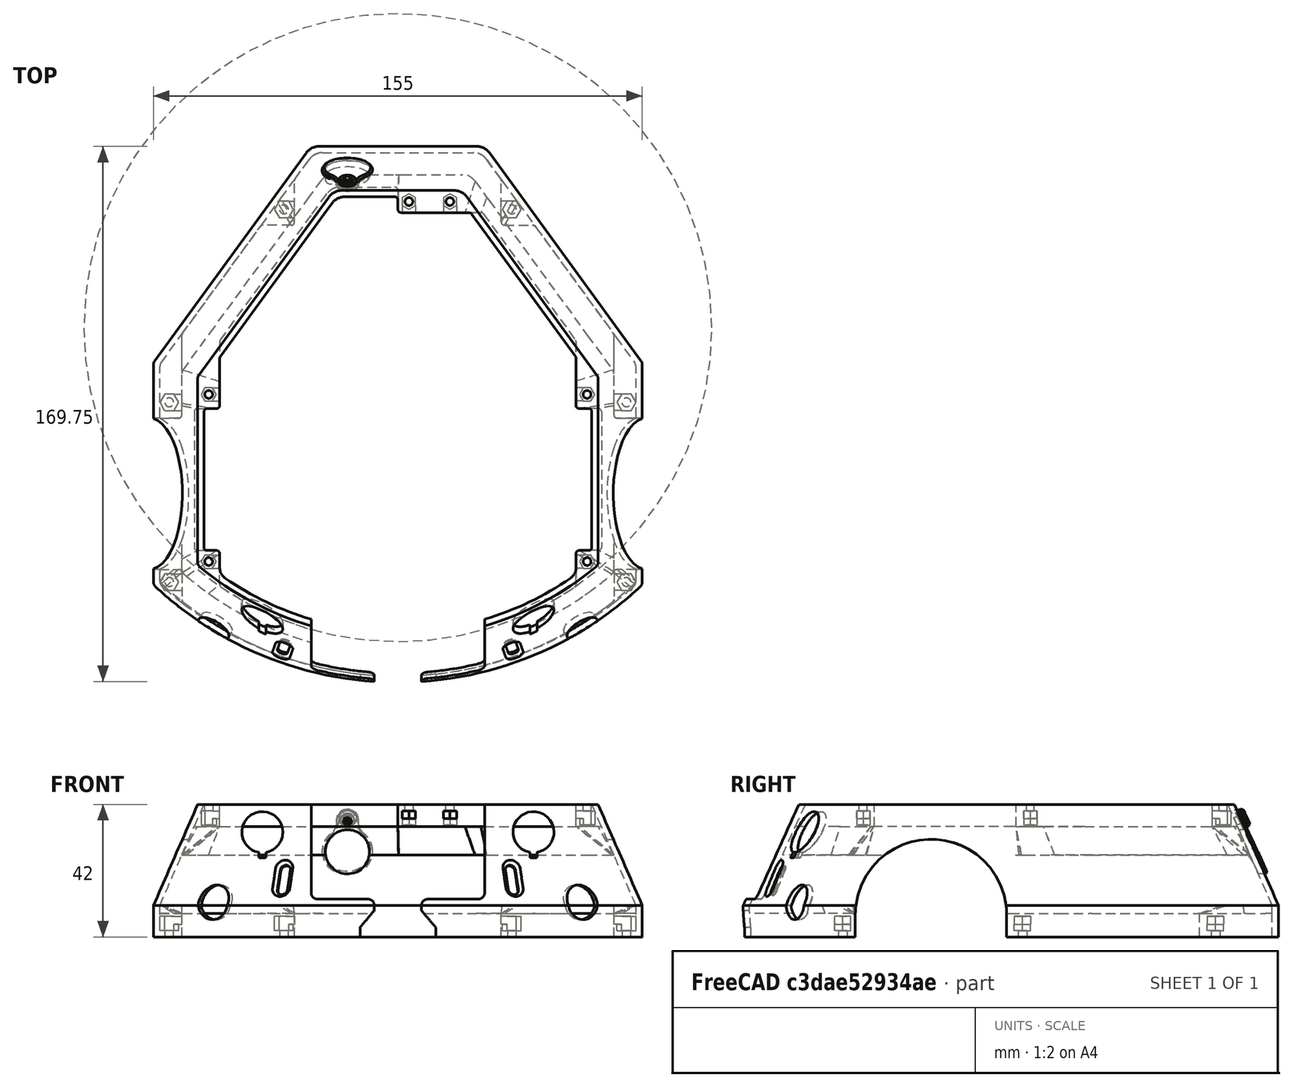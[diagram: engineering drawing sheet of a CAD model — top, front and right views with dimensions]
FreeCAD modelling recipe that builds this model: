
FCSTD DOCUMENT  (FreeCAD 0.19R24276 (Git))
Label: PB3D_TriPlate_Shell
License: All rights reserved
LicenseURL: http://en.wikipedia.org/wiki/All_rights_reserved
objects: Sketcher::SketchObject×33, PartDesign::Pocket×17, PartDesign::Plane×14, PartDesign::SubtractiveLoft×4, PartDesign::Body×3, Spreadsheet::Sheet×2, PartDesign::Pad×2, PartDesign::Chamfer×2, PartDesign::AdditiveLoft×1, PartDesign::Groove×1, PartDesign::Revolution×1, App::Part×1, Mesh::Feature×1
note: 106 computed .brp shape members not serialized (recipe doc carries the construction recipe); baked Part::Feature solids carry a one-line shape summary decoded from their .brp

FEATURE [PartDesign::Plane] DatumPlane  label="Datum_ShelllTop"
  AttachmentOffset = pos=(0,0,42) rot=(0,0,1;0rad)
  Length = 187.44
  MapMode = 5
  Placement = pos=(0,0,42) rot=(0,0,1;0rad)
  ResizeMode = 0
  Support = -> [XY_Plane002]
  Width = 202.177
  expr: .AttachmentOffset.Base.z = Spreadsheet.shell_totheight
FEATURE [PartDesign::Plane] DatumPlane001  label="Datum_ShellVert"
  AttachmentOffset = pos=(0,0,10) rot=(0,0,1;0rad)
  Length = 187.44
  MapMode = 5
  Placement = pos=(0,0,10) rot=(0,0,1;0rad)
  ResizeMode = 0
  Support = -> [XY_Plane002]
  Width = 202.177
  expr: .AttachmentOffset.Base.z = Spreadsheet.shell_vertheight
FEATURE [Spreadsheet::Sheet] Spreadsheet  label="params"
  cells = A1=Std. Wall Thick; B1(std_wall_thick)==2mm; C1=Std. Tol. Clear; D1(std_tol_clear)==0.3mm; A2=Bottom Plate Main Params; C2=Shell Main Params; E2=Shell Calc Params; I2=LSR Vis Holes; A3=Plate Length; B3(plate_length)==170mm; C3=Shell Height; D3(shell_totheight)==42mm; E3=Top Brack Ang Start Z ; F3(shell_topbrack_angstart_z)==shell_totheight - shell_topbrack_vertheight - shell_topbrack_angleheight; G3=Top Brack Ang Start Overhang; H3(shell_topbrack_angstart_overhang)==shell_overhang_slope * shell_topbrack_angstart_z + shell_overhang_offset; I3=LSR Vis Angle; J3(LSRvis_angle)=31.5; A4=Plate Width; B4(plate_width)==155mm; C4=Shell Vert Height; D4(shell_vertheight)==10mm; E4=Top Brack Ang End Z; F4(shell_topbrack_angend_z)==shell_totheight - shell_topbrack_vertheight; G4=Top Bracket End Overhang; H4(shell_topbrack_angend_overhang)==shell_overhang_slope * shell_topbrack_angend_z + shell_overhang_offset; I4=LSR Vis Offset; J4(LSRvis_offset)==52.68mm; A5=Front Diameter; B5(front_diameter)==225mm; C5=Shell Overhang Length; D5(shell_overhang_leng)==14mm; I5=LSR Vis Diam; J5(LSRvis_diam)==11mm; A6=Tail Width; B6(tail_width)==50mm; C6=Shell Wall Thickness; D6(shell_wall_thick)==2mm; G6=Shell Angle Overhang Calc; I6=LSR Vis Hole Height; J6(LSRvis_hole_height)==11mm; A7=Plate Thickness; B7(plate_thick)==3mm; C7=Shell Foot Params; E7=Shell Top Bracket Params; G7=Overhang Slope; H7(shell_overhang_slope)==shell_overhang_leng / (shell_totheight - shell_vertheight); C8=Shell (Foot) Base Bracket Height; D8(shell_foot_height)==7.5mm; E8=Top Brack Height; F8(shell_topbrack_vertheight)==7mm; G8=Overhang Offset; H8(shell_overhang_offset)==-1 * shell_vertheight * shell_overhang_slope; I8=X Port Front; A9=Front Vert. Edge; B9(front_vert_edge)==2mm; C9=Shell Side Foot Width; D9(shell_footside_width)==7mm; E9=Top Brack Angle Height; F9(shell_topbrack_angleheight)==9mm; I9=XPort Diam; J9(xport_diam)==13mm; A10=Back Vert. Edge; B10(back_vert_edge)==15mm; C10=Shell Back Foot Width; D10(shell_footback_width)==10mm; E10=Top Brack Width; F10(shell_topbrack_width)==7mm; G10=Shell Mts; I10=XPort Height Loc; J10(xport_height_loc)==33.25mm; C11=Shell Back Foot Loc; D11(shell_footback_loc)==25mm; E11=Top Brack Front Split; F11(shell_topbrack_frontsplit)==50mm; G11=ShellToBot FrMid Offset; H11(shelltobot_frontmid_offset_xy)==5mm; I11=XPort Offset Loc; J11(xport_offset_loc)==43mm; A12=Std. Radius; B12(std_rad)==2mm; C12=Shell Foot CSunk Z; D12(shell_foot_csunk_z)==2mm; E12=Top Brack CSunk Z; F12(shell_topbrack_csunk_z)==shell_topbrack_slot_z - shell_topbrack_slot_height; G12=ShellToBot Back Offset X; H12(shelltobot_back_offset_x)==6mm; I12=XPort Plate Diam; J12(xport_plate_diam)==16mm; A13=Wheel Well Radius; B13(wheel_well_rad)==7mm; C13=Shell Foot CSunk Height; D13(shell_foot_csunk_height)==m25_nut_min_depth; E13=Top Brack CSunk Height; F13(shell_topbrack_csunk_height)==m2_nut_min_depth + 0.25mm; G13=ShellToBot Back Offset Y; H13(shelltobot_back_offset_y)==20mm; A14=Tail Radius; B14(tail_rad)==5mm; C14=Shell Foot Slot Z; D14(shell_foot_slot_z)==shell_foot_csunk_z + shell_foot_csunk_height; E14=Top Brack Slot Z; F14(shell_topbrack_slot_z)==shell_totheight - 2mm; C15=Shell Foot Slot Height; D15(shell_foot_slot_height)==m25_nut_min_depth + 0.5mm; E15=Top Brack Slot Height; F15(shell_topbrack_slot_height)==m2_nut_min_depth + 0.75mm; G15=USB Port Opening; A16=Wheel Well Plate Width; B16(wheel_well_plate_width)==115mm; E16=Top Brack Hole Offset; F16(shell_topbrack_hole_offset)==3.5mm; G16=USBPort Diam; H16(USBport_diam)==14mm; A17=Wheel Well Clearance; B17(wheel_well_clearance)==48mm; C17=Shell Angled Height; D17(shell_overhang_height)==shell_totheight - shell_vertheight; E17=Top Brack Fr Leng; F17(top_brack_front_leng)==10mm; G17=USBPort Height; H17(USBport_height)==27mm; A18=Wheel Well Vert; B18(wheel_well_vert)==7mm; C18=Shell Angle; D18(shell_wall_angle)==atan(shell_overhang_leng / shell_overhang_height); G18=USBPort X Offset; H18(USBport_offset_x)==16mm; G19=USBPort Cover Diam; H19(USBport_cover_diam)==16mm; A20=M2 Bolt Clearances; C20=M2.5 Bolt Clearances; G20=USBPort Cover Mt Pt; H20(USBport_cover_mt_diam)==7mm; A21=Hole Clear Diam; B21(m2_hole_clear_diam)==2.5mm; C21=Hole Clear Diam; D21(m25_hole_clear_diam)==2.8mm; G21=USBPort Cover Spacing; H21(USBport_cover_spacing)==11mm; A22=Head Clear Diam; B22(m2_head_clear_diam)==4mm; C22=Head Clear Diam; D22(m25_head_clear_diam)==5mm; G22=USBPort Cov Thickness; H22(USBport_cover_thickness)==1.2mm; A23=Head Min Depth; B23(m2_head_min_depth)==1.3mm; C23=Head Min Depth; D23(m25_head_min_depth)==1.6mm; A24=Nut Clear Flat; B24(m2_nut_clear_flat)==4.2mm; C24=Nut Clear Flat; D24(m25_nut_clear_flat)==5.2mm; G24=USBPort Cov Pivot In Diam; H24(USBport_cover_pivot_inner_diam)==4mm; A25=Nut Min Depth; B25(m2_nut_min_depth)==1.75mm; C25=Nut Min Depth; D25(m25_nut_min_depth)==2mm; G25=USBPort Cov Pivot Out Diam; H25(USBport_cover_pivot_outer_diam)==USBport_cover_pivot_inner_diam + 0.3mm; G26=USBPort Cov Pivot Height; H26(USBport_cover_pivot_height)==USBport_cover_thickness + 0.1mm
FEATURE [Sketcher::SketchObject] Sketch001  label="Sketch_Shell"
  FullyConstrained = true
  MapMode = 5
  Support = -> [XY_Plane002]
  expr: Constraints[41] = <<params>>.tail_rad
  expr: Constraints[81] = <<params>>.std_rad
  expr: Constraints[80] = <<params>>.std_rad
  expr: Constraints[77] = <<params>>.back_vert_edge
  expr: Constraints[76] = <<params>>.front_vert_edge
  expr: Constraints[63] = <<params>>.std_rad
  expr: Constraints[47] = <<params>>.front_diameter
  expr: Constraints[36] = <<params>>.wheel_well_plate_width
  expr: Constraints[79] = <<params>>.plate_width
  expr: Constraints[78] = <<params>>.wheel_well_clearance
  expr: Constraints[42] = <<params>>.tail_width
  expr: Constraints[65] = <<params>>.std_rad
  expr: Constraints[40] = <<params>>.plate_length
  sketch-geometry (36):
    g0: LineSegment StartX=-57.5 StartY=17 StartZ=0 EndX=-57.5 EndY=-17 EndZ=0
    g1: LineSegment StartX=57.5 StartY=17 StartZ=0 EndX=57.5 EndY=-17 EndZ=0
    g2: LineSegment StartX=-57.5 StartY=0 StartZ=0 EndX=57.5 EndY=0 EndZ=0
    g3: LineSegment StartX=-64.5 StartY=-24 StartZ=0 EndX=64.5 EndY=-24 EndZ=0
    g4: LineSegment StartX=-64.5 StartY=24 StartZ=0 EndX=64.5 EndY=24 EndZ=0
    g5: LineSegment StartX=-64.5 StartY=-24 StartZ=0 EndX=-75.5 EndY=-24 EndZ=0
    g6: LineSegment StartX=64.5 StartY=-24 StartZ=0 EndX=75.5 EndY=-24 EndZ=0
    g7: ArcOfCircle CenterX=0 CenterY=52.6846 CenterZ=0 NormalX=0 NormalY=0 NormalZ=1 AngleXU=0 Radius=112.5 StartAngle=3.96017 EndAngle=5.4646
    g8: LineSegment StartX=-64.5 StartY=24 StartZ=0 EndX=-75.5 EndY=24 EndZ=0
    g9: LineSegment StartX=64.5 StartY=24 StartZ=0 EndX=75.5 EndY=24 EndZ=0
    g10: LineSegment StartX=-77.1162 StartY=42.1781 StartZ=0 EndX=-29.0404 EndY=108.13 EndZ=0
    g11: LineSegment StartX=-25 StartY=110.185 StartZ=0 EndX=25 EndY=110.185 EndZ=0
    g12: LineSegment StartX=29.0404 StartY=108.13 StartZ=0 EndX=77.1162 EndY=42.1781 EndZ=0
    g13: LineSegment StartX=0 StartY=0 StartZ=0 EndX=0 EndY=110.185 EndZ=0
    g14: ArcOfCircle CenterX=-25 CenterY=105.185 CenterZ=0 NormalX=0 NormalY=0 NormalZ=1 AngleXU=0 Radius=5 StartAngle=1.5708 EndAngle=2.5117
    g15: ArcOfCircle CenterX=25 CenterY=105.185 CenterZ=0 NormalX=0 NormalY=0 NormalZ=1 AngleXU=0 Radius=5 StartAngle=0.629894 EndAngle=1.5708
    g16: ArcOfCircle CenterX=-64.5 CenterY=17 CenterZ=0 NormalX=0 NormalY=0 NormalZ=1 AngleXU=0 Radius=7 StartAngle=0 EndAngle=1.5708
    g17: ArcOfCircle CenterX=-64.5 CenterY=-17 CenterZ=0 NormalX=0 NormalY=0 NormalZ=1 AngleXU=0 Radius=7 StartAngle=4.71239 EndAngle=6.28319
    g18: ArcOfCircle CenterX=64.5 CenterY=-17 CenterZ=0 NormalX=0 NormalY=0 NormalZ=1 AngleXU=0 Radius=7 StartAngle=3.14159 EndAngle=4.71239
    g19: ArcOfCircle CenterX=64.5 CenterY=17 CenterZ=0 NormalX=0 NormalY=0 NormalZ=1 AngleXU=0 Radius=7 StartAngle=1.5708 EndAngle=3.14159
    g20: GeomPoint X=0 Y=-59.8154 Z=0
    g21: Circle CenterX=0 CenterY=52.6846 CenterZ=0 NormalX=0 NormalY=0 NormalZ=1 AngleXU=0 Radius=112.5
    g22: LineSegment StartX=77.5 StartY=26 StartZ=0 EndX=77.5 EndY=41 EndZ=0
    g23: LineSegment StartX=77.5 StartY=-26 StartZ=0 EndX=77.5 EndY=-28 EndZ=0
    g24: LineSegment StartX=-77.5 StartY=-28 StartZ=0 EndX=-77.5 EndY=-26 EndZ=0
    g25: LineSegment StartX=-77.5 StartY=26 StartZ=0 EndX=-77.5 EndY=41 EndZ=0
    g26: ArcOfCircle CenterX=75.5 CenterY=-28 CenterZ=0 NormalX=0 NormalY=0 NormalZ=1 AngleXU=0 Radius=2 StartAngle=5.4646 EndAngle=6.28319
    g27: ArcOfCircle CenterX=75.5 CenterY=-26 CenterZ=0 NormalX=0 NormalY=0 NormalZ=1 AngleXU=0 Radius=2 StartAngle=3e-16 EndAngle=1.5708
    g28: ArcOfCircle CenterX=-75.5 CenterY=-28 CenterZ=0 NormalX=0 NormalY=0 NormalZ=1 AngleXU=0 Radius=2 StartAngle=3.14159 EndAngle=3.96017
    g29: ArcOfCircle CenterX=-75.5 CenterY=-26 CenterZ=0 NormalX=0 NormalY=0 NormalZ=1 AngleXU=0 Radius=2 StartAngle=1.5708 EndAngle=3.14159
    g30: ArcOfCircle CenterX=75.5 CenterY=26 CenterZ=0 NormalX=0 NormalY=0 NormalZ=1 AngleXU=0 Radius=2 StartAngle=4.71239 EndAngle=6.28319
    g31: ArcOfCircle CenterX=75.5 CenterY=41 CenterZ=0 NormalX=0 NormalY=0 NormalZ=1 AngleXU=0 Radius=2 StartAngle=-9e-16 EndAngle=0.629894
    g32: ArcOfCircle CenterX=-75.5 CenterY=26 CenterZ=0 NormalX=0 NormalY=0 NormalZ=1 AngleXU=0 Radius=2 StartAngle=3.14159 EndAngle=4.71239
    g33: ArcOfCircle CenterX=-75.5 CenterY=41 CenterZ=0 NormalX=0 NormalY=0 NormalZ=1 AngleXU=0 Radius=2 StartAngle=2.5117 EndAngle=3.14159
    g34: LineSegment StartX=77.5 StartY=26 StartZ=0 EndX=77.5 EndY=-26 EndZ=0
    g35: LineSegment StartX=-77.5 StartY=26 StartZ=0 EndX=-77.5 EndY=-26 EndZ=0
  constraints (86):
    c: Vertical(g0)
    c: Vertical(g1)
    c: Horizontal(g2)
    c: Symmetric(g2,g2,g-1)
    c: Horizontal(g3)
    c: Horizontal(g5)
    c: Horizontal(g6)
    c: PointOnObject(g7,g-2)
    c: Horizontal(g8)
    c: Horizontal(g9)
    c: Horizontal(g11)
    c: Coincident(g13,g-1)
    c: PointOnObject(g13,g-2)
    c: Tangent(g10,g14) = 1.5708
    c: Tangent(g11,g14) = 1.5708
    c: Tangent(g11,g15) = 1.5708
    c: Tangent(g12,g15) = 1.5708
    c: Tangent(g8,g16) = -1.5708
    c: Tangent(g0,g16) = 1.5708
    c: Tangent(g5,g17) = 1.5708
    c: Tangent(g0,g17) = 1.5708
    c: Tangent(g1,g18) = -1.5708
    c: Tangent(g6,g18) = -1.5708
    c: Tangent(g1,g19) = -1.5708
    c: Tangent(g9,g19) = 1.5708
    c: Equal(g15,g14)
    c: Symmetric(g11,g11,g13)
    c: Equal(g18,g19)
    c: Equal(g19,g16)
    c: Equal(g16,g17)
    c: PointOnObject(g20,g-2)
    c: PointOnObject(g20,g7)
    c: Coincident(g4,g8)
    c: Coincident(g4,g9)
    c: Coincident(g3,g6)
    c: Coincident(g3,g5)
    c: DistanceX(g2,g2) = 115
    c: Symmetric(g0,g0,g2)
    c: Symmetric(g1,g1,g2)
    c: Radius(g19) = 7
    c: DistanceY(g20,g11) = 170
    c: Radius(g15) = 5
    c: DistanceX(g11,g11) = 50
    c: Equal(g9,g8)
    c: Equal(g9,g6)
    c: Coincident(g21,g7)
    c: PointOnObject(g20,g21)
    c: Diameter(g21) = 225
    c: Vertical(g22)
    c: Vertical(g23)
    c: Vertical(g24)
    c: Vertical(g25)
    c: Equal(g5,g8)
    c: Equal(g10,g12)
    c: Tangent(g7,g26) = -1.5708
    c: Tangent(g23,g26) = 1.5708
    c: Tangent(g23,g27) = 1.5708
    c: Tangent(g6,g27) = 1.5708
    c: Tangent(g7,g28) = -1.5708
    c: Tangent(g24,g28) = 1.5708
    c: Tangent(g24,g29) = 1.5708
    c: Tangent(g5,g29) = -1.5708
    c: Equal(g29,g27)
    c: Radius(g27) = 2
    c: Equal(g26,g28)
    c: Radius(g26) = 2
    c: Tangent(g9,g30) = -1.5708
    c: Tangent(g22,g30) = -1.5708
    c: Tangent(g22,g31) = -1.5708
    c: Tangent(g12,g31) = 1.5708
    c: Tangent(g8,g32) = 1.5708
    c: Tangent(g25,g32) = 1.5708
    c: Tangent(g10,g33) = 1.5708
    c: Tangent(g25,g33) = 1.5708
    c: Equal(g30,g32)
    c: Equal(g31,g33)
    c: DistanceY(g23,g23) = 2
    c: DistanceY(g22,g22) = 15
    c: DistanceY(g6,g9) = 48
    c: DistanceX(g24,g23) = 155
    c: Radius(g30) = 2
    c: Radius(g31) = 2
    c: Coincident(g34,g22)
    c: Coincident(g34,g23)
    c: Coincident(g35,g25)
    c: Coincident(g35,g24)
FEATURE [PartDesign::Pad] Pad001  label="Shell_Vert_Ext"
  Direction = (1,1,1)
  Length = 10
  Length2 = 100
  Profile = -> Sketch001
  Type = 0
  expr: Length = Spreadsheet.shell_vertheight
FEATURE [Sketcher::SketchObject] Sketch002  label="Sketch_Shell_Vert"
  FullyConstrained = true
  MapMode = 5
  Placement = pos=(0,0,10) rot=(0,0,1;0rad)
  Support = -> [DatumPlane001]
  expr: Constraints[40] = <<params>>.plate_length
  expr: Constraints[65] = <<params>>.std_rad
  expr: Constraints[42] = <<params>>.tail_width
  expr: Constraints[78] = <<params>>.wheel_well_clearance
  expr: Constraints[79] = <<params>>.plate_width
  expr: Constraints[36] = <<params>>.wheel_well_plate_width
  expr: Constraints[47] = <<params>>.front_diameter
  expr: Constraints[63] = <<params>>.std_rad
  expr: Constraints[76] = <<params>>.front_vert_edge
  expr: Constraints[77] = <<params>>.back_vert_edge
  expr: Constraints[80] = <<params>>.std_rad
  expr: Constraints[81] = <<params>>.std_rad
  expr: Constraints[41] = <<params>>.tail_rad
  sketch-geometry (38):
    g0: LineSegment StartX=-57.5 StartY=17 StartZ=0 EndX=-57.5 EndY=-17 EndZ=0
    g1: LineSegment StartX=57.5 StartY=17 StartZ=0 EndX=57.5 EndY=-17 EndZ=0
    g2: LineSegment StartX=-57.5 StartY=0 StartZ=0 EndX=57.5 EndY=0 EndZ=0
    g3: LineSegment StartX=-64.5 StartY=-24 StartZ=0 EndX=64.5 EndY=-24 EndZ=0
    g4: LineSegment StartX=-64.5 StartY=24 StartZ=0 EndX=64.5 EndY=24 EndZ=0
    g5: LineSegment StartX=-64.5 StartY=-24 StartZ=0 EndX=-75.5 EndY=-24 EndZ=0
    g6: LineSegment StartX=64.5 StartY=-24 StartZ=0 EndX=75.5 EndY=-24 EndZ=0
    g7: ArcOfCircle CenterX=0 CenterY=52.6846 CenterZ=0 NormalX=0 NormalY=0 NormalZ=1 AngleXU=0 Radius=112.5 StartAngle=3.96017 EndAngle=5.4646
    g8: LineSegment StartX=-64.5 StartY=24 StartZ=0 EndX=-75.5 EndY=24 EndZ=0
    g9: LineSegment StartX=64.5 StartY=24 StartZ=0 EndX=75.5 EndY=24 EndZ=0
    g10: LineSegment StartX=-77.1162 StartY=42.1781 StartZ=0 EndX=-29.0404 EndY=108.13 EndZ=0
    g11: LineSegment StartX=-25 StartY=110.185 StartZ=0 EndX=25 EndY=110.185 EndZ=0
    g12: LineSegment StartX=29.0404 StartY=108.13 StartZ=0 EndX=77.1162 EndY=42.1781 EndZ=0
    g13: LineSegment StartX=0 StartY=0 StartZ=0 EndX=0 EndY=110.185 EndZ=0
    g14: ArcOfCircle CenterX=-25 CenterY=105.185 CenterZ=0 NormalX=0 NormalY=0 NormalZ=1 AngleXU=0 Radius=5 StartAngle=1.5708 EndAngle=2.5117
    g15: ArcOfCircle CenterX=25 CenterY=105.185 CenterZ=0 NormalX=0 NormalY=0 NormalZ=1 AngleXU=0 Radius=5 StartAngle=0.629894 EndAngle=1.5708
    g16: ArcOfCircle CenterX=-64.5 CenterY=17 CenterZ=0 NormalX=0 NormalY=0 NormalZ=1 AngleXU=0 Radius=7 StartAngle=0 EndAngle=1.5708
    g17: ArcOfCircle CenterX=-64.5 CenterY=-17 CenterZ=0 NormalX=0 NormalY=0 NormalZ=1 AngleXU=0 Radius=7 StartAngle=4.71239 EndAngle=6.28319
    g18: ArcOfCircle CenterX=64.5 CenterY=-17 CenterZ=0 NormalX=0 NormalY=0 NormalZ=1 AngleXU=0 Radius=7 StartAngle=3.14159 EndAngle=4.71239
    g19: ArcOfCircle CenterX=64.5 CenterY=17 CenterZ=0 NormalX=0 NormalY=0 NormalZ=1 AngleXU=0 Radius=7 StartAngle=1.5708 EndAngle=3.14159
    g20: GeomPoint X=0 Y=-59.8154 Z=0
    g21: Circle CenterX=0 CenterY=52.6846 CenterZ=0 NormalX=0 NormalY=0 NormalZ=1 AngleXU=0 Radius=112.5
    g22: LineSegment StartX=77.5 StartY=26 StartZ=0 EndX=77.5 EndY=41 EndZ=0
    g23: LineSegment StartX=77.5 StartY=-26 StartZ=0 EndX=77.5 EndY=-28 EndZ=0
    g24: LineSegment StartX=-77.5 StartY=-28 StartZ=0 EndX=-77.5 EndY=-26 EndZ=0
    g25: LineSegment StartX=-77.5 StartY=26 StartZ=0 EndX=-77.5 EndY=41 EndZ=0
    g26: ArcOfCircle CenterX=75.5 CenterY=-28 CenterZ=0 NormalX=0 NormalY=0 NormalZ=1 AngleXU=0 Radius=2 StartAngle=5.4646 EndAngle=6.28319
    g27: ArcOfCircle CenterX=75.5 CenterY=-26 CenterZ=0 NormalX=0 NormalY=0 NormalZ=1 AngleXU=0 Radius=2 StartAngle=-9e-16 EndAngle=1.5708
    g28: ArcOfCircle CenterX=-75.5 CenterY=-28 CenterZ=0 NormalX=0 NormalY=0 NormalZ=1 AngleXU=0 Radius=2 StartAngle=3.14159 EndAngle=3.96017
    g29: ArcOfCircle CenterX=-75.5 CenterY=-26 CenterZ=0 NormalX=0 NormalY=0 NormalZ=1 AngleXU=0 Radius=2 StartAngle=1.5708 EndAngle=3.14159
    g30: ArcOfCircle CenterX=75.5 CenterY=26 CenterZ=0 NormalX=0 NormalY=0 NormalZ=1 AngleXU=0 Radius=2 StartAngle=4.71239 EndAngle=6.28319
    g31: ArcOfCircle CenterX=75.5 CenterY=41 CenterZ=0 NormalX=0 NormalY=0 NormalZ=1 AngleXU=0 Radius=2 StartAngle=0 EndAngle=0.629894
    g32: ArcOfCircle CenterX=-75.5 CenterY=26 CenterZ=0 NormalX=0 NormalY=0 NormalZ=1 AngleXU=0 Radius=2 StartAngle=3.14159 EndAngle=4.71239
    g33: ArcOfCircle CenterX=-75.5 CenterY=41 CenterZ=0 NormalX=0 NormalY=0 NormalZ=1 AngleXU=0 Radius=2 StartAngle=2.5117 EndAngle=3.14159
    g34: LineSegment StartX=77.5 StartY=26 StartZ=0 EndX=77.5 EndY=-26 EndZ=0
    g35: LineSegment StartX=-77.5 StartY=26 StartZ=0 EndX=-77.5 EndY=-26 EndZ=0
    g36: LineSegment StartX=77.5 StartY=41 StartZ=0 EndX=77.5 EndY=-28 EndZ=0
    g37: LineSegment StartX=-77.5 StartY=41 StartZ=0 EndX=-77.5 EndY=-28 EndZ=0
  constraints (90):
    c: Vertical(g0)
    c: Vertical(g1)
    c: Horizontal(g2)
    c: Symmetric(g2,g2,g-1)
    c: Horizontal(g3)
    c: Horizontal(g5)
    c: Horizontal(g6)
    c: PointOnObject(g7,g-2)
    c: Horizontal(g8)
    c: Horizontal(g9)
    c: Horizontal(g11)
    c: Coincident(g13,g-1)
    c: PointOnObject(g13,g-2)
    c: Tangent(g10,g14) = 1.5708
    c: Tangent(g11,g14) = 1.5708
    c: Tangent(g11,g15) = 1.5708
    c: Tangent(g12,g15) = 1.5708
    c: Tangent(g8,g16) = -1.5708
    c: Tangent(g0,g16) = 1.5708
    c: Tangent(g5,g17) = 1.5708
    c: Tangent(g0,g17) = 1.5708
    c: Tangent(g1,g18) = -1.5708
    c: Tangent(g6,g18) = -1.5708
    c: Tangent(g1,g19) = -1.5708
    c: Tangent(g9,g19) = 1.5708
    c: Equal(g15,g14)
    c: Symmetric(g11,g11,g13)
    c: Equal(g18,g19)
    c: Equal(g19,g16)
    c: Equal(g16,g17)
    c: PointOnObject(g20,g-2)
    c: PointOnObject(g20,g7)
    c: Coincident(g4,g8)
    c: Coincident(g4,g9)
    c: Coincident(g3,g6)
    c: Coincident(g3,g5)
    c: DistanceX(g2,g2) = 115
    c: Symmetric(g0,g0,g2)
    c: Symmetric(g1,g1,g2)
    c: Radius(g19) = 7
    c: DistanceY(g20,g11) = 170
    c: Radius(g15) = 5
    c: DistanceX(g11,g11) = 50
    c: Equal(g9,g8)
    c: Equal(g9,g6)
    c: Coincident(g21,g7)
    c: PointOnObject(g20,g21)
    c: Diameter(g21) = 225
    c: Vertical(g22)
    c: Vertical(g23)
    c: Vertical(g24)
    c: Vertical(g25)
    c: Equal(g5,g8)
    c: Equal(g10,g12)
    c: Tangent(g7,g26) = -1.5708
    c: Tangent(g23,g26) = 1.5708
    c: Tangent(g23,g27) = 1.5708
    c: Tangent(g6,g27) = 1.5708
    c: Tangent(g7,g28) = -1.5708
    c: Tangent(g24,g28) = 1.5708
    c: Tangent(g24,g29) = 1.5708
    c: Tangent(g5,g29) = -1.5708
    c: Equal(g29,g27)
    c: Radius(g27) = 2
    c: Equal(g26,g28)
    c: Radius(g26) = 2
    c: Tangent(g9,g30) = -1.5708
    c: Tangent(g22,g30) = -1.5708
    c: Tangent(g22,g31) = -1.5708
    c: Tangent(g12,g31) = 1.5708
    c: Tangent(g8,g32) = 1.5708
    c: Tangent(g25,g32) = 1.5708
    c: Tangent(g10,g33) = 1.5708
    c: Tangent(g25,g33) = 1.5708
    c: Equal(g30,g32)
    c: Equal(g31,g33)
    c: DistanceY(g23,g23) = 2
    c: DistanceY(g22,g22) = 15
    c: DistanceY(g6,g9) = 48
    c: DistanceX(g24,g23) = 155
    c: Radius(g30) = 2
    c: Radius(g31) = 2
    c: Coincident(g34,g22)
    c: Coincident(g34,g23)
    c: Coincident(g35,g25)
    c: Coincident(g35,g24)
    c: Coincident(g37,g28)
    c: Coincident(g37,g33)
    c: Coincident(g36,g31)
    c: Coincident(g36,g26)
FEATURE [Sketcher::SketchObject] Sketch003  label="Sketch_Shell_Top"
  FullyConstrained = true
  MapMode = 5
  Placement = pos=(0,0,42) rot=(0,0,1;0rad)
  Support = -> [DatumPlane]
  expr: Constraints[114] = <<params>>.shell_overhang_leng
  expr: Constraints[63] = <<params>>.std_rad
  expr: Constraints[47] = <<params>>.front_diameter
  expr: Constraints[113] = Spreadsheet.shell_overhang_leng
  expr: Constraints[77] = <<params>>.back_vert_edge
  expr: Constraints[119] = <<params>>.shell_overhang_leng
  expr: Constraints[117] = <<params>>.shell_overhang_leng
  expr: Constraints[80] = <<params>>.std_rad
  expr: Constraints[41] = <<params>>.tail_rad
  expr: Constraints[76] = <<params>>.front_vert_edge
  expr: Constraints[36] = <<params>>.wheel_well_plate_width - 2 * Spreadsheet.shell_overhang_leng
  expr: Constraints[79] = <<params>>.plate_width
  expr: Constraints[42] = <<params>>.tail_width
  expr: Constraints[78] = <<params>>.wheel_well_clearance
  expr: Constraints[65] = <<params>>.std_rad
  expr: Constraints[40] = <<params>>.plate_length
  expr: Constraints[88] = Spreadsheet.shell_overhang_leng
  expr: Constraints[81] = <<params>>.std_rad
  sketch-geometry (52):
    g0: LineSegment StartX=-43.5 StartY=17 StartZ=0 EndX=-43.5 EndY=-17 EndZ=0
    g1: LineSegment StartX=43.5 StartY=17 StartZ=0 EndX=43.5 EndY=-17 EndZ=0
    g2: LineSegment StartX=-43.5 StartY=0 StartZ=0 EndX=43.5 EndY=0 EndZ=0
    g3: LineSegment StartX=-50.5 StartY=-24 StartZ=0 EndX=50.5 EndY=-24 EndZ=0
    g4: LineSegment StartX=-50.5 StartY=24 StartZ=0 EndX=50.5 EndY=24 EndZ=0
    g5: LineSegment StartX=-50.5 StartY=-24 StartZ=0 EndX=-75.5 EndY=-24 EndZ=0
    g6: LineSegment StartX=50.5 StartY=-24 StartZ=0 EndX=75.5 EndY=-24 EndZ=0
    g7: ArcOfCircle CenterX=0 CenterY=52.6846 CenterZ=0 NormalX=0 NormalY=0 NormalZ=1 AngleXU=0 Radius=112.5 StartAngle=3.96017 EndAngle=5.4646
    g8: LineSegment StartX=-50.5 StartY=24 StartZ=0 EndX=-75.5 EndY=24 EndZ=0
    g9: LineSegment StartX=50.5 StartY=24 StartZ=0 EndX=75.5 EndY=24 EndZ=0
    g10: LineSegment StartX=-77.1162 StartY=42.1781 StartZ=0 EndX=-29.0404 EndY=108.13 EndZ=0
    g11: LineSegment StartX=-25 StartY=110.185 StartZ=0 EndX=25 EndY=110.185 EndZ=0
    g12: LineSegment StartX=29.0404 StartY=108.13 StartZ=0 EndX=77.1162 EndY=42.1781 EndZ=0
    g13: LineSegment StartX=0 StartY=0 StartZ=0 EndX=0 EndY=110.185 EndZ=0
    g14: ArcOfCircle CenterX=-25 CenterY=105.185 CenterZ=0 NormalX=0 NormalY=0 NormalZ=1 AngleXU=0 Radius=5 StartAngle=1.5708 EndAngle=2.5117
    g15: ArcOfCircle CenterX=25 CenterY=105.185 CenterZ=0 NormalX=0 NormalY=0 NormalZ=1 AngleXU=0 Radius=5 StartAngle=0.629894 EndAngle=1.5708
    g16: ArcOfCircle CenterX=-50.5 CenterY=17 CenterZ=0 NormalX=0 NormalY=0 NormalZ=1 AngleXU=0 Radius=7 StartAngle=0 EndAngle=1.5708
    g17: ArcOfCircle CenterX=-50.5 CenterY=-17 CenterZ=0 NormalX=0 NormalY=0 NormalZ=1 AngleXU=0 Radius=7 StartAngle=4.71239 EndAngle=6.28319
    g18: ArcOfCircle CenterX=50.5 CenterY=-17 CenterZ=0 NormalX=0 NormalY=0 NormalZ=1 AngleXU=0 Radius=7 StartAngle=3.14159 EndAngle=4.71239
    g19: ArcOfCircle CenterX=50.5 CenterY=17 CenterZ=0 NormalX=0 NormalY=0 NormalZ=1 AngleXU=0 Radius=7 StartAngle=1.5708 EndAngle=3.14159
    g20: GeomPoint X=0 Y=-59.8154 Z=0
    g21: Circle CenterX=0 CenterY=52.6846 CenterZ=0 NormalX=0 NormalY=0 NormalZ=1 AngleXU=0 Radius=112.5
    g22: LineSegment StartX=77.5 StartY=26 StartZ=0 EndX=77.5 EndY=41 EndZ=0
    g23: LineSegment StartX=77.5 StartY=-26 StartZ=0 EndX=77.5 EndY=-28 EndZ=0
    g24: LineSegment StartX=-77.5 StartY=-28 StartZ=0 EndX=-77.5 EndY=-26 EndZ=0
    g25: LineSegment StartX=-77.5 StartY=26 StartZ=0 EndX=-77.5 EndY=41 EndZ=0
    g26: ArcOfCircle CenterX=75.5 CenterY=-28 CenterZ=0 NormalX=0 NormalY=0 NormalZ=1 AngleXU=0 Radius=2 StartAngle=5.4646 EndAngle=6.28319
    g27: ArcOfCircle CenterX=75.5 CenterY=-26 CenterZ=0 NormalX=0 NormalY=0 NormalZ=1 AngleXU=0 Radius=2 StartAngle=0 EndAngle=1.5708
    g28: ArcOfCircle CenterX=-75.5 CenterY=-28 CenterZ=0 NormalX=0 NormalY=0 NormalZ=1 AngleXU=0 Radius=2 StartAngle=3.14159 EndAngle=3.96017
    g29: ArcOfCircle CenterX=-75.5 CenterY=-26 CenterZ=0 NormalX=0 NormalY=0 NormalZ=1 AngleXU=0 Radius=2 StartAngle=1.5708 EndAngle=3.14159
    g30: ArcOfCircle CenterX=75.5 CenterY=26 CenterZ=0 NormalX=0 NormalY=0 NormalZ=1 AngleXU=0 Radius=2 StartAngle=4.71239 EndAngle=6.28319
    g31: ArcOfCircle CenterX=75.5 CenterY=41 CenterZ=0 NormalX=0 NormalY=0 NormalZ=1 AngleXU=0 Radius=2 StartAngle=1.7e-15 EndAngle=0.629894
    g32: ArcOfCircle CenterX=-75.5 CenterY=26 CenterZ=0 NormalX=0 NormalY=0 NormalZ=1 AngleXU=0 Radius=2 StartAngle=3.14159 EndAngle=4.71239
    g33: ArcOfCircle CenterX=-75.5 CenterY=41 CenterZ=0 NormalX=0 NormalY=0 NormalZ=1 AngleXU=0 Radius=2 StartAngle=2.5117 EndAngle=3.14159
    g34: LineSegment StartX=77.5 StartY=26 StartZ=0 EndX=77.5 EndY=-26 EndZ=0
    g35: LineSegment StartX=-77.5 StartY=26 StartZ=0 EndX=-77.5 EndY=-26 EndZ=0
    g36: LineSegment StartX=-17.8805 StartY=96.1846 StartZ=0 EndX=17.8805 EndY=96.1846 EndZ=0
    g37: GeomPoint X=0 Y=96.1846 Z=0
    g38: LineSegment StartX=-21.921 StartY=94.1299 StartZ=0 EndX=-63.1162 EndY=37.617 EndZ=0
    g39: LineSegment StartX=-63.5 StartY=36.4389 StartZ=0 EndX=-63.5 EndY=-21.6794 EndZ=0
    g40: LineSegment StartX=21.921 StartY=94.1299 StartZ=0 EndX=63.1162 EndY=37.617 EndZ=0
    g41: LineSegment StartX=63.5 StartY=36.4389 StartZ=0 EndX=63.5 EndY=-21.6794 EndZ=0
    g42: LineSegment StartX=-63.5 StartY=36.4389 StartZ=0 EndX=63.5 EndY=36.4389 EndZ=0
    g43: GeomPoint X=0 Y=-45.8154 Z=0
    g44: ArcOfCircle CenterX=-17.8805 CenterY=91.1846 CenterZ=0 NormalX=0 NormalY=0 NormalZ=1 AngleXU=0 Radius=5 StartAngle=1.5708 EndAngle=2.5117
    g45: ArcOfCircle CenterX=17.8805 CenterY=91.1846 CenterZ=0 NormalX=0 NormalY=0 NormalZ=1 AngleXU=0 Radius=5 StartAngle=0.629894 EndAngle=1.5708
    g46: ArcOfCircle CenterX=61.5 CenterY=36.4389 CenterZ=0 NormalX=0 NormalY=0 NormalZ=1 AngleXU=0 Radius=2 StartAngle=9e-16 EndAngle=0.629894
    g47: ArcOfCircle CenterX=-61.5 CenterY=36.4389 CenterZ=0 NormalX=0 NormalY=0 NormalZ=1 AngleXU=0 Radius=2 StartAngle=2.5117 EndAngle=3.14159
    g48: ArcOfCircle CenterX=61.5 CenterY=-21.6794 CenterZ=0 NormalX=0 NormalY=0 NormalZ=1 AngleXU=0 Radius=2 StartAngle=5.40338 EndAngle=6.28319
    g49: ArcOfCircle CenterX=-61.5 CenterY=-21.6794 CenterZ=0 NormalX=0 NormalY=0 NormalZ=1 AngleXU=0 Radius=2 StartAngle=3.14159 EndAngle=4.02139
    g50: LineSegment StartX=-29.0404 StartY=108.13 StartZ=0 EndX=-17.7272 EndY=99.883 EndZ=0
    g51: ArcOfCircle CenterX=0 CenterY=52.6846 CenterZ=0 NormalX=0 NormalY=0 NormalZ=1 AngleXU=0 Radius=98.5 StartAngle=4.02139 EndAngle=5.40339
  constraints (126):
    c: Vertical(g0)
    c: Vertical(g1)
    c: Horizontal(g2)
    c: Symmetric(g2,g2,g-1)
    c: Horizontal(g3)
    c: Horizontal(g5)
    c: Horizontal(g6)
    c: PointOnObject(g7,g-2)
    c: Horizontal(g8)
    c: Horizontal(g9)
    c: Horizontal(g11)
    c: Coincident(g13,g-1)
    c: PointOnObject(g13,g-2)
    c: Tangent(g10,g14) = 1.5708
    c: Tangent(g11,g14) = 1.5708
    c: Tangent(g11,g15) = 1.5708
    c: Tangent(g12,g15) = 1.5708
    c: Tangent(g8,g16) = -1.5708
    c: Tangent(g0,g16) = 1.5708
    c: Tangent(g5,g17) = 1.5708
    c: Tangent(g0,g17) = 1.5708
    c: Tangent(g1,g18) = -1.5708
    c: Tangent(g6,g18) = -1.5708
    c: Tangent(g1,g19) = -1.5708
    c: Tangent(g9,g19) = 1.5708
    c: Equal(g15,g14)
    c: Symmetric(g11,g11,g13)
    c: Equal(g18,g19)
    c: Equal(g19,g16)
    c: Equal(g16,g17)
    c: PointOnObject(g20,g-2)
    c: PointOnObject(g20,g7)
    c: Coincident(g4,g8)
    c: Coincident(g4,g9)
    c: Coincident(g3,g6)
    c: Coincident(g3,g5)
    c: DistanceX(g2,g2) = 87
    c: Symmetric(g0,g0,g2)
    c: Symmetric(g1,g1,g2)
    c: Radius(g19) = 7
    c: DistanceY(g20,g11) = 170
    c: Radius(g15) = 5
    c: DistanceX(g11,g11) = 50
    c: Equal(g9,g8)
    c: Equal(g9,g6)
    c: Coincident(g21,g7)
    c: PointOnObject(g20,g21)
    c: Diameter(g21) = 225
    c: Vertical(g22)
    c: Vertical(g23)
    c: Vertical(g24)
    c: Vertical(g25)
    c: Equal(g5,g8)
    c: Equal(g10,g12)
    c: Tangent(g7,g26) = -1.5708
    c: Tangent(g23,g26) = 1.5708
    c: Tangent(g23,g27) = 1.5708
    c: Tangent(g6,g27) = 1.5708
    c: Tangent(g7,g28) = -1.5708
    c: Tangent(g24,g28) = 1.5708
    c: Tangent(g24,g29) = 1.5708
    c: Tangent(g5,g29) = -1.5708
    c: Equal(g29,g27)
    c: Radius(g27) = 2
    c: Equal(g26,g28)
    c: Radius(g26) = 2
    c: Tangent(g9,g30) = -1.5708
    c: Tangent(g22,g30) = -1.5708
    c: Tangent(g22,g31) = -1.5708
    c: Tangent(g12,g31) = 1.5708
    c: Tangent(g8,g32) = 1.5708
    c: Tangent(g25,g32) = 1.5708
    c: Tangent(g10,g33) = 1.5708
    c: Tangent(g25,g33) = 1.5708
    c: Equal(g30,g32)
    c: Equal(g31,g33)
    c: DistanceY(g23,g23) = 2
    c: DistanceY(g22,g22) = 15
    c: DistanceY(g6,g9) = 48
    c: DistanceX(g24,g23) = 155
    c: Radius(g30) = 2
    c: Radius(g31) = 2
    c: Coincident(g34,g22)
    c: Coincident(g34,g23)
    c: Coincident(g35,g25)
    c: Coincident(g35,g24)
    c: Horizontal(g36)
    c: PointOnObject(g37,g13)
    c: DistanceY(g37,g13) = 14
    c: Vertical(g39)
    c: Vertical(g41)
    c: Horizontal(g42)
    c: Parallel(g40,g12)
    c: PointOnObject(g43,g-2)
    c: Tangent(g38,g44) = -1.5708
    c: Tangent(g36,g44) = 1.5708
    c: Tangent(g40,g45) = 1.5708
    c: Tangent(g36,g45) = 1.5708
    c: Tangent(g41,g46) = 1.5708
    c: Tangent(g40,g46) = 1.5708
    c: Tangent(g39,g47) = -1.5708
    c: Tangent(g38,g47) = -1.5708
    c: Tangent(g41,g48) = 1.5708
    c: Tangent(g39,g49) = -1.5708
    c: Coincident(g42,g39)
    c: Coincident(g42,g41)
    c: Equal(g15,g45)
    c: Equal(g45,g44)
    c: Symmetric(g36,g36,g37)
    c: Equal(g31,g46)
    c: Equal(g26,g48)
    c: Equal(g49,g29)
    c: Equal(g47,g32)
    c: DistanceY(g20,g43) = 14
    c: DistanceX(g41,g22) = 14
    c: PointOnObject(g50,g38)
    c: Perpendicular(g38,g50)
    c: Distance(g50) = 14
    c: Coincident(g50,g10)
    c: DistanceX(g24,g39) = 14
    c: Coincident(g51,g7)
    c: Coincident(g51,g49)
    c: Coincident(g51,g48)
    c: Tangent(g48,g51)
    c: PointOnObject(g43,g51)
    c: Tangent(g49,g51)
FEATURE [PartDesign::AdditiveLoft] AdditiveLoft  label="Shell_Angle_Ext"
  BaseFeature = -> Pad001
  Closed = false
  Profile = -> Sketch002
  Ruled = false
  Sections = -> [Sketch003]
FEATURE [PartDesign::Plane] DatumPlane002  label="Datum_BaseBrack"
  AttachmentOffset = pos=(0,0,7.5) rot=(0,0,1;0rad)
  Length = 187.44
  MapMode = 5
  Placement = pos=(0,0,7.5) rot=(0,0,1;0rad)
  ResizeMode = 0
  Support = -> [XY_Plane002]
  Width = 202.177
  expr: .AttachmentOffset.Base.z = Spreadsheet.shell_foot_height
FEATURE [PartDesign::Plane] DatumPlane003  label="Datum_TopBrack"
  AttachmentOffset = pos=(0,0,35) rot=(0,0,1;0rad)
  Length = 187.44
  MapMode = 5
  Placement = pos=(0,0,35) rot=(0,0,1;0rad)
  ResizeMode = 0
  Support = -> [XY_Plane002]
  Width = 202.177
  expr: .AttachmentOffset.Base.z = Spreadsheet.shell_totheight - Spreadsheet.shell_topbrack_vertheight
FEATURE [Sketcher::SketchObject] Sketch004  label="Sketch_WheelClear"
  FullyConstrained = true
  MapMode = 5
  Placement = pos=(0,0,0) rot=(0.57735,0.57735,0.57735;2.0944rad)
  Support = -> [YZ_Plane002]
  expr: Constraints[11] = <<params>>.wheel_well_vert
  expr: Constraints[13] = <<params>>.wheel_well_clearance
  sketch-geometry (5):
    g0: LineSegment StartX=-24 StartY=0 StartZ=0 EndX=24 EndY=0 EndZ=0
    g1: LineSegment StartX=-24 StartY=0 StartZ=0 EndX=-24 EndY=7 EndZ=0
    g2: LineSegment StartX=24 StartY=0 StartZ=0 EndX=24 EndY=7 EndZ=0
    g3: ArcOfCircle CenterX=-1.5e-15 CenterY=7 CenterZ=0 NormalX=0 NormalY=0 NormalZ=1 AngleXU=0 Radius=24 StartAngle=0 EndAngle=3.14159
    g4: LineSegment StartX=-24 StartY=7 StartZ=0 EndX=24 EndY=7 EndZ=0
  constraints (14):
    c: Horizontal(g0)
    c: Symmetric(g0,g0,g-1)
    c: Coincident(g1,g0)
    c: Vertical(g1)
    c: Coincident(g2,g0)
    c: Vertical(g2)
    c: Coincident(g3,g1)
    c: Coincident(g3,g2)
    c: Coincident(g4,g1)
    c: Coincident(g4,g2)
    c: PointOnObject(g3,g4)
    c: DistanceY(g0,g2) = 7
    c: Horizontal(g4)
    c: DistanceX(g1,g2) = 48
FEATURE [PartDesign::Pocket] Pocket  label="Wheel_Clear_Pocket"
  BaseFeature = -> AdditiveLoft
  Length = 5
  Length2 = 100
  Midplane = true
  Profile = -> Sketch004
  Type = 1
FEATURE [Sketcher::SketchObject] Sketch005  label="Sketch_Shell_Inner_CutFeet"
  FullyConstrained = true
  MapMode = 5
  Support = -> [XY_Plane002]
  expr: Constraints[78] = <<params>>.wheel_well_clearance
  expr: Constraints[42] = <<params>>.tail_width
  expr: Constraints[151] = <<params>>.shell_wall_thick
  expr: Constraints[47] = <<params>>.front_diameter
  expr: Constraints[81] = <<params>>.std_rad
  expr: Constraints[102] = <<params>>.shell_wall_thick
  expr: Constraints[96] = <<params>>.shell_wall_thick
  expr: Constraints[36] = <<params>>.wheel_well_plate_width
  expr: Constraints[63] = <<params>>.std_rad
  expr: Constraints[65] = <<params>>.std_rad
  expr: Constraints[40] = <<params>>.plate_length
  expr: Constraints[124] = Spreadsheet.shell_footside_width
  expr: Constraints[190] = <<params>>.shell_footback_width
  expr: Constraints[76] = <<params>>.front_vert_edge
  expr: Constraints[95] = <<params>>.shell_wall_thick
  expr: Constraints[79] = <<params>>.plate_width
  expr: Constraints[93] = <<params>>.shell_wall_thick
  expr: Constraints[41] = <<params>>.tail_rad
  expr: Constraints[80] = <<params>>.std_rad
  expr: Constraints[119] = <<params>>.std_rad / 2
  expr: Constraints[162] = <<params>>.std_rad / 2
  expr: Constraints[92] = <<params>>.shell_wall_thick
  expr: Constraints[77] = <<params>>.back_vert_edge
  expr: Constraints[175] = <<params>>.shell_footback_loc
  sketch-geometry (77):
    g0: LineSegment StartX=-57.5 StartY=17 StartZ=0 EndX=-57.5 EndY=-17 EndZ=0
    g1: LineSegment StartX=57.5 StartY=17 StartZ=0 EndX=57.5 EndY=-17 EndZ=0
    g2: LineSegment StartX=-57.5 StartY=0 StartZ=0 EndX=57.5 EndY=0 EndZ=0
    g3: LineSegment StartX=-64.5 StartY=-24 StartZ=0 EndX=64.5 EndY=-24 EndZ=0
    g4: LineSegment StartX=-64.5 StartY=24 StartZ=0 EndX=64.5 EndY=24 EndZ=0
    g5: LineSegment StartX=-64.5 StartY=-24 StartZ=0 EndX=-75.5 EndY=-24 EndZ=0
    g6: LineSegment StartX=64.5 StartY=-24 StartZ=0 EndX=75.5 EndY=-24 EndZ=0
    g7: ArcOfCircle CenterX=0 CenterY=52.6846 CenterZ=0 NormalX=0 NormalY=0 NormalZ=1 AngleXU=0 Radius=112.5 StartAngle=3.96017 EndAngle=5.4646
    g8: LineSegment StartX=-64.5 StartY=24 StartZ=0 EndX=-75.5 EndY=24 EndZ=0
    g9: LineSegment StartX=64.5 StartY=24 StartZ=0 EndX=75.5 EndY=24 EndZ=0
    g10: LineSegment StartX=-77.1162 StartY=42.1781 StartZ=0 EndX=-29.0404 EndY=108.13 EndZ=0
    g11: LineSegment StartX=-25 StartY=110.185 StartZ=0 EndX=25 EndY=110.185 EndZ=0
    g12: LineSegment StartX=29.0404 StartY=108.13 StartZ=0 EndX=77.1162 EndY=42.1781 EndZ=0
    g13: LineSegment StartX=0 StartY=0 StartZ=0 EndX=0 EndY=110.185 EndZ=0
    g14: ArcOfCircle CenterX=-25 CenterY=105.185 CenterZ=0 NormalX=0 NormalY=0 NormalZ=1 AngleXU=0 Radius=5 StartAngle=1.5708 EndAngle=2.5117
    g15: ArcOfCircle CenterX=25 CenterY=105.185 CenterZ=0 NormalX=0 NormalY=0 NormalZ=1 AngleXU=0 Radius=5 StartAngle=0.629894 EndAngle=1.5708
    g16: ArcOfCircle CenterX=-64.5 CenterY=17 CenterZ=0 NormalX=0 NormalY=0 NormalZ=1 AngleXU=0 Radius=7 StartAngle=1e-16 EndAngle=1.5708
    g17: ArcOfCircle CenterX=-64.5 CenterY=-17 CenterZ=0 NormalX=0 NormalY=0 NormalZ=1 AngleXU=0 Radius=7 StartAngle=4.71239 EndAngle=6.28319
    g18: ArcOfCircle CenterX=64.5 CenterY=-17 CenterZ=0 NormalX=0 NormalY=0 NormalZ=1 AngleXU=0 Radius=7 StartAngle=3.14159 EndAngle=4.71239
    g19: ArcOfCircle CenterX=64.5 CenterY=17 CenterZ=0 NormalX=0 NormalY=0 NormalZ=1 AngleXU=0 Radius=7 StartAngle=1.5708 EndAngle=3.14159
    g20: GeomPoint X=0 Y=-59.8154 Z=0
    g21: Circle CenterX=0 CenterY=52.6846 CenterZ=0 NormalX=0 NormalY=0 NormalZ=1 AngleXU=0 Radius=112.5
    g22: LineSegment StartX=77.5 StartY=26 StartZ=0 EndX=77.5 EndY=41 EndZ=0
    g23: LineSegment StartX=77.5 StartY=-26 StartZ=0 EndX=77.5 EndY=-28 EndZ=0
    g24: LineSegment StartX=-77.5 StartY=-28 StartZ=0 EndX=-77.5 EndY=-26 EndZ=0
    g25: LineSegment StartX=-77.5 StartY=26 StartZ=0 EndX=-77.5 EndY=41 EndZ=0
    g26: ArcOfCircle CenterX=75.5 CenterY=-28 CenterZ=0 NormalX=0 NormalY=0 NormalZ=1 AngleXU=0 Radius=2 StartAngle=5.4646 EndAngle=6.28319
    g27: ArcOfCircle CenterX=75.5 CenterY=-26 CenterZ=0 NormalX=0 NormalY=0 NormalZ=1 AngleXU=0 Radius=2 StartAngle=0 EndAngle=1.5708
    g28: ArcOfCircle CenterX=-75.5 CenterY=-28 CenterZ=0 NormalX=0 NormalY=0 NormalZ=1 AngleXU=0 Radius=2 StartAngle=3.14159 EndAngle=3.96017
    g29: ArcOfCircle CenterX=-75.5 CenterY=-26 CenterZ=0 NormalX=0 NormalY=0 NormalZ=1 AngleXU=0 Radius=2 StartAngle=1.5708 EndAngle=3.14159
    g30: ArcOfCircle CenterX=75.5 CenterY=26 CenterZ=0 NormalX=0 NormalY=0 NormalZ=1 AngleXU=0 Radius=2 StartAngle=4.71239 EndAngle=6.28319
    g31: ArcOfCircle CenterX=75.5 CenterY=41 CenterZ=0 NormalX=0 NormalY=0 NormalZ=1 AngleXU=0 Radius=2 StartAngle=1.2e-15 EndAngle=0.629894
    g32: ArcOfCircle CenterX=-75.5 CenterY=26 CenterZ=0 NormalX=0 NormalY=0 NormalZ=1 AngleXU=0 Radius=2 StartAngle=3.14159 EndAngle=4.71239
    g33: ArcOfCircle CenterX=-75.5 CenterY=41 CenterZ=0 NormalX=0 NormalY=0 NormalZ=1 AngleXU=0 Radius=2 StartAngle=2.5117 EndAngle=3.14159
    g34: LineSegment StartX=77.5 StartY=26 StartZ=0 EndX=77.5 EndY=-26 EndZ=0
    g35: LineSegment StartX=-77.5 StartY=26 StartZ=0 EndX=-77.5 EndY=-26 EndZ=0
    g36: ArcOfCircle CenterX=0 CenterY=52.6846 CenterZ=0 NormalX=0 NormalY=0 NormalZ=1 AngleXU=0 Radius=110.5 StartAngle=4.04818 EndAngle=5.3766
    g37: GeomPoint X=0 Y=-57.8154 Z=0
    g38: LineSegment StartX=-75.5 StartY=-24 StartZ=0 EndX=-75.5 EndY=24 EndZ=0
    g39: LineSegment StartX=-23.9829 StartY=108.185 StartZ=0 EndX=23.9829 EndY=108.185 EndZ=0
    g40: LineSegment StartX=-68.3081 StartY=50.8661 StartZ=0 EndX=-43.5911 EndY=84.7736 EndZ=0
    g41: LineSegment StartX=75.5 StartY=-24 StartZ=0 EndX=75.5 EndY=24 EndZ=0
    g42: LineSegment StartX=43.5911 StartY=84.7736 StartZ=0 EndX=68.3081 EndY=50.8661 EndZ=0
    g43: GeomPoint X=0 Y=108.185 Z=0
    g44: LineSegment StartX=-29.0404 StartY=108.13 StartZ=0 EndX=-27.4243 EndY=106.952 EndZ=0
    g45: LineSegment StartX=75.5 StartY=-24 StartZ=0 EndX=69.5 EndY=-24 EndZ=0
    g46: LineSegment StartX=68.5 StartY=-25 StartZ=0 EndX=68.5 EndY=-33.5361 EndZ=0
    g47: ArcOfCircle CenterX=69.5 CenterY=-25 CenterZ=0 NormalX=0 NormalY=0 NormalZ=1 AngleXU=0 Radius=1 StartAngle=1.5708 EndAngle=3.14159
    g48: ArcOfCircle CenterX=67.5 CenterY=-33.5361 CenterZ=0 NormalX=0 NormalY=0 NormalZ=1 AngleXU=0 Radius=1 StartAngle=5.3766 EndAngle=6.28319
    g49: LineSegment StartX=-75.5 StartY=-24 StartZ=0 EndX=-69.5 EndY=-24 EndZ=0
    g50: LineSegment StartX=-68.5 StartY=-25 StartZ=0 EndX=-68.5 EndY=-33.5361 EndZ=0
    g51: ArcOfCircle CenterX=-69.5 CenterY=-25 CenterZ=0 NormalX=0 NormalY=0 NormalZ=1 AngleXU=0 Radius=1 StartAngle=1e-16 EndAngle=1.5708
    g52: ArcOfCircle CenterX=-67.5 CenterY=-33.5361 CenterZ=0 NormalX=0 NormalY=0 NormalZ=1 AngleXU=0 Radius=1 StartAngle=3.14159 EndAngle=4.04818
    g53: LineSegment StartX=75.5 StartY=24 StartZ=0 EndX=69.5 EndY=24 EndZ=0
    g54: LineSegment StartX=68.5 StartY=25 StartZ=0 EndX=68.5 EndY=50.277 EndZ=0
    g55: ArcOfCircle CenterX=69.5 CenterY=25 CenterZ=0 NormalX=0 NormalY=0 NormalZ=1 AngleXU=0 Radius=1 StartAngle=3.14159 EndAngle=4.71239
    g56: ArcOfCircle CenterX=67.5 CenterY=50.277 CenterZ=0 NormalX=0 NormalY=0 NormalZ=1 AngleXU=0 Radius=1 StartAngle=-2.7e-15 EndAngle=0.629894
    g57: LineSegment StartX=-75.5 StartY=24 StartZ=0 EndX=-69.5 EndY=24 EndZ=0
    g58: LineSegment StartX=-68.5 StartY=25 StartZ=0 EndX=-68.5 EndY=50.277 EndZ=0
    g59: ArcOfCircle CenterX=-67.5 CenterY=50.277 CenterZ=0 NormalX=0 NormalY=0 NormalZ=1 AngleXU=0 Radius=1 StartAngle=2.5117 EndAngle=3.14159
    g60: ArcOfCircle CenterX=-69.5 CenterY=25 CenterZ=0 NormalX=0 NormalY=0 NormalZ=1 AngleXU=0 Radius=1 StartAngle=4.71239 EndAngle=6.28319
    g61: LineSegment StartX=-33.783 StartY=85.1846 StartZ=0 EndX=-42.783 EndY=85.1846 EndZ=0
    g62: LineSegment StartX=33.783 StartY=85.1846 StartZ=0 EndX=42.783 EndY=85.1846 EndZ=0
    g63: LineSegment StartX=27.4243 StartY=106.952 StartZ=0 EndX=29.0404 EndY=108.13 EndZ=0
    g64: ArcOfCircle CenterX=-33.783 CenterY=86.1846 CenterZ=0 NormalX=0 NormalY=0 NormalZ=1 AngleXU=0 Radius=1 StartAngle=4.71239 EndAngle=6.28319
    g65: ArcOfCircle CenterX=-42.783 CenterY=84.1846 CenterZ=0 NormalX=0 NormalY=0 NormalZ=1 AngleXU=0 Radius=1 StartAngle=1.5708 EndAngle=2.5117
    g66: ArcOfCircle CenterX=33.783 CenterY=86.1846 CenterZ=0 NormalX=0 NormalY=0 NormalZ=1 AngleXU=0 Radius=1 StartAngle=3.14159 EndAngle=4.71239
    g67: ArcOfCircle CenterX=42.783 CenterY=84.1846 CenterZ=0 NormalX=0 NormalY=0 NormalZ=1 AngleXU=0 Radius=1 StartAngle=0.629894 EndAngle=1.5708
    g68: LineSegment StartX=32.783 StartY=86.1846 StartZ=0 EndX=32.783 EndY=99.2747 EndZ=0
    g69: LineSegment StartX=32.5911 StartY=99.8638 StartZ=0 EndX=28.0234 EndY=106.13 EndZ=0
    g70: ArcOfCircle CenterX=31.783 CenterY=99.2747 CenterZ=0 NormalX=0 NormalY=0 NormalZ=1 AngleXU=0 Radius=1 StartAngle=7e-15 EndAngle=0.629894
    g71: ArcOfCircle CenterX=-23.9829 CenterY=103.185 CenterZ=0 NormalX=0 NormalY=0 NormalZ=1 AngleXU=0 Radius=5 StartAngle=1.5708 EndAngle=2.5117
    g72: ArcOfCircle CenterX=23.9829 CenterY=103.185 CenterZ=0 NormalX=0 NormalY=0 NormalZ=1 AngleXU=0 Radius=5 StartAngle=0.629894 EndAngle=1.5708
    g73: LineSegment StartX=-32.783 StartY=86.1846 StartZ=0 EndX=-32.783 EndY=99.2747 EndZ=0
    g74: LineSegment StartX=-32.5911 StartY=99.8638 StartZ=0 EndX=-28.0234 EndY=106.13 EndZ=0
    g75: ArcOfCircle CenterX=-31.783 CenterY=99.2747 CenterZ=0 NormalX=0 NormalY=0 NormalZ=1 AngleXU=0 Radius=1 StartAngle=2.5117 EndAngle=3.14159
    g76: LineSegment StartX=-32.783 StartY=86.1846 StartZ=0 EndX=32.783 EndY=86.1846 EndZ=0
  constraints (193):
    c: Vertical(g0)
    c: Vertical(g1)
    c: Horizontal(g2)
    c: Symmetric(g2,g2,g-1)
    c: Horizontal(g3)
    c: Horizontal(g5)
    c: Horizontal(g6)
    c: PointOnObject(g7,g-2)
    c: Horizontal(g8)
    c: Horizontal(g9)
    c: Horizontal(g11)
    c: Coincident(g13,g-1)
    c: PointOnObject(g13,g-2)
    c: Tangent(g10,g14) = 1.5708
    c: Tangent(g11,g14) = 1.5708
    c: Tangent(g11,g15) = 1.5708
    c: Tangent(g12,g15) = 1.5708
    c: Tangent(g8,g16) = -1.5708
    c: Tangent(g0,g16) = 1.5708
    c: Tangent(g5,g17) = 1.5708
    c: Tangent(g0,g17) = 1.5708
    c: Tangent(g1,g18) = -1.5708
    c: Tangent(g6,g18) = -1.5708
    c: Tangent(g1,g19) = -1.5708
    c: Tangent(g9,g19) = 1.5708
    c: Equal(g15,g14)
    c: Symmetric(g11,g11,g13)
    c: Equal(g18,g19)
    c: Equal(g19,g16)
    c: Equal(g16,g17)
    c: PointOnObject(g20,g-2)
    c: PointOnObject(g20,g7)
    c: Coincident(g4,g8)
    c: Coincident(g4,g9)
    c: Coincident(g3,g6)
    c: Coincident(g3,g5)
    c: DistanceX(g2,g2) = 115
    c: Symmetric(g0,g0,g2)
    c: Symmetric(g1,g1,g2)
    c: Radius(g19) = 7
    c: DistanceY(g20,g11) = 170
    c: Radius(g15) = 5
    c: DistanceX(g11,g11) = 50
    c: Equal(g9,g8)
    c: Equal(g9,g6)
    c: Coincident(g21,g7)
    c: PointOnObject(g20,g21)
    c: Diameter(g21) = 225
    c: Vertical(g22)
    c: Vertical(g23)
    c: Vertical(g24)
    c: Vertical(g25)
    c: Equal(g5,g8)
    c: Equal(g10,g12)
    c: Tangent(g7,g26) = -1.5708
    c: Tangent(g23,g26) = 1.5708
    c: Tangent(g23,g27) = 1.5708
    c: Tangent(g6,g27) = 1.5708
    c: Tangent(g7,g28) = -1.5708
    c: Tangent(g24,g28) = 1.5708
    c: Tangent(g24,g29) = 1.5708
    c: Tangent(g5,g29) = -1.5708
    c: Equal(g29,g27)
    c: Radius(g27) = 2
    c: Equal(g26,g28)
    c: Radius(g26) = 2
    c: Tangent(g9,g30) = -1.5708
    c: Tangent(g22,g30) = -1.5708
    c: Tangent(g22,g31) = -1.5708
    c: Tangent(g12,g31) = 1.5708
    c: Tangent(g8,g32) = 1.5708
    c: Tangent(g25,g32) = 1.5708
    c: Tangent(g10,g33) = 1.5708
    c: Tangent(g25,g33) = 1.5708
    c: Equal(g30,g32)
    c: Equal(g31,g33)
    c: DistanceY(g23,g23) = 2
    c: DistanceY(g22,g22) = 15
    c: DistanceY(g6,g9) = 48
    c: DistanceX(g24,g23) = 155
    c: Radius(g30) = 2
    c: Radius(g31) = 2
    c: Coincident(g34,g22)
    c: Coincident(g34,g23)
    c: Coincident(g35,g25)
    c: Coincident(g35,g24)
    c: PointOnObject(g37,g-2)
    c: PointOnObject(g37,g36)
    c: Vertical(g38)
    c: Horizontal(g39)
    c: Vertical(g41)
    c: PointOnObject(g43,g13)
    c: DistanceY(g20,g37) = 2
    c: DistanceY(g43,g13) = 2
    c: Parallel(g42,g12)
    c: DistanceX(g41,g22) = 2
    c: DistanceX(g25,g38) = 2
    c: Parallel(g40,g10)
    c: PointOnObject(g44,g10)
    c: PointOnObject(g44,g40)
    c: Perpendicular(g44,g10)
    c: PointOnObject(g10,g44)
    c: Distance(g44) = 2
    c: Coincident(g45,g6)
    c: Vertical(g46)
    c: PointOnObject(g41,g45)
    c: Tangent(g46,g47) = -1.5708
    c: Tangent(g45,g47) = -1.5708
    c: Tangent(g46,g48) = 1.5708
    c: Tangent(g36,g48) = -1.5708
    c: PointOnObject(g38,g5)
    c: Coincident(g49,g38)
    c: Vertical(g50)
    c: Tangent(g49,g51) = 1.5708
    c: Tangent(g50,g51) = 1.5708
    c: Tangent(g36,g52) = -1.5708
    c: Tangent(g50,g52) = -1.5708
    c: Equal(g49,g45)
    c: Horizontal(g45)
    c: Radius(g47) = 1
    c: Horizontal(g49)
    c: Equal(g51,g52)
    c: Equal(g52,g47)
    c: Equal(g47,g48)
    c: DistanceX(g46,g41) = 7
    c: PointOnObject(g41,g9)
    c: Coincident(g53,g41)
    c: Vertical(g54)
    c: Tangent(g53,g55) = 1.5708
    c: Tangent(g54,g55) = 1.5708
    c: Tangent(g54,g56) = -1.5708
    c: Tangent(g42,g56) = 1.5708
    c: Equal(g47,g55)
    c: Horizontal(g53)
    c: Equal(g56,g55)
    c: Equal(g53,g45)
    c: PointOnObject(g38,g8)
    c: Coincident(g57,g38)
    c: Vertical(g58)
    c: Tangent(g58,g59) = 1.5708
    c: Tangent(g40,g59) = 1.5708
    c: Tangent(g57,g60) = -1.5708
    c: Tangent(g58,g60) = -1.5708
    c: Equal(g51,g60)
    c: Horizontal(g57)
    c: Equal(g60,g59)
    c: Equal(g57,g49)
    c: Horizontal(g61)
    c: Horizontal(g62)
    c: PointOnObject(g63,g42)
    c: Perpendicular(g42,g63)
    c: Distance(g63) = 2
    c: Coincident(g63,g12)
    c: Tangent(g61,g64) = 1.5708
    c: Tangent(g61,g65) = -1.5708
    c: Tangent(g40,g65) = 1.5708
    c: Tangent(g62,g66) = -1.5708
    c: Tangent(g62,g67) = 1.5708
    c: Tangent(g42,g67) = 1.5708
    c: Equal(g64,g66)
    c: Equal(g67,g66)
    c: Equal(g65,g64)
    c: Radius(g67) = 1
    c: Coincident(g68,g66)
    c: Vertical(g68)
    c: Tangent(g66,g68)
    c: Parallel(g12,g69)
    c: Tangent(g68,g70) = -1.5708
    c: Tangent(g69,g70) = -1.5708
    c: Equal(g70,g66)
    c: Tangent(g39,g71) = 1.5708
    c: Tangent(g39,g72) = 1.5708
    c: Tangent(g69,g72) = -1.5708
    c: Equal(g72,g15)
    c: PointOnObject(g63,g69)
    c: DistanceY(g62,g11) = 25
    c: Coincident(g73,g64)
    c: Vertical(g73)
    c: Tangent(g64,g73)
    c: Coincident(g74,g71)
    c: Tangent(g74,g71)
    c: Tangent(g73,g75) = 1.5708
    c: Tangent(g74,g75) = 1.5708
    c: Equal(g64,g75)
    c: Equal(g71,g14)
    c: Parallel(g74,g10)
    c: Equal(g73,g68)
    c: Coincident(g76,g64)
    c: Coincident(g76,g66)
    c: Symmetric(g39,g39,g43)
    c: DistanceX(g66,g62) = 10
    c: Coincident(g36,g7)
    c: Horizontal(g76)
FEATURE [Sketcher::SketchObject] Sketch006  label="Sketch_Shell_Inner_AboveFeet_Top"
  FullyConstrained = true
  MapMode = 5
  Placement = pos=(0,0,10) rot=(0,0,1;0rad)
  Support = -> [DatumPlane001]
  expr: Constraints[109] = <<params>>.std_rad
  expr: Constraints[81] = <<params>>.std_rad
  expr: Constraints[116] = <<params>>.shell_wall_thick
  expr: Constraints[77] = <<params>>.back_vert_edge
  expr: Constraints[111] = <<params>>.shell_wall_thick
  expr: Constraints[41] = <<params>>.tail_rad
  expr: Constraints[112] = <<params>>.tail_rad
  expr: Constraints[80] = <<params>>.std_rad
  expr: Constraints[118] = <<params>>.front_diameter
  expr: Constraints[76] = <<params>>.front_vert_edge
  expr: Constraints[115] = <<params>>.shell_wall_thick
  expr: Constraints[63] = <<params>>.std_rad
  expr: Constraints[47] = <<params>>.front_diameter
  expr: Constraints[36] = <<params>>.wheel_well_plate_width
  expr: Constraints[79] = <<params>>.plate_width
  expr: Constraints[105] = <<params>>.shell_wall_thick
  expr: Constraints[42] = <<params>>.tail_width
  expr: Constraints[78] = <<params>>.wheel_well_clearance
  expr: Constraints[65] = <<params>>.std_rad
  expr: Constraints[40] = <<params>>.plate_length
  expr: Constraints[122] = <<params>>.shell_wall_thick
  sketch-geometry (51):
    g0: LineSegment StartX=-57.5 StartY=17 StartZ=0 EndX=-57.5 EndY=-17 EndZ=0
    g1: LineSegment StartX=57.5 StartY=17 StartZ=0 EndX=57.5 EndY=-17 EndZ=0
    g2: LineSegment StartX=-57.5 StartY=0 StartZ=0 EndX=57.5 EndY=0 EndZ=0
    g3: LineSegment StartX=-64.5 StartY=-24 StartZ=0 EndX=64.5 EndY=-24 EndZ=0
    g4: LineSegment StartX=-64.5 StartY=24 StartZ=0 EndX=64.5 EndY=24 EndZ=0
    g5: LineSegment StartX=-64.5 StartY=-24 StartZ=0 EndX=-75.5 EndY=-24 EndZ=0
    g6: LineSegment StartX=64.5 StartY=-24 StartZ=0 EndX=75.5 EndY=-24 EndZ=0
    g7: ArcOfCircle CenterX=0 CenterY=52.6846 CenterZ=0 NormalX=0 NormalY=0 NormalZ=1 AngleXU=0 Radius=112.5 StartAngle=3.96017 EndAngle=5.4646
    g8: LineSegment StartX=-64.5 StartY=24 StartZ=0 EndX=-75.5 EndY=24 EndZ=0
    g9: LineSegment StartX=64.5 StartY=24 StartZ=0 EndX=75.5 EndY=24 EndZ=0
    g10: LineSegment StartX=-77.1162 StartY=42.1781 StartZ=0 EndX=-29.0404 EndY=108.13 EndZ=0
    g11: LineSegment StartX=-25 StartY=110.185 StartZ=0 EndX=25 EndY=110.185 EndZ=0
    g12: LineSegment StartX=29.0404 StartY=108.13 StartZ=0 EndX=77.1162 EndY=42.1781 EndZ=0
    g13: LineSegment StartX=0 StartY=0 StartZ=0 EndX=0 EndY=110.185 EndZ=0
    g14: ArcOfCircle CenterX=-25 CenterY=105.185 CenterZ=0 NormalX=0 NormalY=0 NormalZ=1 AngleXU=0 Radius=5 StartAngle=1.5708 EndAngle=2.5117
    g15: ArcOfCircle CenterX=25 CenterY=105.185 CenterZ=0 NormalX=0 NormalY=0 NormalZ=1 AngleXU=0 Radius=5 StartAngle=0.629894 EndAngle=1.5708
    g16: ArcOfCircle CenterX=-64.5 CenterY=17 CenterZ=0 NormalX=0 NormalY=0 NormalZ=1 AngleXU=0 Radius=7 StartAngle=0 EndAngle=1.5708
    g17: ArcOfCircle CenterX=-64.5 CenterY=-17 CenterZ=0 NormalX=0 NormalY=0 NormalZ=1 AngleXU=0 Radius=7 StartAngle=4.71239 EndAngle=6.28319
    g18: ArcOfCircle CenterX=64.5 CenterY=-17 CenterZ=0 NormalX=0 NormalY=0 NormalZ=1 AngleXU=0 Radius=7 StartAngle=3.14159 EndAngle=4.71239
    g19: ArcOfCircle CenterX=64.5 CenterY=17 CenterZ=0 NormalX=0 NormalY=0 NormalZ=1 AngleXU=0 Radius=7 StartAngle=1.5708 EndAngle=3.14159
    g20: GeomPoint X=0 Y=-59.8154 Z=0
    g21: Circle CenterX=0 CenterY=52.6846 CenterZ=0 NormalX=0 NormalY=0 NormalZ=1 AngleXU=0 Radius=112.5
    g22: LineSegment StartX=77.5 StartY=26 StartZ=0 EndX=77.5 EndY=41 EndZ=0
    g23: LineSegment StartX=77.5 StartY=-26 StartZ=0 EndX=77.5 EndY=-28 EndZ=0
    g24: LineSegment StartX=-77.5 StartY=-28 StartZ=0 EndX=-77.5 EndY=-26 EndZ=0
    g25: LineSegment StartX=-77.5 StartY=26 StartZ=0 EndX=-77.5 EndY=41 EndZ=0
    g26: ArcOfCircle CenterX=75.5 CenterY=-28 CenterZ=0 NormalX=0 NormalY=0 NormalZ=1 AngleXU=0 Radius=2 StartAngle=5.4646 EndAngle=6.28319
    g27: ArcOfCircle CenterX=75.5 CenterY=-26 CenterZ=0 NormalX=0 NormalY=0 NormalZ=1 AngleXU=0 Radius=2 StartAngle=0 EndAngle=1.5708
    g28: ArcOfCircle CenterX=-75.5 CenterY=-28 CenterZ=0 NormalX=0 NormalY=0 NormalZ=1 AngleXU=0 Radius=2 StartAngle=3.14159 EndAngle=3.96017
    g29: ArcOfCircle CenterX=-75.5 CenterY=-26 CenterZ=0 NormalX=0 NormalY=0 NormalZ=1 AngleXU=0 Radius=2 StartAngle=1.5708 EndAngle=3.14159
    g30: ArcOfCircle CenterX=75.5 CenterY=26 CenterZ=0 NormalX=0 NormalY=0 NormalZ=1 AngleXU=0 Radius=2 StartAngle=4.71239 EndAngle=6.28319
    g31: ArcOfCircle CenterX=75.5 CenterY=41 CenterZ=0 NormalX=0 NormalY=0 NormalZ=1 AngleXU=0 Radius=2 StartAngle=-1.8e-15 EndAngle=0.629894
    g32: ArcOfCircle CenterX=-75.5 CenterY=26 CenterZ=0 NormalX=0 NormalY=0 NormalZ=1 AngleXU=0 Radius=2 StartAngle=3.14159 EndAngle=4.71239
    g33: ArcOfCircle CenterX=-75.5 CenterY=41 CenterZ=0 NormalX=0 NormalY=0 NormalZ=1 AngleXU=0 Radius=2 StartAngle=2.5117 EndAngle=3.14159
    g34: LineSegment StartX=77.5 StartY=26 StartZ=0 EndX=77.5 EndY=-26 EndZ=0
    g35: LineSegment StartX=-77.5 StartY=26 StartZ=0 EndX=-77.5 EndY=-26 EndZ=0
    g36: ArcOfCircle CenterX=0 CenterY=54.6846 CenterZ=0 NormalX=0 NormalY=0 NormalZ=1 AngleXU=0 Radius=112.5 StartAngle=3.98468 EndAngle=5.44009
    g37: GeomPoint X=0 Y=-57.8154 Z=0
    g38: LineSegment StartX=-75.5 StartY=-27.826 StartZ=0 EndX=-75.5 EndY=40.3484 EndZ=0
    g39: LineSegment StartX=-23.9829 StartY=108.185 StartZ=0 EndX=23.9829 EndY=108.185 EndZ=0
    g40: LineSegment StartX=-75.1162 StartY=41.5265 StartZ=0 EndX=-28.0234 EndY=106.13 EndZ=0
    g41: LineSegment StartX=75.5 StartY=-27.826 StartZ=0 EndX=75.5 EndY=40.3484 EndZ=0
    g42: LineSegment StartX=28.0234 StartY=106.13 StartZ=0 EndX=75.1162 EndY=41.5265 EndZ=0
    g43: GeomPoint X=0 Y=108.185 Z=0
    g44: ArcOfCircle CenterX=-23.9829 CenterY=103.185 CenterZ=0 NormalX=0 NormalY=0 NormalZ=1 AngleXU=0 Radius=5 StartAngle=1.5708 EndAngle=2.5117
    g45: ArcOfCircle CenterX=23.9829 CenterY=103.185 CenterZ=0 NormalX=0 NormalY=0 NormalZ=1 AngleXU=0 Radius=5 StartAngle=0.629894 EndAngle=1.5708
    g46: ArcOfCircle CenterX=73.5 CenterY=40.3484 CenterZ=0 NormalX=0 NormalY=0 NormalZ=1 AngleXU=0 Radius=2 StartAngle=1.7e-15 EndAngle=0.629894
    g47: ArcOfCircle CenterX=-73.5 CenterY=40.3484 CenterZ=0 NormalX=0 NormalY=0 NormalZ=1 AngleXU=0 Radius=2 StartAngle=2.5117 EndAngle=3.14159
    g48: ArcOfCircle CenterX=-73.5 CenterY=-27.826 CenterZ=0 NormalX=0 NormalY=0 NormalZ=1 AngleXU=0 Radius=2 StartAngle=3.14159 EndAngle=3.98468
    g49: ArcOfCircle CenterX=73.5 CenterY=-27.826 CenterZ=0 NormalX=0 NormalY=0 NormalZ=1 AngleXU=0 Radius=2 StartAngle=5.44009 EndAngle=6.28319
    g50: LineSegment StartX=-29.0404 StartY=108.13 StartZ=0 EndX=-27.4243 EndY=106.952 EndZ=0
  constraints (123):
    c: Vertical(g0)
    c: Vertical(g1)
    c: Horizontal(g2)
    c: Symmetric(g2,g2,g-1)
    c: Horizontal(g3)
    c: Horizontal(g5)
    c: Horizontal(g6)
    c: PointOnObject(g7,g-2)
    c: Horizontal(g8)
    c: Horizontal(g9)
    c: Horizontal(g11)
    c: Coincident(g13,g-1)
    c: PointOnObject(g13,g-2)
    c: Tangent(g10,g14) = 1.5708
    c: Tangent(g11,g14) = 1.5708
    c: Tangent(g11,g15) = 1.5708
    c: Tangent(g12,g15) = 1.5708
    c: Tangent(g8,g16) = -1.5708
    c: Tangent(g0,g16) = 1.5708
    c: Tangent(g5,g17) = 1.5708
    c: Tangent(g0,g17) = 1.5708
    c: Tangent(g1,g18) = -1.5708
    c: Tangent(g6,g18) = -1.5708
    c: Tangent(g1,g19) = -1.5708
    c: Tangent(g9,g19) = 1.5708
    c: Equal(g15,g14)
    c: Symmetric(g11,g11,g13)
    c: Equal(g18,g19)
    c: Equal(g19,g16)
    c: Equal(g16,g17)
    c: PointOnObject(g20,g-2)
    c: PointOnObject(g20,g7)
    c: Coincident(g4,g8)
    c: Coincident(g4,g9)
    c: Coincident(g3,g6)
    c: Coincident(g3,g5)
    c: DistanceX(g2,g2) = 115
    c: Symmetric(g0,g0,g2)
    c: Symmetric(g1,g1,g2)
    c: Radius(g19) = 7
    c: DistanceY(g20,g11) = 170
    c: Radius(g15) = 5
    c: DistanceX(g11,g11) = 50
    c: Equal(g9,g8)
    c: Equal(g9,g6)
    c: Coincident(g21,g7)
    c: PointOnObject(g20,g21)
    c: Diameter(g21) = 225
    c: Vertical(g22)
    c: Vertical(g23)
    c: Vertical(g24)
    c: Vertical(g25)
    c: Equal(g5,g8)
    c: Equal(g10,g12)
    c: Tangent(g7,g26) = -1.5708
    c: Tangent(g23,g26) = 1.5708
    c: Tangent(g23,g27) = 1.5708
    c: Tangent(g6,g27) = 1.5708
    c: Tangent(g7,g28) = -1.5708
    c: Tangent(g24,g28) = 1.5708
    c: Tangent(g24,g29) = 1.5708
    c: Tangent(g5,g29) = -1.5708
    c: Equal(g29,g27)
    c: Radius(g27) = 2
    c: Equal(g26,g28)
    c: Radius(g26) = 2
    c: Tangent(g9,g30) = -1.5708
    c: Tangent(g22,g30) = -1.5708
    c: Tangent(g22,g31) = -1.5708
    c: Tangent(g12,g31) = 1.5708
    c: Tangent(g8,g32) = 1.5708
    c: Tangent(g25,g32) = 1.5708
    c: Tangent(g10,g33) = 1.5708
    c: Tangent(g25,g33) = 1.5708
    c: Equal(g30,g32)
    c: Equal(g31,g33)
    c: DistanceY(g23,g23) = 2
    c: DistanceY(g22,g22) = 15
    c: DistanceY(g6,g9) = 48
    c: DistanceX(g24,g23) = 155
    c: Radius(g30) = 2
    c: Radius(g31) = 2
    c: Coincident(g34,g22)
    c: Coincident(g34,g23)
    c: Coincident(g35,g25)
    c: Coincident(g35,g24)
    c: PointOnObject(g36,g13)
    c: PointOnObject(g37,g-2)
    c: PointOnObject(g37,g36)
    c: Vertical(g38)
    c: Horizontal(g39)
    c: Vertical(g41)
    c: PointOnObject(g43,g13)
    c: Tangent(g40,g44) = 1.5708
    c: Tangent(g39,g44) = 1.5708
    c: Tangent(g39,g45) = 1.5708
    c: Tangent(g42,g45) = 1.5708
    c: Tangent(g41,g46) = -1.5708
    c: Tangent(g42,g46) = 1.5708
    c: Tangent(g38,g47) = 1.5708
    c: Tangent(g40,g47) = 1.5708
    c: Tangent(g38,g48) = 1.5708
    c: Tangent(g36,g48) = -1.5708
    c: Tangent(g36,g49) = -1.5708
    c: Tangent(g41,g49) = -1.5708
    c: DistanceY(g20,g37) = 2
    c: Equal(g49,g46)
    c: Equal(g49,g48)
    c: Equal(g48,g47)
    c: Radius(g49) = 2
    c: Symmetric(g39,g39,g43)
    c: DistanceY(g43,g13) = 2
    c: Radius(g45) = 5
    c: Equal(g45,g44)
    c: Parallel(g42,g12)
    c: DistanceX(g41,g22) = 2
    c: DistanceX(g25,g38) = 2
    c: Parallel(g40,g10)
    c: Diameter(g36) = 225
    c: PointOnObject(g50,g40)
    c: Perpendicular(g40,g50)
    c: Coincident(g50,g10)
    c: Distance(g50) = 2
FEATURE [PartDesign::Pocket] Pocket001  label="Shell_Inner_FeetVertCut"
  BaseFeature = -> Pocket
  Length = 7.5
  Length2 = 100
  Profile = -> Sketch005
  Reversed = true
  Type = 0
  expr: Length = Spreadsheet.shell_foot_height
FEATURE [PartDesign::Plane] DatumPlane004  label="Datum_TopBrack_Angstart"
  AttachmentOffset = pos=(0,0,26) rot=(0,0,1;0rad)
  Length = 187.44
  MapMode = 5
  Placement = pos=(0,0,26) rot=(0,0,1;0rad)
  ResizeMode = 0
  Support = -> [XY_Plane002]
  Width = 202.177
  expr: .AttachmentOffset.Base.z = Spreadsheet.shell_totheight - Spreadsheet.shell_topbrack_vertheight - Spreadsheet.shell_topbrack_angleheight
FEATURE [Sketcher::SketchObject] Sketch007  label="Sketch_Shell_InnerMid_LoftStart"
  FullyConstrained = true
  MapMode = 5
  Placement = pos=(0,0,10) rot=(0,0,1;0rad)
  Support = -> [DatumPlane001]
  expr: Constraints[40] = <<params>>.plate_length
  expr: Constraints[65] = <<params>>.std_rad
  expr: Constraints[42] = <<params>>.tail_width
  expr: Constraints[78] = <<params>>.wheel_well_clearance
  expr: Constraints[105] = <<params>>.shell_wall_thick
  expr: Constraints[79] = <<params>>.plate_width
  expr: Constraints[36] = <<params>>.wheel_well_plate_width
  expr: Constraints[47] = <<params>>.front_diameter
  expr: Constraints[115] = <<params>>.shell_wall_thick
  expr: Constraints[63] = <<params>>.std_rad
  expr: Constraints[112] = <<params>>.tail_rad
  expr: Constraints[80] = <<params>>.std_rad
  expr: Constraints[41] = <<params>>.tail_rad
  expr: Constraints[111] = <<params>>.shell_wall_thick
  expr: Constraints[77] = <<params>>.back_vert_edge
  expr: Constraints[116] = <<params>>.shell_wall_thick
  expr: Constraints[109] = <<params>>.std_rad
  expr: Constraints[76] = <<params>>.front_vert_edge
  expr: Constraints[118] = <<params>>.front_diameter - <<params>>.shell_wall_thick * 2
  expr: Constraints[81] = <<params>>.std_rad
  expr: Constraints[122] = <<params>>.shell_wall_thick
  sketch-geometry (51):
    g0: LineSegment StartX=-57.5 StartY=17 StartZ=0 EndX=-57.5 EndY=-17 EndZ=0
    g1: LineSegment StartX=57.5 StartY=17 StartZ=0 EndX=57.5 EndY=-17 EndZ=0
    g2: LineSegment StartX=-57.5 StartY=0 StartZ=0 EndX=57.5 EndY=0 EndZ=0
    g3: LineSegment StartX=-64.5 StartY=-24 StartZ=0 EndX=64.5 EndY=-24 EndZ=0
    g4: LineSegment StartX=-64.5 StartY=24 StartZ=0 EndX=64.5 EndY=24 EndZ=0
    g5: LineSegment StartX=-64.5 StartY=-24 StartZ=0 EndX=-75.5 EndY=-24 EndZ=0
    g6: LineSegment StartX=64.5 StartY=-24 StartZ=0 EndX=75.5 EndY=-24 EndZ=0
    g7: ArcOfCircle CenterX=0 CenterY=52.6846 CenterZ=0 NormalX=0 NormalY=0 NormalZ=1 AngleXU=0 Radius=112.5 StartAngle=3.96017 EndAngle=5.4646
    g8: LineSegment StartX=-64.5 StartY=24 StartZ=0 EndX=-75.5 EndY=24 EndZ=0
    g9: LineSegment StartX=64.5 StartY=24 StartZ=0 EndX=75.5 EndY=24 EndZ=0
    g10: LineSegment StartX=-77.1162 StartY=42.1781 StartZ=0 EndX=-29.0404 EndY=108.13 EndZ=0
    g11: LineSegment StartX=-25 StartY=110.185 StartZ=0 EndX=25 EndY=110.185 EndZ=0
    g12: LineSegment StartX=29.0404 StartY=108.13 StartZ=0 EndX=77.1162 EndY=42.1781 EndZ=0
    g13: LineSegment StartX=0 StartY=0 StartZ=0 EndX=0 EndY=110.185 EndZ=0
    g14: ArcOfCircle CenterX=-25 CenterY=105.185 CenterZ=0 NormalX=0 NormalY=0 NormalZ=1 AngleXU=0 Radius=5 StartAngle=1.5708 EndAngle=2.5117
    g15: ArcOfCircle CenterX=25 CenterY=105.185 CenterZ=0 NormalX=0 NormalY=0 NormalZ=1 AngleXU=0 Radius=5 StartAngle=0.629894 EndAngle=1.5708
    g16: ArcOfCircle CenterX=-64.5 CenterY=17 CenterZ=0 NormalX=0 NormalY=0 NormalZ=1 AngleXU=0 Radius=7 StartAngle=0 EndAngle=1.5708
    g17: ArcOfCircle CenterX=-64.5 CenterY=-17 CenterZ=0 NormalX=0 NormalY=0 NormalZ=1 AngleXU=0 Radius=7 StartAngle=4.71239 EndAngle=6.28319
    g18: ArcOfCircle CenterX=64.5 CenterY=-17 CenterZ=0 NormalX=0 NormalY=0 NormalZ=1 AngleXU=0 Radius=7 StartAngle=3.14159 EndAngle=4.71239
    g19: ArcOfCircle CenterX=64.5 CenterY=17 CenterZ=0 NormalX=0 NormalY=0 NormalZ=1 AngleXU=0 Radius=7 StartAngle=1.5708 EndAngle=3.14159
    g20: GeomPoint X=0 Y=-59.8154 Z=0
    g21: Circle CenterX=0 CenterY=52.6846 CenterZ=0 NormalX=0 NormalY=0 NormalZ=1 AngleXU=0 Radius=112.5
    g22: LineSegment StartX=77.5 StartY=26 StartZ=0 EndX=77.5 EndY=41 EndZ=0
    g23: LineSegment StartX=77.5 StartY=-26 StartZ=0 EndX=77.5 EndY=-28 EndZ=0
    g24: LineSegment StartX=-77.5 StartY=-28 StartZ=0 EndX=-77.5 EndY=-26 EndZ=0
    g25: LineSegment StartX=-77.5 StartY=26 StartZ=0 EndX=-77.5 EndY=41 EndZ=0
    g26: ArcOfCircle CenterX=75.5 CenterY=-28 CenterZ=0 NormalX=0 NormalY=0 NormalZ=1 AngleXU=0 Radius=2 StartAngle=5.4646 EndAngle=6.28319
    g27: ArcOfCircle CenterX=75.5 CenterY=-26 CenterZ=0 NormalX=0 NormalY=0 NormalZ=1 AngleXU=0 Radius=2 StartAngle=0 EndAngle=1.5708
    g28: ArcOfCircle CenterX=-75.5 CenterY=-28 CenterZ=0 NormalX=0 NormalY=0 NormalZ=1 AngleXU=0 Radius=2 StartAngle=3.14159 EndAngle=3.96017
    g29: ArcOfCircle CenterX=-75.5 CenterY=-26 CenterZ=0 NormalX=0 NormalY=0 NormalZ=1 AngleXU=0 Radius=2 StartAngle=1.5708 EndAngle=3.14159
    g30: ArcOfCircle CenterX=75.5 CenterY=26 CenterZ=0 NormalX=0 NormalY=0 NormalZ=1 AngleXU=0 Radius=2 StartAngle=4.71239 EndAngle=6.28319
    g31: ArcOfCircle CenterX=75.5 CenterY=41 CenterZ=0 NormalX=0 NormalY=0 NormalZ=1 AngleXU=0 Radius=2 StartAngle=0 EndAngle=0.629894
    g32: ArcOfCircle CenterX=-75.5 CenterY=26 CenterZ=0 NormalX=0 NormalY=0 NormalZ=1 AngleXU=0 Radius=2 StartAngle=3.14159 EndAngle=4.71239
    g33: ArcOfCircle CenterX=-75.5 CenterY=41 CenterZ=0 NormalX=0 NormalY=0 NormalZ=1 AngleXU=0 Radius=2 StartAngle=2.5117 EndAngle=3.14159
    g34: LineSegment StartX=77.5 StartY=26 StartZ=0 EndX=77.5 EndY=-26 EndZ=0
    g35: LineSegment StartX=-77.5 StartY=26 StartZ=0 EndX=-77.5 EndY=-26 EndZ=0
    g36: ArcOfCircle CenterX=0 CenterY=52.6846 CenterZ=0 NormalX=0 NormalY=0 NormalZ=1 AngleXU=0 Radius=110.5 StartAngle=3.96814 EndAngle=5.45664
    g37: GeomPoint X=0 Y=-57.8154 Z=0
    g38: LineSegment StartX=-75.5 StartY=-27.1277 StartZ=0 EndX=-75.5 EndY=40.3484 EndZ=0
    g39: LineSegment StartX=-23.9829 StartY=108.185 StartZ=0 EndX=23.9829 EndY=108.185 EndZ=0
    g40: LineSegment StartX=-75.1162 StartY=41.5265 StartZ=0 EndX=-28.0234 EndY=106.13 EndZ=0
    g41: LineSegment StartX=75.5 StartY=-27.1277 StartZ=0 EndX=75.5 EndY=40.3484 EndZ=0
    g42: LineSegment StartX=28.0234 StartY=106.13 StartZ=0 EndX=75.1162 EndY=41.5265 EndZ=0
    g43: GeomPoint X=0 Y=108.185 Z=0
    g44: ArcOfCircle CenterX=-23.9829 CenterY=103.185 CenterZ=0 NormalX=0 NormalY=0 NormalZ=1 AngleXU=0 Radius=5 StartAngle=1.5708 EndAngle=2.5117
    g45: ArcOfCircle CenterX=23.9829 CenterY=103.185 CenterZ=0 NormalX=0 NormalY=0 NormalZ=1 AngleXU=0 Radius=5 StartAngle=0.629894 EndAngle=1.5708
    g46: ArcOfCircle CenterX=73.5 CenterY=40.3484 CenterZ=0 NormalX=0 NormalY=0 NormalZ=1 AngleXU=0 Radius=2 StartAngle=1e-15 EndAngle=0.629894
    g47: ArcOfCircle CenterX=-73.5 CenterY=40.3484 CenterZ=0 NormalX=0 NormalY=0 NormalZ=1 AngleXU=0 Radius=2 StartAngle=2.5117 EndAngle=3.14159
    g48: ArcOfCircle CenterX=-73.5 CenterY=-27.1277 CenterZ=0 NormalX=0 NormalY=0 NormalZ=1 AngleXU=0 Radius=2 StartAngle=3.14159 EndAngle=3.96814
    g49: ArcOfCircle CenterX=73.5 CenterY=-27.1277 CenterZ=0 NormalX=0 NormalY=0 NormalZ=1 AngleXU=0 Radius=2 StartAngle=5.45664 EndAngle=6.28319
    g50: LineSegment StartX=-29.0404 StartY=108.13 StartZ=0 EndX=-27.4243 EndY=106.952 EndZ=0
  constraints (123):
    c: Vertical(g0)
    c: Vertical(g1)
    c: Horizontal(g2)
    c: Symmetric(g2,g2,g-1)
    c: Horizontal(g3)
    c: Horizontal(g5)
    c: Horizontal(g6)
    c: PointOnObject(g7,g-2)
    c: Horizontal(g8)
    c: Horizontal(g9)
    c: Horizontal(g11)
    c: Coincident(g13,g-1)
    c: PointOnObject(g13,g-2)
    c: Tangent(g10,g14) = 1.5708
    c: Tangent(g11,g14) = 1.5708
    c: Tangent(g11,g15) = 1.5708
    c: Tangent(g12,g15) = 1.5708
    c: Tangent(g8,g16) = -1.5708
    c: Tangent(g0,g16) = 1.5708
    c: Tangent(g5,g17) = 1.5708
    c: Tangent(g0,g17) = 1.5708
    c: Tangent(g1,g18) = -1.5708
    c: Tangent(g6,g18) = -1.5708
    c: Tangent(g1,g19) = -1.5708
    c: Tangent(g9,g19) = 1.5708
    c: Equal(g15,g14)
    c: Symmetric(g11,g11,g13)
    c: Equal(g18,g19)
    c: Equal(g19,g16)
    c: Equal(g16,g17)
    c: PointOnObject(g20,g-2)
    c: PointOnObject(g20,g7)
    c: Coincident(g4,g8)
    c: Coincident(g4,g9)
    c: Coincident(g3,g6)
    c: Coincident(g3,g5)
    c: DistanceX(g2,g2) = 115
    c: Symmetric(g0,g0,g2)
    c: Symmetric(g1,g1,g2)
    c: Radius(g19) = 7
    c: DistanceY(g20,g11) = 170
    c: Radius(g15) = 5
    c: DistanceX(g11,g11) = 50
    c: Equal(g9,g8)
    c: Equal(g9,g6)
    c: Coincident(g21,g7)
    c: PointOnObject(g20,g21)
    c: Diameter(g21) = 225
    c: Vertical(g22)
    c: Vertical(g23)
    c: Vertical(g24)
    c: Vertical(g25)
    c: Equal(g5,g8)
    c: Equal(g10,g12)
    c: Tangent(g7,g26) = -1.5708
    c: Tangent(g23,g26) = 1.5708
    c: Tangent(g23,g27) = 1.5708
    c: Tangent(g6,g27) = 1.5708
    c: Tangent(g7,g28) = -1.5708
    c: Tangent(g24,g28) = 1.5708
    c: Tangent(g24,g29) = 1.5708
    c: Tangent(g5,g29) = -1.5708
    c: Equal(g29,g27)
    c: Radius(g27) = 2
    c: Equal(g26,g28)
    c: Radius(g26) = 2
    c: Tangent(g9,g30) = -1.5708
    c: Tangent(g22,g30) = -1.5708
    c: Tangent(g22,g31) = -1.5708
    c: Tangent(g12,g31) = 1.5708
    c: Tangent(g8,g32) = 1.5708
    c: Tangent(g25,g32) = 1.5708
    c: Tangent(g10,g33) = 1.5708
    c: Tangent(g25,g33) = 1.5708
    c: Equal(g30,g32)
    c: Equal(g31,g33)
    c: DistanceY(g23,g23) = 2
    c: DistanceY(g22,g22) = 15
    c: DistanceY(g6,g9) = 48
    c: DistanceX(g24,g23) = 155
    c: Radius(g30) = 2
    c: Radius(g31) = 2
    c: Coincident(g34,g22)
    c: Coincident(g34,g23)
    c: Coincident(g35,g25)
    c: Coincident(g35,g24)
    c: PointOnObject(g36,g13)
    c: PointOnObject(g37,g-2)
    c: PointOnObject(g37,g36)
    c: Vertical(g38)
    c: Horizontal(g39)
    c: Vertical(g41)
    c: PointOnObject(g43,g13)
    c: Tangent(g40,g44) = 1.5708
    c: Tangent(g39,g44) = 1.5708
    c: Tangent(g39,g45) = 1.5708
    c: Tangent(g42,g45) = 1.5708
    c: Tangent(g41,g46) = -1.5708
    c: Tangent(g42,g46) = 1.5708
    c: Tangent(g38,g47) = 1.5708
    c: Tangent(g40,g47) = 1.5708
    c: Tangent(g38,g48) = 1.5708
    c: Tangent(g36,g48) = -1.5708
    c: Tangent(g36,g49) = -1.5708
    c: Tangent(g41,g49) = -1.5708
    c: DistanceY(g20,g37) = 2
    c: Equal(g49,g46)
    c: Equal(g49,g48)
    c: Equal(g48,g47)
    c: Radius(g49) = 2
    c: Symmetric(g39,g39,g43)
    c: DistanceY(g43,g13) = 2
    c: Radius(g45) = 5
    c: Equal(g45,g44)
    c: Parallel(g42,g12)
    c: DistanceX(g41,g22) = 2
    c: DistanceX(g25,g38) = 2
    c: Parallel(g40,g10)
    c: Diameter(g36) = 221
    c: PointOnObject(g50,g40)
    c: Perpendicular(g10,g50)
    c: Coincident(g50,g10)
    c: Distance(g50) = 2
FEATURE [Sketcher::SketchObject] Sketch008  label="Sketch_Shell_InnerMid_LoftEnd"
  FullyConstrained = true
  MapMode = 5
  Placement = pos=(0,0,26) rot=(0,0,1;0rad)
  Support = -> [DatumPlane004]
  expr: Constraints[81] = <<params>>.std_rad
  expr: Constraints[41] = <<params>>.tail_rad
  expr: Constraints[111] = <<params>>.tail_rad
  expr: Constraints[80] = <<params>>.std_rad
  expr: Constraints[76] = <<params>>.front_vert_edge
  expr: Constraints[36] = <<params>>.wheel_well_plate_width
  expr: Constraints[79] = <<params>>.plate_width
  expr: Constraints[47] = <<params>>.front_diameter
  expr: Constraints[104] = <<params>>.shell_wall_thick + <<params>>.shell_topbrack_angstart_overhang
  expr: Constraints[42] = <<params>>.tail_width
  expr: Constraints[78] = <<params>>.wheel_well_clearance
  expr: Constraints[65] = <<params>>.std_rad
  expr: Constraints[108] = <<params>>.std_rad
  expr: Constraints[40] = <<params>>.plate_length
  expr: Constraints[110] = <<params>>.shell_wall_thick + <<params>>.shell_topbrack_angstart_overhang
  expr: Constraints[120] = <<params>>.shell_wall_thick + <<params>>.shell_topbrack_angstart_overhang
  expr: Constraints[77] = <<params>>.back_vert_edge
  expr: Constraints[115] = <<params>>.shell_wall_thick + <<params>>.shell_topbrack_angstart_overhang
  expr: Constraints[63] = <<params>>.std_rad
  expr: Constraints[114] = <<params>>.shell_wall_thick + <<params>>.shell_topbrack_angstart_overhang
  sketch-geometry (52):
    g0: LineSegment StartX=-57.5 StartY=17 StartZ=0 EndX=-57.5 EndY=-17 EndZ=0
    g1: LineSegment StartX=57.5 StartY=17 StartZ=0 EndX=57.5 EndY=-17 EndZ=0
    g2: LineSegment StartX=-57.5 StartY=0 StartZ=0 EndX=57.5 EndY=0 EndZ=0
    g3: LineSegment StartX=-64.5 StartY=-24 StartZ=0 EndX=64.5 EndY=-24 EndZ=0
    g4: LineSegment StartX=-64.5 StartY=24 StartZ=0 EndX=64.5 EndY=24 EndZ=0
    g5: LineSegment StartX=-64.5 StartY=-24 StartZ=0 EndX=-75.5 EndY=-24 EndZ=0
    g6: LineSegment StartX=64.5 StartY=-24 StartZ=0 EndX=75.5 EndY=-24 EndZ=0
    g7: ArcOfCircle CenterX=0 CenterY=52.6846 CenterZ=0 NormalX=0 NormalY=0 NormalZ=1 AngleXU=0 Radius=112.5 StartAngle=3.96017 EndAngle=5.4646
    g8: LineSegment StartX=-64.5 StartY=24 StartZ=0 EndX=-75.5 EndY=24 EndZ=0
    g9: LineSegment StartX=64.5 StartY=24 StartZ=0 EndX=75.5 EndY=24 EndZ=0
    g10: LineSegment StartX=-77.1162 StartY=42.1781 StartZ=0 EndX=-29.0404 EndY=108.13 EndZ=0
    g11: LineSegment StartX=-25 StartY=110.185 StartZ=0 EndX=25 EndY=110.185 EndZ=0
    g12: LineSegment StartX=29.0404 StartY=108.13 StartZ=0 EndX=77.1162 EndY=42.1781 EndZ=0
    g13: LineSegment StartX=0 StartY=0 StartZ=0 EndX=0 EndY=110.185 EndZ=0
    g14: ArcOfCircle CenterX=-25 CenterY=105.185 CenterZ=0 NormalX=0 NormalY=0 NormalZ=1 AngleXU=0 Radius=5 StartAngle=1.5708 EndAngle=2.5117
    g15: ArcOfCircle CenterX=25 CenterY=105.185 CenterZ=0 NormalX=0 NormalY=0 NormalZ=1 AngleXU=0 Radius=5 StartAngle=0.629894 EndAngle=1.5708
    g16: ArcOfCircle CenterX=-64.5 CenterY=17 CenterZ=0 NormalX=0 NormalY=0 NormalZ=1 AngleXU=0 Radius=7 StartAngle=0 EndAngle=1.5708
    g17: ArcOfCircle CenterX=-64.5 CenterY=-17 CenterZ=0 NormalX=0 NormalY=0 NormalZ=1 AngleXU=0 Radius=7 StartAngle=4.71239 EndAngle=6.28319
    g18: ArcOfCircle CenterX=64.5 CenterY=-17 CenterZ=0 NormalX=0 NormalY=0 NormalZ=1 AngleXU=0 Radius=7 StartAngle=3.14159 EndAngle=4.71239
    g19: ArcOfCircle CenterX=64.5 CenterY=17 CenterZ=0 NormalX=0 NormalY=0 NormalZ=1 AngleXU=0 Radius=7 StartAngle=1.5708 EndAngle=3.14159
    g20: GeomPoint X=0 Y=-59.8154 Z=0
    g21: Circle CenterX=0 CenterY=52.6846 CenterZ=0 NormalX=0 NormalY=0 NormalZ=1 AngleXU=0 Radius=112.5
    g22: LineSegment StartX=77.5 StartY=26 StartZ=0 EndX=77.5 EndY=41 EndZ=0
    g23: LineSegment StartX=77.5 StartY=-26 StartZ=0 EndX=77.5 EndY=-28 EndZ=0
    g24: LineSegment StartX=-77.5 StartY=-28 StartZ=0 EndX=-77.5 EndY=-26 EndZ=0
    g25: LineSegment StartX=-77.5 StartY=26 StartZ=0 EndX=-77.5 EndY=41 EndZ=0
    g26: ArcOfCircle CenterX=75.5 CenterY=-28 CenterZ=0 NormalX=0 NormalY=0 NormalZ=1 AngleXU=0 Radius=2 StartAngle=5.4646 EndAngle=6.28319
    g27: ArcOfCircle CenterX=75.5 CenterY=-26 CenterZ=0 NormalX=0 NormalY=0 NormalZ=1 AngleXU=0 Radius=2 StartAngle=2e-16 EndAngle=1.5708
    g28: ArcOfCircle CenterX=-75.5 CenterY=-28 CenterZ=0 NormalX=0 NormalY=0 NormalZ=1 AngleXU=0 Radius=2 StartAngle=3.14159 EndAngle=3.96017
    g29: ArcOfCircle CenterX=-75.5 CenterY=-26 CenterZ=0 NormalX=0 NormalY=0 NormalZ=1 AngleXU=0 Radius=2 StartAngle=1.5708 EndAngle=3.14159
    g30: ArcOfCircle CenterX=75.5 CenterY=26 CenterZ=0 NormalX=0 NormalY=0 NormalZ=1 AngleXU=0 Radius=2 StartAngle=4.71239 EndAngle=6.28319
    g31: ArcOfCircle CenterX=75.5 CenterY=41 CenterZ=0 NormalX=0 NormalY=0 NormalZ=1 AngleXU=0 Radius=2 StartAngle=-1.8e-15 EndAngle=0.629894
    g32: ArcOfCircle CenterX=-75.5 CenterY=26 CenterZ=0 NormalX=0 NormalY=0 NormalZ=1 AngleXU=0 Radius=2 StartAngle=3.14159 EndAngle=4.71239
    g33: ArcOfCircle CenterX=-75.5 CenterY=41 CenterZ=0 NormalX=0 NormalY=0 NormalZ=1 AngleXU=0 Radius=2 StartAngle=2.5117 EndAngle=3.14159
    g34: LineSegment StartX=77.5 StartY=26 StartZ=0 EndX=77.5 EndY=-26 EndZ=0
    g35: LineSegment StartX=-77.5 StartY=26 StartZ=0 EndX=-77.5 EndY=-26 EndZ=0
    g36: ArcOfCircle CenterX=0 CenterY=52.6846 CenterZ=0 NormalX=0 NormalY=0 NormalZ=1 AngleXU=0 Radius=103.5 StartAngle=3.99798 EndAngle=5.4268
    g37: GeomPoint X=0 Y=-50.8154 Z=0
    g38: LineSegment StartX=-68.5 StartY=-23.9966 StartZ=0 EndX=-68.5 EndY=38.0679 EndZ=0
    g39: LineSegment StartX=-20.4232 StartY=101.185 StartZ=0 EndX=20.4232 EndY=101.185 EndZ=0
    g40: LineSegment StartX=-68.1162 StartY=39.246 StartZ=0 EndX=-24.4636 EndY=99.1299 EndZ=0
    g41: LineSegment StartX=68.5 StartY=-23.9966 StartZ=0 EndX=68.5 EndY=38.0679 EndZ=0
    g42: LineSegment StartX=24.4636 StartY=99.1299 StartZ=0 EndX=68.1162 EndY=39.246 EndZ=0
    g43: GeomPoint X=0 Y=101.185 Z=0
    g44: ArcOfCircle CenterX=-20.4232 CenterY=96.1846 CenterZ=0 NormalX=0 NormalY=0 NormalZ=1 AngleXU=0 Radius=5 StartAngle=1.5708 EndAngle=2.5117
    g45: ArcOfCircle CenterX=20.4232 CenterY=96.1846 CenterZ=0 NormalX=0 NormalY=0 NormalZ=1 AngleXU=0 Radius=5 StartAngle=0.629894 EndAngle=1.5708
    g46: ArcOfCircle CenterX=66.5 CenterY=38.0679 CenterZ=0 NormalX=0 NormalY=0 NormalZ=1 AngleXU=0 Radius=2 StartAngle=1.6e-15 EndAngle=0.629894
    g47: ArcOfCircle CenterX=-66.5 CenterY=38.0679 CenterZ=0 NormalX=0 NormalY=0 NormalZ=1 AngleXU=0 Radius=2 StartAngle=2.5117 EndAngle=3.14159
    g48: ArcOfCircle CenterX=-66.5 CenterY=-23.9966 CenterZ=0 NormalX=0 NormalY=0 NormalZ=1 AngleXU=0 Radius=2 StartAngle=3.14159 EndAngle=3.99798
    g49: ArcOfCircle CenterX=66.5 CenterY=-23.9966 CenterZ=0 NormalX=0 NormalY=0 NormalZ=1 AngleXU=0 Radius=2 StartAngle=5.4268 EndAngle=6.28319
    g50: GeomPoint X=-75.5 Y=41 Z=0
    g51: LineSegment StartX=-29.0404 StartY=108.13 StartZ=0 EndX=-21.7676 EndY=102.828 EndZ=0
  constraints (123):
    c: Vertical(g0)
    c: Vertical(g1)
    c: Horizontal(g2)
    c: Symmetric(g2,g2,g-1)
    c: Horizontal(g3)
    c: Horizontal(g5)
    c: Horizontal(g6)
    c: PointOnObject(g7,g-2)
    c: Horizontal(g8)
    c: Horizontal(g9)
    c: Horizontal(g11)
    c: Coincident(g13,g-1)
    c: PointOnObject(g13,g-2)
    c: Tangent(g10,g14) = 1.5708
    c: Tangent(g11,g14) = 1.5708
    c: Tangent(g11,g15) = 1.5708
    c: Tangent(g12,g15) = 1.5708
    c: Tangent(g8,g16) = -1.5708
    c: Tangent(g0,g16) = 1.5708
    c: Tangent(g5,g17) = 1.5708
    c: Tangent(g0,g17) = 1.5708
    c: Tangent(g1,g18) = -1.5708
    c: Tangent(g6,g18) = -1.5708
    c: Tangent(g1,g19) = -1.5708
    c: Tangent(g9,g19) = 1.5708
    c: Equal(g15,g14)
    c: Symmetric(g11,g11,g13)
    c: Equal(g18,g19)
    c: Equal(g19,g16)
    c: Equal(g16,g17)
    c: PointOnObject(g20,g-2)
    c: PointOnObject(g20,g7)
    c: Coincident(g4,g8)
    c: Coincident(g4,g9)
    c: Coincident(g3,g6)
    c: Coincident(g3,g5)
    c: DistanceX(g2,g2) = 115
    c: Symmetric(g0,g0,g2)
    c: Symmetric(g1,g1,g2)
    c: Radius(g19) = 7
    c: DistanceY(g20,g11) = 170
    c: Radius(g15) = 5
    c: DistanceX(g11,g11) = 50
    c: Equal(g9,g8)
    c: Equal(g9,g6)
    c: Coincident(g21,g7)
    c: PointOnObject(g20,g21)
    c: Diameter(g21) = 225
    c: Vertical(g22)
    c: Vertical(g23)
    c: Vertical(g24)
    c: Vertical(g25)
    c: Equal(g5,g8)
    c: Equal(g10,g12)
    c: Tangent(g7,g26) = -1.5708
    c: Tangent(g23,g26) = 1.5708
    c: Tangent(g23,g27) = 1.5708
    c: Tangent(g6,g27) = 1.5708
    c: Tangent(g7,g28) = -1.5708
    c: Tangent(g24,g28) = 1.5708
    c: Tangent(g24,g29) = 1.5708
    c: Tangent(g5,g29) = -1.5708
    c: Equal(g29,g27)
    c: Radius(g27) = 2
    c: Equal(g26,g28)
    c: Radius(g26) = 2
    c: Tangent(g9,g30) = -1.5708
    c: Tangent(g22,g30) = -1.5708
    c: Tangent(g22,g31) = -1.5708
    c: Tangent(g12,g31) = 1.5708
    c: Tangent(g8,g32) = 1.5708
    c: Tangent(g25,g32) = 1.5708
    c: Tangent(g10,g33) = 1.5708
    c: Tangent(g25,g33) = 1.5708
    c: Equal(g30,g32)
    c: Equal(g31,g33)
    c: DistanceY(g23,g23) = 2
    c: DistanceY(g22,g22) = 15
    c: DistanceY(g6,g9) = 48
    c: DistanceX(g24,g23) = 155
    c: Radius(g30) = 2
    c: Radius(g31) = 2
    c: Coincident(g34,g22)
    c: Coincident(g34,g23)
    c: Coincident(g35,g25)
    c: Coincident(g35,g24)
    c: PointOnObject(g37,g-2)
    c: PointOnObject(g37,g36)
    c: Vertical(g38)
    c: Horizontal(g39)
    c: Vertical(g41)
    c: PointOnObject(g43,g13)
    c: Tangent(g40,g44) = 1.5708
    c: Tangent(g39,g44) = 1.5708
    c: Tangent(g39,g45) = 1.5708
    c: Tangent(g42,g45) = 1.5708
    c: Tangent(g41,g46) = -1.5708
    c: Tangent(g42,g46) = 1.5708
    c: Tangent(g38,g47) = 1.5708
    c: Tangent(g40,g47) = 1.5708
    c: Tangent(g38,g48) = 1.5708
    c: Tangent(g36,g48) = -1.5708
    c: Tangent(g36,g49) = -1.5708
    c: Tangent(g41,g49) = -1.5708
    c: DistanceY(g20,g37) = 9
    c: Equal(g49,g46)
    c: Equal(g49,g48)
    c: Equal(g48,g47)
    c: Radius(g49) = 2
    c: Symmetric(g39,g39,g43)
    c: DistanceY(g43,g13) = 9
    c: Radius(g45) = 5
    c: Equal(g45,g44)
    c: Parallel(g42,g12)
    c: DistanceX(g41,g22) = 9
    c: DistanceX(g25,g38) = 9
    c: Parallel(g40,g10)
    c: Coincident(g50,g33)
    c: PointOnObject(g51,g40)
    c: Perpendicular(g40,g51)
    c: Distance(g51) = 9
    c: Coincident(g51,g10)
    c: Coincident(g36,g7)
FEATURE [PartDesign::SubtractiveLoft] SubtractiveLoft  label="Shell_MidWalllAng_SubLoft"
  BaseFeature = -> Pocket001
  Closed = false
  Profile = -> Sketch007
  Ruled = false
  Sections = -> [Sketch008]
FEATURE [Sketcher::SketchObject] Sketch010  label="Sketch_TopBrackAng_LoftEnd"
  FullyConstrained = true
  MapMode = 5
  Placement = pos=(0,0,35) rot=(0,0,1;0rad)
  Support = -> [DatumPlane003]
  expr: Constraints[48] = <<params>>.shell_wall_thick + <<params>>.shell_topbrack_angend_overhang
  expr: Constraints[62] = <<params>>.shell_overhang_leng + <<params>>.shell_topbrack_width
  expr: Constraints[33] = <<params>>.plate_width
  expr: Constraints[34] = <<params>>.std_rad
  expr: Constraints[13] = <<params>>.tail_rad
  expr: Constraints[78] = <<params>>.shell_wall_thick + <<params>>.shell_topbrack_angend_overhang
  expr: Constraints[42] = <<params>>.shell_wall_thick + <<params>>.shell_topbrack_angend_overhang
  expr: Constraints[32] = <<params>>.back_vert_edge
  expr: Constraints[108] = <<params>>.front_diameter
  expr: Constraints[12] = <<params>>.plate_length
  expr: Constraints[41] = <<params>>.shell_wall_thick + <<params>>.shell_topbrack_angend_overhang
  expr: Constraints[75] = <<params>>.shell_topbrack_angend_overhang + <<params>>.shell_wall_thick
  expr: Constraints[14] = <<params>>.tail_width
  expr: Constraints[118] = <<params>>.wheel_well_clearance + 2 * <<params>>.std_rad
  expr: Constraints[60] = <<params>>.std_rad / 2
  expr: Constraints[92] = <<params>>.shell_overhang_leng + <<params>>.shell_topbrack_width
  expr: Constraints[61] = <<params>>.shell_wall_thick + <<params>>.shell_topbrack_angend_overhang
  expr: Constraints[31] = <<params>>.front_vert_edge
  expr: Constraints[25] = <<params>>.std_rad
  expr: Constraints[179] = <<params>>.top_brack_front_leng
  sketch-geometry (73):
    g0: ArcOfCircle CenterX=0 CenterY=52.6846 CenterZ=0 NormalX=0 NormalY=0 NormalZ=1 AngleXU=0 Radius=112.5 StartAngle=3.96017 EndAngle=5.4646
    g1: LineSegment StartX=-77.1162 StartY=42.1781 StartZ=0 EndX=-29.0404 EndY=108.13 EndZ=0
    g2: LineSegment StartX=-25 StartY=110.185 StartZ=0 EndX=25 EndY=110.185 EndZ=0
    g3: LineSegment StartX=29.0404 StartY=108.13 StartZ=0 EndX=77.1162 EndY=42.1781 EndZ=0
    g4: LineSegment StartX=0 StartY=0 StartZ=0 EndX=0 EndY=110.185 EndZ=0
    g5: ArcOfCircle CenterX=-25 CenterY=105.185 CenterZ=0 NormalX=0 NormalY=0 NormalZ=1 AngleXU=0 Radius=5 StartAngle=1.5708 EndAngle=2.5117
    g6: ArcOfCircle CenterX=25 CenterY=105.185 CenterZ=0 NormalX=0 NormalY=0 NormalZ=1 AngleXU=0 Radius=5 StartAngle=0.629894 EndAngle=1.5708
    g7: GeomPoint X=0 Y=-59.8154 Z=0
    g8: LineSegment StartX=77.5 StartY=26 StartZ=0 EndX=77.5 EndY=41 EndZ=0
    g9: LineSegment StartX=77.5 StartY=-26 StartZ=0 EndX=77.5 EndY=-28 EndZ=0
    g10: LineSegment StartX=-77.5 StartY=-28 StartZ=0 EndX=-77.5 EndY=-26 EndZ=0
    g11: LineSegment StartX=-77.5 StartY=26 StartZ=0 EndX=-77.5 EndY=41 EndZ=0
    g12: ArcOfCircle CenterX=75.5 CenterY=-28 CenterZ=0 NormalX=0 NormalY=0 NormalZ=1 AngleXU=0 Radius=2 StartAngle=5.4646 EndAngle=6.28319
    g13: ArcOfCircle CenterX=-75.5 CenterY=-28 CenterZ=0 NormalX=0 NormalY=0 NormalZ=1 AngleXU=0 Radius=2 StartAngle=3.14159 EndAngle=3.96017
    g14: ArcOfCircle CenterX=75.5 CenterY=41 CenterZ=0 NormalX=0 NormalY=0 NormalZ=1 AngleXU=0 Radius=2 StartAngle=-9e-16 EndAngle=0.629894
    g15: ArcOfCircle CenterX=-75.5 CenterY=41 CenterZ=0 NormalX=0 NormalY=0 NormalZ=1 AngleXU=0 Radius=2 StartAngle=2.5117 EndAngle=3.14159
    g16: ArcOfCircle CenterX=0 CenterY=52.6846 CenterZ=0 NormalX=0 NormalY=0 NormalZ=1 AngleXU=0 Radius=99.5625 StartAngle=4.01626 EndAngle=5.40852
    g17: GeomPoint X=0 Y=-46.8779 Z=0
    g18: LineSegment StartX=-64.5625 StartY=-22.1778 StartZ=0 EndX=-64.5625 EndY=26 EndZ=0
    g19: LineSegment StartX=-14.3322 StartY=97.2471 StartZ=0 EndX=-1 EndY=97.2471 EndZ=0
    g20: LineSegment StartX=-56.3081 StartY=48.7603 StartZ=0 EndX=-27.1403 EndY=88.7736 EndZ=0
    g21: LineSegment StartX=64.5625 StartY=-22.1778 StartZ=0 EndX=64.5625 EndY=26 EndZ=0
    g22: LineSegment StartX=27.1403 StartY=88.7736 StartZ=0 EndX=56.3081 EndY=48.7603 EndZ=0
    g23: GeomPoint X=0 Y=97.2471 Z=0
    g24: GeomPoint X=-75.5 Y=41 Z=0
    g25: LineSegment StartX=-29.0404 StartY=108.13 StartZ=0 EndX=-18.5858 EndY=100.509 EndZ=0
    g26: LineSegment StartX=63.5625 StartY=27 StartZ=0 EndX=57.5 EndY=27 EndZ=0
    g27: LineSegment StartX=56.5 StartY=28 StartZ=0 EndX=56.5 EndY=48.1713 EndZ=0
    g28: ArcOfCircle CenterX=55.5 CenterY=48.1713 CenterZ=0 NormalX=0 NormalY=0 NormalZ=1 AngleXU=0 Radius=1 StartAngle=2e-16 EndAngle=0.629894
    g29: ArcOfCircle CenterX=57.5 CenterY=28 CenterZ=0 NormalX=0 NormalY=0 NormalZ=1 AngleXU=0 Radius=1 StartAngle=3.14159 EndAngle=4.71239
    g30: ArcOfCircle CenterX=63.5625 CenterY=26 CenterZ=0 NormalX=0 NormalY=0 NormalZ=1 AngleXU=0 Radius=1 StartAngle=0 EndAngle=1.5708
    g31: LineSegment StartX=-56.5 StartY=48.1713 StartZ=0 EndX=-56.5 EndY=28 EndZ=0
    g32: LineSegment StartX=-63.5625 StartY=27 StartZ=0 EndX=-57.5 EndY=27 EndZ=0
    g33: ArcOfCircle CenterX=-63.5625 CenterY=26 CenterZ=0 NormalX=0 NormalY=0 NormalZ=1 AngleXU=0 Radius=1 StartAngle=1.5708 EndAngle=3.14159
    g34: ArcOfCircle CenterX=-57.5 CenterY=28 CenterZ=0 NormalX=0 NormalY=0 NormalZ=1 AngleXU=0 Radius=1 StartAngle=4.71239 EndAngle=6.28319
    g35: ArcOfCircle CenterX=-55.5 CenterY=48.1713 CenterZ=0 NormalX=0 NormalY=0 NormalZ=1 AngleXU=0 Radius=1 StartAngle=2.5117 EndAngle=3.14159
    g36: LineSegment StartX=27.1403 StartY=88.7736 StartZ=0 EndX=37.5949 EndY=96.3946 EndZ=0
    g37: LineSegment StartX=0 StartY=96.2471 StartZ=0 EndX=0 EndY=90.1846 EndZ=0
    g38: LineSegment StartX=1 StartY=89.1846 StartZ=0 EndX=26.3322 EndY=89.1846 EndZ=0
    g39: ArcOfCircle CenterX=-1 CenterY=96.2471 CenterZ=0 NormalX=0 NormalY=0 NormalZ=1 AngleXU=0 Radius=1 StartAngle=6e-15 EndAngle=1.5708
    g40: ArcOfCircle CenterX=1 CenterY=90.1846 CenterZ=0 NormalX=0 NormalY=0 NormalZ=1 AngleXU=0 Radius=1 StartAngle=3.14159 EndAngle=4.71239
    g41: ArcOfCircle CenterX=26.3322 CenterY=88.1846 CenterZ=0 NormalX=0 NormalY=0 NormalZ=1 AngleXU=0 Radius=1 StartAngle=0.629894 EndAngle=1.5708
    g42: LineSegment StartX=-26.3322 StartY=89.1846 StartZ=0 EndX=-16.3322 EndY=89.1846 EndZ=0
    g43: LineSegment StartX=-15.3322 StartY=90.1846 StartZ=0 EndX=-15.3322 EndY=96.2471 EndZ=0
    g44: ArcOfCircle CenterX=-14.3322 CenterY=96.2471 CenterZ=0 NormalX=0 NormalY=0 NormalZ=1 AngleXU=0 Radius=1 StartAngle=1.5708 EndAngle=3.14159
    g45: ArcOfCircle CenterX=-16.3322 CenterY=90.1846 CenterZ=0 NormalX=0 NormalY=0 NormalZ=1 AngleXU=0 Radius=1 StartAngle=4.71239 EndAngle=6.28319
    g46: ArcOfCircle CenterX=-26.3322 CenterY=88.1846 CenterZ=0 NormalX=0 NormalY=0 NormalZ=1 AngleXU=0 Radius=1 StartAngle=1.5708 EndAngle=2.5117
    g47: ArcOfCircle CenterX=62.5625 CenterY=-22.1778 CenterZ=0 NormalX=0 NormalY=0 NormalZ=1 AngleXU=0 Radius=2 StartAngle=5.40852 EndAngle=6.28319
    g48: ArcOfCircle CenterX=-62.5625 CenterY=-22.1778 CenterZ=0 NormalX=0 NormalY=0 NormalZ=1 AngleXU=0 Radius=2 StartAngle=3.14159 EndAngle=4.01626
    g49: LineSegment StartX=77.5 StartY=26 StartZ=0 EndX=77.5 EndY=-26 EndZ=0
    g50: LineSegment StartX=-77.5 StartY=26 StartZ=0 EndX=-77.5 EndY=-26 EndZ=0
    g51: GeomPoint X=77.5 Y=0 Z=0
    g52: GeomPoint X=-77.5 Y=0 Z=0
    g53: LineSegment StartX=64.5625 StartY=26 StartZ=0 EndX=77.5 EndY=26 EndZ=0
    g54: LineSegment StartX=-56.5 StartY=-28.7667 StartZ=0 EndX=-56.5 EndY=-19 EndZ=0
    g55: LineSegment StartX=-57.5 StartY=-18 StartZ=0 EndX=-63.5625 EndY=-18 EndZ=0
    g56: LineSegment StartX=-64.5625 StartY=26 StartZ=0 EndX=-64.5625 EndY=-17 EndZ=0
    g57: ArcOfCircle CenterX=-57.5 CenterY=-19 CenterZ=0 NormalX=0 NormalY=0 NormalZ=1 AngleXU=0 Radius=1 StartAngle=1.4e-15 EndAngle=1.5708
    g58: ArcOfCircle CenterX=-63.5625 CenterY=-17 CenterZ=0 NormalX=0 NormalY=0 NormalZ=1 AngleXU=0 Radius=1 StartAngle=3.14159 EndAngle=4.71239
    g59: LineSegment StartX=-57.5 StartY=27 StartZ=0 EndX=-57.5 EndY=-18 EndZ=0
    g60: ArcOfCircle CenterX=-55.5 CenterY=-28.7667 CenterZ=0 NormalX=0 NormalY=0 NormalZ=1 AngleXU=0 Radius=1 StartAngle=3.14159 EndAngle=4.11426
    g61: LineSegment StartX=63.5625 StartY=-18 StartZ=0 EndX=57.5 EndY=-18 EndZ=0
    g62: LineSegment StartX=56.5 StartY=-19 StartZ=0 EndX=56.5 EndY=-28.7667 EndZ=0
    g63: LineSegment StartX=64.5625 StartY=26 StartZ=0 EndX=64.5625 EndY=-17 EndZ=0
    g64: ArcOfCircle CenterX=57.5 CenterY=-19 CenterZ=0 NormalX=0 NormalY=0 NormalZ=1 AngleXU=0 Radius=1 StartAngle=1.5708 EndAngle=3.14159
    g65: ArcOfCircle CenterX=63.5625 CenterY=-17 CenterZ=0 NormalX=0 NormalY=0 NormalZ=1 AngleXU=0 Radius=1 StartAngle=4.71239 EndAngle=6.28319
    g66: LineSegment StartX=57.5 StartY=27 StartZ=0 EndX=57.5 EndY=-18 EndZ=0
    g67: LineSegment StartX=-56.5 StartY=-19 StartZ=0 EndX=56.5 EndY=-19 EndZ=0
    g68: ArcOfCircle CenterX=0 CenterY=52.6846 CenterZ=0 NormalX=0 NormalY=0 NormalZ=1 AngleXU=0 Radius=99.5625 StartAngle=4.11426 EndAngle=5.31051
    g69: ArcOfCircle CenterX=55.5 CenterY=-28.7667 CenterZ=0 NormalX=0 NormalY=0 NormalZ=1 AngleXU=0 Radius=1 StartAngle=5.31051 EndAngle=6.28319
    g70: LineSegment StartX=-27.1403 StartY=88.7736 StartZ=0 EndX=-22.4613 EndY=95.1924 EndZ=0
    g71: LineSegment StartX=-14.3322 StartY=97.2471 StartZ=0 EndX=-18.4208 EndY=97.2471 EndZ=0
    g72: ArcOfCircle CenterX=-18.4208 CenterY=92.2471 CenterZ=0 NormalX=0 NormalY=0 NormalZ=1 AngleXU=0 Radius=5 StartAngle=1.5708 EndAngle=2.5117
  constraints (180):
    c: PointOnObject(g0,g-2)
    c: Horizontal(g2)
    c: Coincident(g4,g-1)
    c: PointOnObject(g4,g-2)
    c: Tangent(g1,g5) = 1.5708
    c: Tangent(g2,g5) = 1.5708
    c: Tangent(g2,g6) = 1.5708
    c: Tangent(g3,g6) = 1.5708
    c: Equal(g6,g5)
    c: Symmetric(g2,g2,g4)
    c: PointOnObject(g7,g-2)
    c: PointOnObject(g7,g0)
    c: DistanceY(g7,g2) = 170
    c: Radius(g6) = 5
    c: DistanceX(g2,g2) = 50
    c: Vertical(g8)
    c: Vertical(g9)
    c: Vertical(g10)
    c: Vertical(g11)
    c: Equal(g1,g3)
    c: Tangent(g0,g12) = -1.5708
    c: Tangent(g9,g12) = 1.5708
    c: Tangent(g0,g13) = -1.5708
    c: Tangent(g10,g13) = 1.5708
    c: Equal(g12,g13)
    c: Radius(g12) = 2
    c: Tangent(g8,g14) = -1.5708
    c: Tangent(g3,g14) = 1.5708
    c: Tangent(g1,g15) = 1.5708
    c: Tangent(g11,g15) = 1.5708
    c: Equal(g14,g15)
    c: DistanceY(g9,g9) = 2
    c: DistanceY(g8,g8) = 15
    c: DistanceX(g10,g9) = 155
    c: Radius(g14) = 2
    c: PointOnObject(g17,g-2)
    c: PointOnObject(g17,g16)
    c: Vertical(g18)
    c: Horizontal(g19)
    c: Vertical(g21)
    c: PointOnObject(g23,g4)
    c: DistanceY(g7,g17) = 12.9375
    c: DistanceY(g23,g4) = 12.9375
    c: Parallel(g22,g3)
    c: Parallel(g20,g1)
    c: Coincident(g24,g15)
    c: PointOnObject(g25,g20)
    c: Perpendicular(g20,g25)
    c: Distance(g25) = 12.9375
    c: Coincident(g25,g1)
    c: Horizontal(g26)
    c: Vertical(g27)
    c: Tangent(g27,g28) = -1.5708
    c: Tangent(g22,g28) = 1.5708
    c: Tangent(g27,g29) = 1.5708
    c: Tangent(g26,g29) = 1.5708
    c: Tangent(g21,g30) = -1.5708
    c: Tangent(g26,g30) = -1.5708
    c: Equal(g28,g29)
    c: Equal(g30,g29)
    c: Radius(g30) = 1
    c: DistanceX(g21,g8) = 12.9375
    c: DistanceX(g27,g8) = 21
    c: Vertical(g31)
    c: Horizontal(g32)
    c: Tangent(g18,g33) = 1.5708
    c: Tangent(g32,g33) = 1.5708
    c: Tangent(g32,g34) = -1.5708
    c: Tangent(g31,g34) = 1.5708
    c: Tangent(g31,g35) = -1.5708
    c: Tangent(g20,g35) = 1.5708
    c: Equal(g35,g34)
    c: Equal(g34,g33)
    c: Equal(g35,g28)
    c: Equal(g32,g26)
    c: DistanceX(g11,g18) = 12.9375
    c: PointOnObject(g36,g3)
    c: Perpendicular(g36,g22)
    c: Distance(g36) = 12.9375
    c: PointOnObject(g23,g19)
    c: Vertical(g37)
    c: Horizontal(g38)
    c: Tangent(g19,g39) = 1.5708
    c: Tangent(g37,g39) = 1.5708
    c: Tangent(g37,g40) = -1.5708
    c: Tangent(g38,g40) = -1.5708
    c: Tangent(g38,g41) = 1.5708
    c: Tangent(g22,g41) = 1.5708
    c: Coincident(g36,g22)
    c: Equal(g28,g41)
    c: Equal(g41,g40)
    c: Equal(g40,g39)
    c: DistanceY(g38,g4) = 21
    c: Horizontal(g42)
    c: Vertical(g43)
    c: Tangent(g43,g44) = 1.5708
    c: Tangent(g19,g44) = 1.5708
    c: Tangent(g42,g45) = -1.5708
    c: Tangent(g43,g45) = -1.5708
    c: Tangent(g42,g46) = 1.5708
    c: Tangent(g20,g46) = 1.5708
    c: Equal(g46,g45)
    c: Equal(g45,g44)
    c: Equal(g44,g39)
    c: Equal(g43,g37)
    c: Tangent(g21,g47) = -1.5708
    c: Tangent(g18,g48) = 1.5708
    c: Equal(g48,g13)
    c: Diameter(g0) = 225
    c: Coincident(g49,g8)
    c: Coincident(g49,g9)
    c: Vertical(g49)
    c: Coincident(g50,g11)
    c: Coincident(g50,g10)
    c: Vertical(g50)
    c: PointOnObject(g51,g-1)
    c: Symmetric(g8,g9,g51)
    c: Symmetric(g11,g10,g52)
    c: DistanceY(g9,g8) = 52
    c: Equal(g49,g50)
    c: Symmetric(g52,g51,g-1)
    c: Equal(g12,g47)
    c: Coincident(g53,g21)
    c: Coincident(g53,g8)
    c: Horizontal(g53)
    c: Equal(g31,g27)
    c: Coincident(g16,g48)
    c: Tangent(g16,g48)
    c: Vertical(g54)
    c: Horizontal(g55)
    c: Coincident(g56,g33)
    c: Tangent(g55,g57) = -1.5708
    c: Tangent(g54,g57) = -1.5708
    c: Tangent(g56,g58) = -1.5708
    c: Tangent(g55,g58) = 1.5708
    c: Coincident(g59,g32)
    c: Coincident(g59,g55)
    c: Vertical(g59)
    c: Equal(g58,g57)
    c: Equal(g57,g34)
    c: PointOnObject(g56,g18)
    c: Tangent(g54,g60) = 1.5708
    c: Equal(g60,g57)
    c: Coincident(g16,g47)
    c: Tangent(g47,g16)
    c: Horizontal(g61)
    c: Vertical(g62)
    c: Vertical(g63)
    c: PointOnObject(g63,g53)
    c: Tangent(g61,g64) = -1.5708
    c: Tangent(g62,g64) = -1.5708
    c: Tangent(g61,g65) = 1.5708
    c: Tangent(g63,g65) = 1.5708
    c: Equal(g65,g29)
    c: Equal(g65,g64)
    c: PointOnObject(g63,g21)
    c: Coincident(g66,g26)
    c: Coincident(g66,g61)
    c: Vertical(g66)
    c: Coincident(g67,g54)
    c: Coincident(g67,g62)
    c: Horizontal(g67)
    c: Coincident(g68,g16)
    c: Coincident(g68,g60)
    c: Tangent(g62,g69) = 1.5708
    c: Tangent(g68,g69) = -1.5708
    c: PointOnObject(g17,g68)
    c: Tangent(g60,g68)
    c: Equal(g64,g69)
    c: Coincident(g70,g20)
    c: Tangent(g70,g46)
    c: Coincident(g71,g19)
    c: Horizontal(g71)
    c: Tangent(g70,g72) = 1.5708
    c: Tangent(g71,g72) = -1.5708
    c: Equal(g72,g5)
    c: PointOnObject(g37,g4)
    c: Distance(g42) = 10
    c: Coincident(g68,g0)
    c: DistanceY(g9,g61) = 10
FEATURE [Sketcher::SketchObject] Sketch011  label="Sketch_TopBrackAng_LoftStart"
  FullyConstrained = true
  MapMode = 5
  Placement = pos=(0,0,26) rot=(0,0,1;0rad)
  Support = -> [DatumPlane004]
  expr: Constraints[33] = <<params>>.plate_width
  expr: Constraints[103] = <<params>>.shell_overhang_leng + <<params>>.shell_topbrack_width
  expr: Constraints[58] = <<params>>.shell_wall_thick + <<params>>.shell_topbrack_angstart_overhang
  expr: Constraints[68] = <<params>>.std_rad
  expr: Constraints[52] = <<params>>.shell_wall_thick + <<params>>.shell_topbrack_angstart_overhang
  expr: Constraints[25] = <<params>>.std_rad
  expr: Constraints[31] = <<params>>.front_vert_edge
  expr: Constraints[54] = <<params>>.shell_wall_thick + <<params>>.shell_topbrack_angstart_overhang
  expr: Constraints[77] = <<params>>.wheel_well_clearance + 2 * <<params>>.std_rad
  expr: Constraints[32] = <<params>>.back_vert_edge
  expr: Constraints[55] = <<params>>.tail_rad
  expr: Constraints[14] = <<params>>.tail_width
  expr: Constraints[12] = <<params>>.plate_length
  expr: Constraints[34] = <<params>>.std_rad
  expr: Constraints[102] = <<params>>.std_rad / 2
  expr: Constraints[64] = <<params>>.shell_wall_thick + <<params>>.shell_topbrack_angstart_overhang
  expr: Constraints[13] = <<params>>.tail_rad
  expr: Constraints[73] = <<params>>.front_diameter
  expr: Constraints[59] = <<params>>.shell_wall_thick + <<params>>.shell_topbrack_angstart_overhang
  expr: Constraints[104] = <<params>>.shell_topbrack_width * 3
  sketch-geometry (43):
    g0: ArcOfCircle CenterX=0 CenterY=52.6846 CenterZ=0 NormalX=0 NormalY=0 NormalZ=1 AngleXU=0 Radius=112.5 StartAngle=3.96017 EndAngle=5.4646
    g1: LineSegment StartX=-77.1162 StartY=42.1781 StartZ=0 EndX=-29.0404 EndY=108.13 EndZ=0
    g2: LineSegment StartX=-25 StartY=110.185 StartZ=0 EndX=25 EndY=110.185 EndZ=0
    g3: LineSegment StartX=29.0404 StartY=108.13 StartZ=0 EndX=77.1162 EndY=42.1781 EndZ=0
    g4: LineSegment StartX=0 StartY=0 StartZ=0 EndX=0 EndY=110.185 EndZ=0
    g5: ArcOfCircle CenterX=-25 CenterY=105.185 CenterZ=0 NormalX=0 NormalY=0 NormalZ=1 AngleXU=0 Radius=5 StartAngle=1.5708 EndAngle=2.5117
    g6: ArcOfCircle CenterX=25 CenterY=105.185 CenterZ=0 NormalX=0 NormalY=0 NormalZ=1 AngleXU=0 Radius=5 StartAngle=0.629894 EndAngle=1.5708
    g7: GeomPoint X=0 Y=-59.8154 Z=0
    g8: LineSegment StartX=77.5 StartY=26 StartZ=0 EndX=77.5 EndY=41 EndZ=0
    g9: LineSegment StartX=77.5 StartY=-26 StartZ=0 EndX=77.5 EndY=-28 EndZ=0
    g10: LineSegment StartX=-77.5 StartY=-28 StartZ=0 EndX=-77.5 EndY=-26 EndZ=0
    g11: LineSegment StartX=-77.5 StartY=26 StartZ=0 EndX=-77.5 EndY=41 EndZ=0
    g12: ArcOfCircle CenterX=75.5 CenterY=-28 CenterZ=0 NormalX=0 NormalY=0 NormalZ=1 AngleXU=0 Radius=2 StartAngle=5.4646 EndAngle=6.28319
    g13: ArcOfCircle CenterX=-75.5 CenterY=-28 CenterZ=0 NormalX=0 NormalY=0 NormalZ=1 AngleXU=0 Radius=2 StartAngle=3.14159 EndAngle=3.96017
    g14: ArcOfCircle CenterX=75.5 CenterY=41 CenterZ=0 NormalX=0 NormalY=0 NormalZ=1 AngleXU=0 Radius=2 StartAngle=-9e-16 EndAngle=0.629894
    g15: ArcOfCircle CenterX=-75.5 CenterY=41 CenterZ=0 NormalX=0 NormalY=0 NormalZ=1 AngleXU=0 Radius=2 StartAngle=2.5117 EndAngle=3.14159
    g16: LineSegment StartX=77.5 StartY=26 StartZ=0 EndX=77.5 EndY=-26 EndZ=0
    g17: LineSegment StartX=-77.5 StartY=26 StartZ=0 EndX=-77.5 EndY=-26 EndZ=0
    g18: GeomPoint X=0 Y=-50.8154 Z=0
    g19: LineSegment StartX=-68.5 StartY=-23.9966 StartZ=0 EndX=-68.5 EndY=38.0679 EndZ=0
    g20: LineSegment StartX=-20.4232 StartY=101.185 StartZ=0 EndX=20.4232 EndY=101.185 EndZ=0
    g21: LineSegment StartX=-68.1162 StartY=39.246 StartZ=0 EndX=-24.4636 EndY=99.1299 EndZ=0
    g22: LineSegment StartX=68.5 StartY=-23.9966 StartZ=0 EndX=68.5 EndY=38.0679 EndZ=0
    g23: LineSegment StartX=24.4636 StartY=99.1299 StartZ=0 EndX=68.1162 EndY=39.246 EndZ=0
    g24: GeomPoint X=0 Y=101.185 Z=0
    g25: ArcOfCircle CenterX=-20.4232 CenterY=96.1846 CenterZ=0 NormalX=0 NormalY=0 NormalZ=1 AngleXU=0 Radius=5 StartAngle=1.5708 EndAngle=2.5117
    g26: ArcOfCircle CenterX=20.4232 CenterY=96.1846 CenterZ=0 NormalX=0 NormalY=0 NormalZ=1 AngleXU=0 Radius=5 StartAngle=0.629894 EndAngle=1.5708
    g27: ArcOfCircle CenterX=66.5 CenterY=38.0679 CenterZ=0 NormalX=0 NormalY=0 NormalZ=1 AngleXU=0 Radius=2 StartAngle=1.1e-15 EndAngle=0.629894
    g28: ArcOfCircle CenterX=-66.5 CenterY=38.0679 CenterZ=0 NormalX=0 NormalY=0 NormalZ=1 AngleXU=0 Radius=2 StartAngle=2.5117 EndAngle=3.14159
    g29: GeomPoint X=-75.5 Y=41 Z=0
    g30: LineSegment StartX=-29.0404 StartY=108.13 StartZ=0 EndX=-21.7676 EndY=102.828 EndZ=0
    g31: ArcOfCircle CenterX=-66.5 CenterY=-23.9966 CenterZ=0 NormalX=0 NormalY=0 NormalZ=1 AngleXU=0 Radius=2 StartAngle=3.14159 EndAngle=3.99797
    g32: ArcOfCircle CenterX=66.5 CenterY=-23.9966 CenterZ=0 NormalX=0 NormalY=0 NormalZ=1 AngleXU=0 Radius=2 StartAngle=5.42681 EndAngle=6.28319
    g33: LineSegment StartX=0 StartY=0 StartZ=0 EndX=77.5 EndY=0 EndZ=0
    g34: LineSegment StartX=0 StartY=0 StartZ=0 EndX=-77.5 EndY=0 EndZ=0
    g35: ArcOfCircle CenterX=0 CenterY=52.6846 CenterZ=0 NormalX=0 NormalY=0 NormalZ=1 AngleXU=0 Radius=103.5 StartAngle=3.99798 EndAngle=5.4268
    g36: LineSegment StartX=-3 StartY=101.185 StartZ=0 EndX=20.4232 EndY=101.185 EndZ=0
    g37: LineSegment StartX=-68.1162 StartY=39.246 StartZ=0 EndX=-32.0129 EndY=88.7736 EndZ=0
    g38: LineSegment StartX=-31.2048 StartY=89.1846 StartZ=0 EndX=-5 EndY=89.1846 EndZ=0
    g39: LineSegment StartX=-4 StartY=100.185 StartZ=0 EndX=-4 EndY=90.1846 EndZ=0
    g40: ArcOfCircle CenterX=-31.2048 CenterY=88.1846 CenterZ=0 NormalX=0 NormalY=0 NormalZ=1 AngleXU=0 Radius=1 StartAngle=1.5708 EndAngle=2.5117
    g41: ArcOfCircle CenterX=-5 CenterY=90.1846 CenterZ=0 NormalX=0 NormalY=0 NormalZ=1 AngleXU=0 Radius=1 StartAngle=4.71239 EndAngle=6.28319
    g42: ArcOfCircle CenterX=-3 CenterY=100.185 CenterZ=0 NormalX=0 NormalY=0 NormalZ=1 AngleXU=0 Radius=1 StartAngle=1.5708 EndAngle=3.14159
  constraints (106):
    c: PointOnObject(g0,g-2)
    c: Horizontal(g2)
    c: Coincident(g4,g-1)
    c: PointOnObject(g4,g-2)
    c: Tangent(g1,g5) = 1.5708
    c: Tangent(g2,g5) = 1.5708
    c: Tangent(g2,g6) = 1.5708
    c: Tangent(g3,g6) = 1.5708
    c: Equal(g6,g5)
    c: Symmetric(g2,g2,g4)
    c: PointOnObject(g7,g-2)
    c: PointOnObject(g7,g0)
    c: DistanceY(g7,g2) = 170
    c: Radius(g6) = 5
    c: DistanceX(g2,g2) = 50
    c: Vertical(g8)
    c: Vertical(g9)
    c: Vertical(g10)
    c: Vertical(g11)
    c: Equal(g1,g3)
    c: Tangent(g0,g12) = -1.5708
    c: Tangent(g9,g12) = 1.5708
    c: Tangent(g0,g13) = -1.5708
    c: Tangent(g10,g13) = 1.5708
    c: Equal(g12,g13)
    c: Radius(g12) = 2
    c: Tangent(g8,g14) = -1.5708
    c: Tangent(g3,g14) = 1.5708
    c: Tangent(g1,g15) = 1.5708
    c: Tangent(g11,g15) = 1.5708
    c: Equal(g14,g15)
    c: DistanceY(g9,g9) = 2
    c: DistanceY(g8,g8) = 15
    c: DistanceX(g10,g9) = 155
    c: Radius(g14) = 2
    c: Coincident(g16,g8)
    c: Coincident(g16,g9)
    c: Coincident(g17,g11)
    c: Coincident(g17,g10)
    c: PointOnObject(g18,g-2)
    c: Vertical(g19)
    c: Horizontal(g20)
    c: Vertical(g22)
    c: PointOnObject(g24,g4)
    c: Tangent(g21,g25) = 1.5708
    c: Tangent(g20,g25) = 1.5708
    c: Tangent(g20,g26) = 1.5708
    c: Tangent(g23,g26) = 1.5708
    c: Tangent(g22,g27) = -1.5708
    c: Tangent(g23,g27) = 1.5708
    c: Tangent(g19,g28) = 1.5708
    c: Tangent(g21,g28) = 1.5708
    c: DistanceY(g7,g18) = 9
    c: Symmetric(g20,g20,g24)
    c: DistanceY(g24,g4) = 9
    c: Radius(g26) = 5
    c: Equal(g26,g25)
    c: Parallel(g23,g3)
    c: DistanceX(g22,g8) = 9
    c: DistanceX(g11,g19) = 9
    c: Parallel(g21,g1)
    c: Coincident(g29,g15)
    c: PointOnObject(g30,g21)
    c: Perpendicular(g21,g30)
    c: Distance(g30) = 9
    c: Coincident(g30,g1)
    c: Tangent(g19,g31) = 1.5708
    c: Tangent(g22,g32) = -1.5708
    c: Radius(g32) = 2
    c: Equal(g32,g31)
    c: Equal(g28,g31)
    c: Equal(g27,g32)
    c: Coincident(g33,g-1)
    c: Diameter(g0) = 225
    c: Vertical(g16)
    c: Symmetric(g9,g8,g33)
    c: Symmetric(g10,g11,g34)
    c: DistanceY(g9,g8) = 52
    c: Equal(g17,g16)
    c: Symmetric(g34,g33,g-1)
    c: Coincident(g34,g-1)
    c: Vertical(g17)
    c: Horizontal(g33)
    c: Coincident(g35,g31)
    c: Coincident(g35,g32)
    c: PointOnObject(g18,g35)
    c: Tangent(g32,g35)
    c: Tangent(g31,g35)
    c: Horizontal(g36)
    c: Coincident(g37,g28)
    c: Coincident(g36,g26)
    c: Horizontal(g38)
    c: Vertical(g39)
    c: Tangent(g38,g40) = 1.5708
    c: Tangent(g37,g40) = 1.5708
    c: Tangent(g38,g41) = -1.5708
    c: Tangent(g39,g41) = 1.5708
    c: Tangent(g39,g42) = -1.5708
    c: Tangent(g36,g42) = 1.5708
    c: PointOnObject(g37,g21)
    c: Equal(g42,g41)
    c: Equal(g41,g40)
    c: Radius(g42) = 1
    c: DistanceY(g38,g4) = 21
    c: DistanceX(g2,g39) = 21
    c: Coincident(g35,g0)
FEATURE [Sketcher::SketchObject] Sketch012  label="Sketch_TopBrackStr_LoftStart"
  FullyConstrained = true
  MapMode = 5
  Placement = pos=(0,0,35) rot=(0,0,1;0rad)
  Support = -> [DatumPlane003]
  expr: Constraints[92] = <<params>>.shell_overhang_leng + <<params>>.shell_topbrack_width
  expr: Constraints[42] = <<params>>.shell_wall_thick + <<params>>.shell_topbrack_angend_overhang
  expr: Constraints[78] = <<params>>.shell_wall_thick + <<params>>.shell_topbrack_angend_overhang
  expr: Constraints[13] = <<params>>.tail_rad
  expr: Constraints[33] = <<params>>.plate_width
  expr: Constraints[62] = <<params>>.shell_overhang_leng + <<params>>.shell_topbrack_width
  expr: Constraints[177] = <<params>>.top_brack_front_leng
  expr: Constraints[48] = <<params>>.shell_wall_thick + <<params>>.shell_topbrack_angend_overhang
  expr: Constraints[34] = <<params>>.std_rad
  expr: Constraints[61] = <<params>>.shell_wall_thick + <<params>>.shell_topbrack_angend_overhang
  expr: Constraints[14] = <<params>>.tail_width
  expr: Constraints[75] = <<params>>.shell_topbrack_angend_overhang + <<params>>.shell_wall_thick
  expr: Constraints[41] = <<params>>.shell_wall_thick + <<params>>.shell_topbrack_angend_overhang
  expr: Constraints[108] = <<params>>.front_diameter
  expr: Constraints[12] = <<params>>.plate_length
  expr: Constraints[60] = <<params>>.std_rad / 2
  expr: Constraints[118] = <<params>>.wheel_well_clearance + 2 * <<params>>.std_rad
  expr: Constraints[31] = <<params>>.front_vert_edge
  expr: Constraints[25] = <<params>>.std_rad
  expr: Constraints[32] = <<params>>.back_vert_edge
  sketch-geometry (73):
    g0: ArcOfCircle CenterX=0 CenterY=52.6846 CenterZ=0 NormalX=0 NormalY=0 NormalZ=1 AngleXU=0 Radius=112.5 StartAngle=3.96017 EndAngle=5.4646
    g1: LineSegment StartX=-77.1162 StartY=42.1781 StartZ=0 EndX=-29.0404 EndY=108.13 EndZ=0
    g2: LineSegment StartX=-25 StartY=110.185 StartZ=0 EndX=25 EndY=110.185 EndZ=0
    g3: LineSegment StartX=29.0404 StartY=108.13 StartZ=0 EndX=77.1162 EndY=42.1781 EndZ=0
    g4: LineSegment StartX=0 StartY=0 StartZ=0 EndX=0 EndY=110.185 EndZ=0
    g5: ArcOfCircle CenterX=-25 CenterY=105.185 CenterZ=0 NormalX=0 NormalY=0 NormalZ=1 AngleXU=0 Radius=5 StartAngle=1.5708 EndAngle=2.5117
    g6: ArcOfCircle CenterX=25 CenterY=105.185 CenterZ=0 NormalX=0 NormalY=0 NormalZ=1 AngleXU=0 Radius=5 StartAngle=0.629894 EndAngle=1.5708
    g7: GeomPoint X=0 Y=-59.8154 Z=0
    g8: LineSegment StartX=77.5 StartY=26 StartZ=0 EndX=77.5 EndY=41 EndZ=0
    g9: LineSegment StartX=77.5 StartY=-26 StartZ=0 EndX=77.5 EndY=-28 EndZ=0
    g10: LineSegment StartX=-77.5 StartY=-28 StartZ=0 EndX=-77.5 EndY=-26 EndZ=0
    g11: LineSegment StartX=-77.5 StartY=26 StartZ=0 EndX=-77.5 EndY=41 EndZ=0
    g12: ArcOfCircle CenterX=75.5 CenterY=-28 CenterZ=0 NormalX=0 NormalY=0 NormalZ=1 AngleXU=0 Radius=2 StartAngle=5.4646 EndAngle=6.28319
    g13: ArcOfCircle CenterX=-75.5 CenterY=-28 CenterZ=0 NormalX=0 NormalY=0 NormalZ=1 AngleXU=0 Radius=2 StartAngle=3.14159 EndAngle=3.96017
    g14: ArcOfCircle CenterX=75.5 CenterY=41 CenterZ=0 NormalX=0 NormalY=0 NormalZ=1 AngleXU=0 Radius=2 StartAngle=1.4e-15 EndAngle=0.629894
    g15: ArcOfCircle CenterX=-75.5 CenterY=41 CenterZ=0 NormalX=0 NormalY=0 NormalZ=1 AngleXU=0 Radius=2 StartAngle=2.5117 EndAngle=3.14159
    g16: ArcOfCircle CenterX=0 CenterY=52.6846 CenterZ=0 NormalX=0 NormalY=0 NormalZ=1 AngleXU=0 Radius=99.5625 StartAngle=4.01626 EndAngle=5.40852
    g17: GeomPoint X=0 Y=-46.8779 Z=0
    g18: LineSegment StartX=-64.5625 StartY=-22.1778 StartZ=0 EndX=-64.5625 EndY=26 EndZ=0
    g19: LineSegment StartX=-14.3322 StartY=97.2471 StartZ=0 EndX=-1 EndY=97.2471 EndZ=0
    g20: LineSegment StartX=-56.3081 StartY=48.7603 StartZ=0 EndX=-27.1403 EndY=88.7736 EndZ=0
    g21: LineSegment StartX=64.5625 StartY=-22.1778 StartZ=0 EndX=64.5625 EndY=26 EndZ=0
    g22: LineSegment StartX=27.1403 StartY=88.7736 StartZ=0 EndX=56.3081 EndY=48.7603 EndZ=0
    g23: GeomPoint X=0 Y=97.2471 Z=0
    g24: GeomPoint X=-75.5 Y=41 Z=0
    g25: LineSegment StartX=-29.0404 StartY=108.13 StartZ=0 EndX=-18.5858 EndY=100.509 EndZ=0
    g26: LineSegment StartX=63.5625 StartY=27 StartZ=0 EndX=57.5 EndY=27 EndZ=0
    g27: LineSegment StartX=56.5 StartY=28 StartZ=0 EndX=56.5 EndY=48.1713 EndZ=0
    g28: ArcOfCircle CenterX=55.5 CenterY=48.1713 CenterZ=0 NormalX=0 NormalY=0 NormalZ=1 AngleXU=0 Radius=1 StartAngle=-9e-16 EndAngle=0.629894
    g29: ArcOfCircle CenterX=57.5 CenterY=28 CenterZ=0 NormalX=0 NormalY=0 NormalZ=1 AngleXU=0 Radius=1 StartAngle=3.14159 EndAngle=4.71239
    g30: ArcOfCircle CenterX=63.5625 CenterY=26 CenterZ=0 NormalX=0 NormalY=0 NormalZ=1 AngleXU=0 Radius=1 StartAngle=-9e-16 EndAngle=1.5708
    g31: LineSegment StartX=-56.5 StartY=48.1713 StartZ=0 EndX=-56.5 EndY=28 EndZ=0
    g32: LineSegment StartX=-63.5625 StartY=27 StartZ=0 EndX=-57.5 EndY=27 EndZ=0
    g33: ArcOfCircle CenterX=-63.5625 CenterY=26 CenterZ=0 NormalX=0 NormalY=0 NormalZ=1 AngleXU=0 Radius=1 StartAngle=1.5708 EndAngle=3.14159
    g34: ArcOfCircle CenterX=-57.5 CenterY=28 CenterZ=0 NormalX=0 NormalY=0 NormalZ=1 AngleXU=0 Radius=1 StartAngle=4.71239 EndAngle=6.28319
    g35: ArcOfCircle CenterX=-55.5 CenterY=48.1713 CenterZ=0 NormalX=0 NormalY=0 NormalZ=1 AngleXU=0 Radius=1 StartAngle=2.5117 EndAngle=3.14159
    g36: LineSegment StartX=27.1403 StartY=88.7736 StartZ=0 EndX=37.5949 EndY=96.3946 EndZ=0
    g37: LineSegment StartX=0 StartY=96.2471 StartZ=0 EndX=0 EndY=90.1846 EndZ=0
    g38: LineSegment StartX=1 StartY=89.1846 StartZ=0 EndX=26.3322 EndY=89.1846 EndZ=0
    g39: ArcOfCircle CenterX=-1 CenterY=96.2471 CenterZ=0 NormalX=0 NormalY=0 NormalZ=1 AngleXU=0 Radius=1 StartAngle=4.9e-15 EndAngle=1.5708
    g40: ArcOfCircle CenterX=1 CenterY=90.1846 CenterZ=0 NormalX=0 NormalY=0 NormalZ=1 AngleXU=0 Radius=1 StartAngle=3.14159 EndAngle=4.71239
    g41: ArcOfCircle CenterX=26.3322 CenterY=88.1846 CenterZ=0 NormalX=0 NormalY=0 NormalZ=1 AngleXU=0 Radius=1 StartAngle=0.629894 EndAngle=1.5708
    g42: LineSegment StartX=-26.3322 StartY=89.1846 StartZ=0 EndX=-16.3322 EndY=89.1846 EndZ=0
    g43: LineSegment StartX=-15.3322 StartY=90.1846 StartZ=0 EndX=-15.3322 EndY=96.2471 EndZ=0
    g44: ArcOfCircle CenterX=-14.3322 CenterY=96.2471 CenterZ=0 NormalX=0 NormalY=0 NormalZ=1 AngleXU=0 Radius=1 StartAngle=1.5708 EndAngle=3.14159
    g45: ArcOfCircle CenterX=-16.3322 CenterY=90.1846 CenterZ=0 NormalX=0 NormalY=0 NormalZ=1 AngleXU=0 Radius=1 StartAngle=4.71239 EndAngle=6.28319
    g46: ArcOfCircle CenterX=-26.3322 CenterY=88.1846 CenterZ=0 NormalX=0 NormalY=0 NormalZ=1 AngleXU=0 Radius=1 StartAngle=1.5708 EndAngle=2.5117
    g47: ArcOfCircle CenterX=62.5625 CenterY=-22.1778 CenterZ=0 NormalX=0 NormalY=0 NormalZ=1 AngleXU=0 Radius=2 StartAngle=5.40852 EndAngle=6.28319
    g48: ArcOfCircle CenterX=-62.5625 CenterY=-22.1778 CenterZ=0 NormalX=0 NormalY=0 NormalZ=1 AngleXU=0 Radius=2 StartAngle=3.14159 EndAngle=4.01626
    g49: LineSegment StartX=77.5 StartY=26 StartZ=0 EndX=77.5 EndY=-26 EndZ=0
    g50: LineSegment StartX=-77.5 StartY=26 StartZ=0 EndX=-77.5 EndY=-26 EndZ=0
    g51: GeomPoint X=77.5 Y=0 Z=0
    g52: GeomPoint X=-77.5 Y=0 Z=0
    g53: LineSegment StartX=64.5625 StartY=26 StartZ=0 EndX=77.5 EndY=26 EndZ=0
    g54: LineSegment StartX=-64.5625 StartY=26 StartZ=0 EndX=-64.5625 EndY=-17 EndZ=0
    g55: LineSegment StartX=-63.5625 StartY=-18 StartZ=0 EndX=-57.5 EndY=-18 EndZ=0
    g56: LineSegment StartX=-56.5 StartY=-19 StartZ=0 EndX=-56.5 EndY=-28.7667 EndZ=0
    g57: LineSegment StartX=64.5625 StartY=26 StartZ=0 EndX=64.5625 EndY=-17 EndZ=0
    g58: LineSegment StartX=63.5625 StartY=-18 StartZ=0 EndX=57.5 EndY=-18 EndZ=0
    g59: LineSegment StartX=56.5 StartY=-19 StartZ=0 EndX=56.5 EndY=-28.7667 EndZ=0
    g60: ArcOfCircle CenterX=-63.5625 CenterY=-17 CenterZ=0 NormalX=0 NormalY=0 NormalZ=1 AngleXU=0 Radius=1 StartAngle=3.14159 EndAngle=4.71239
    g61: ArcOfCircle CenterX=-57.5 CenterY=-19 CenterZ=0 NormalX=0 NormalY=0 NormalZ=1 AngleXU=0 Radius=1 StartAngle=1.1e-15 EndAngle=1.5708
    g62: ArcOfCircle CenterX=57.5 CenterY=-19 CenterZ=0 NormalX=0 NormalY=0 NormalZ=1 AngleXU=0 Radius=1 StartAngle=1.5708 EndAngle=3.14159
    g63: ArcOfCircle CenterX=63.5625 CenterY=-17 CenterZ=0 NormalX=0 NormalY=0 NormalZ=1 AngleXU=0 Radius=1 StartAngle=4.71239 EndAngle=6.28319
    g64: ArcOfCircle CenterX=0 CenterY=52.6846 CenterZ=0 NormalX=0 NormalY=0 NormalZ=1 AngleXU=0 Radius=99.5625 StartAngle=4.11426 EndAngle=5.31051
    g65: ArcOfCircle CenterX=-55.5 CenterY=-28.7667 CenterZ=0 NormalX=0 NormalY=0 NormalZ=1 AngleXU=0 Radius=1 StartAngle=3.14159 EndAngle=4.11426
    g66: ArcOfCircle CenterX=55.5 CenterY=-28.7667 CenterZ=0 NormalX=0 NormalY=0 NormalZ=1 AngleXU=0 Radius=1 StartAngle=5.31051 EndAngle=6.28319
    g67: LineSegment StartX=-57.5 StartY=27 StartZ=0 EndX=-57.5 EndY=-18 EndZ=0
    g68: LineSegment StartX=-56.5 StartY=-19 StartZ=0 EndX=56.5 EndY=-19 EndZ=0
    g69: LineSegment StartX=57.5 StartY=-18 StartZ=0 EndX=57.5 EndY=27 EndZ=0
    g70: LineSegment StartX=-27.1403 StartY=88.7736 StartZ=0 EndX=-22.4613 EndY=95.1924 EndZ=0
    g71: LineSegment StartX=-14.3322 StartY=97.2471 StartZ=0 EndX=-18.4209 EndY=97.2471 EndZ=0
    g72: ArcOfCircle CenterX=-18.4209 CenterY=92.2471 CenterZ=0 NormalX=0 NormalY=0 NormalZ=1 AngleXU=0 Radius=5 StartAngle=1.5708 EndAngle=2.5117
  constraints (178):
    c: PointOnObject(g0,g-2)
    c: Horizontal(g2)
    c: Coincident(g4,g-1)
    c: PointOnObject(g4,g-2)
    c: Tangent(g1,g5) = 1.5708
    c: Tangent(g2,g5) = 1.5708
    c: Tangent(g2,g6) = 1.5708
    c: Tangent(g3,g6) = 1.5708
    c: Equal(g6,g5)
    c: Symmetric(g2,g2,g4)
    c: PointOnObject(g7,g-2)
    c: PointOnObject(g7,g0)
    c: DistanceY(g7,g2) = 170
    c: Radius(g6) = 5
    c: DistanceX(g2,g2) = 50
    c: Vertical(g8)
    c: Vertical(g9)
    c: Vertical(g10)
    c: Vertical(g11)
    c: Equal(g1,g3)
    c: Tangent(g0,g12) = -1.5708
    c: Tangent(g9,g12) = 1.5708
    c: Tangent(g0,g13) = -1.5708
    c: Tangent(g10,g13) = 1.5708
    c: Equal(g12,g13)
    c: Radius(g12) = 2
    c: Tangent(g8,g14) = -1.5708
    c: Tangent(g3,g14) = 1.5708
    c: Tangent(g1,g15) = 1.5708
    c: Tangent(g11,g15) = 1.5708
    c: Equal(g14,g15)
    c: DistanceY(g9,g9) = 2
    c: DistanceY(g8,g8) = 15
    c: DistanceX(g10,g9) = 155
    c: Radius(g14) = 2
    c: PointOnObject(g17,g-2)
    c: PointOnObject(g17,g16)
    c: Vertical(g18)
    c: Horizontal(g19)
    c: Vertical(g21)
    c: PointOnObject(g23,g4)
    c: DistanceY(g7,g17) = 12.9375
    c: DistanceY(g23,g4) = 12.9375
    c: Parallel(g22,g3)
    c: Parallel(g20,g1)
    c: Coincident(g24,g15)
    c: PointOnObject(g25,g20)
    c: Perpendicular(g20,g25)
    c: Distance(g25) = 12.9375
    c: Coincident(g25,g1)
    c: Horizontal(g26)
    c: Vertical(g27)
    c: Tangent(g27,g28) = -1.5708
    c: Tangent(g22,g28) = 1.5708
    c: Tangent(g27,g29) = 1.5708
    c: Tangent(g26,g29) = 1.5708
    c: Tangent(g21,g30) = -1.5708
    c: Tangent(g26,g30) = -1.5708
    c: Equal(g28,g29)
    c: Equal(g30,g29)
    c: Radius(g30) = 1
    c: DistanceX(g21,g8) = 12.9375
    c: DistanceX(g27,g8) = 21
    c: Vertical(g31)
    c: Horizontal(g32)
    c: Tangent(g18,g33) = 1.5708
    c: Tangent(g32,g33) = 1.5708
    c: Tangent(g32,g34) = -1.5708
    c: Tangent(g31,g34) = 1.5708
    c: Tangent(g31,g35) = -1.5708
    c: Tangent(g20,g35) = 1.5708
    c: Equal(g35,g34)
    c: Equal(g34,g33)
    c: Equal(g35,g28)
    c: Equal(g32,g26)
    c: DistanceX(g11,g18) = 12.9375
    c: PointOnObject(g36,g3)
    c: Perpendicular(g36,g22)
    c: Distance(g36) = 12.9375
    c: PointOnObject(g23,g19)
    c: Vertical(g37)
    c: Horizontal(g38)
    c: Tangent(g19,g39) = 1.5708
    c: Tangent(g37,g39) = 1.5708
    c: Tangent(g37,g40) = -1.5708
    c: Tangent(g38,g40) = -1.5708
    c: Tangent(g38,g41) = 1.5708
    c: Tangent(g22,g41) = 1.5708
    c: Coincident(g36,g22)
    c: Equal(g28,g41)
    c: Equal(g41,g40)
    c: Equal(g40,g39)
    c: DistanceY(g38,g4) = 21
    c: Horizontal(g42)
    c: Vertical(g43)
    c: Tangent(g43,g44) = 1.5708
    c: Tangent(g19,g44) = 1.5708
    c: Tangent(g42,g45) = -1.5708
    c: Tangent(g43,g45) = -1.5708
    c: Tangent(g42,g46) = 1.5708
    c: Tangent(g20,g46) = 1.5708
    c: Equal(g46,g45)
    c: Equal(g45,g44)
    c: Equal(g44,g39)
    c: Equal(g43,g37)
    c: Tangent(g21,g47) = -1.5708
    c: Tangent(g18,g48) = 1.5708
    c: Equal(g48,g13)
    c: Diameter(g0) = 225
    c: Coincident(g49,g8)
    c: Coincident(g49,g9)
    c: Vertical(g49)
    c: Coincident(g50,g11)
    c: Coincident(g50,g10)
    c: Vertical(g50)
    c: PointOnObject(g51,g-1)
    c: Symmetric(g8,g9,g51)
    c: Symmetric(g11,g10,g52)
    c: DistanceY(g9,g8) = 52
    c: Equal(g49,g50)
    c: Symmetric(g52,g51,g-1)
    c: Equal(g12,g47)
    c: Coincident(g53,g21)
    c: Coincident(g53,g8)
    c: Horizontal(g53)
    c: Equal(g31,g27)
    c: Coincident(g16,g48)
    c: Tangent(g48,g16)
    c: Coincident(g47,g16)
    c: Tangent(g47,g16)
    c: Coincident(g54,g33)
    c: Horizontal(g55)
    c: Vertical(g56)
    c: Coincident(g57,g30)
    c: Horizontal(g58)
    c: Vertical(g59)
    c: Tangent(g54,g60) = -1.5708
    c: Tangent(g55,g60) = -1.5708
    c: Tangent(g55,g61) = 1.5708
    c: Tangent(g56,g61) = 1.5708
    c: Tangent(g59,g62) = -1.5708
    c: Tangent(g58,g62) = -1.5708
    c: Tangent(g58,g63) = 1.5708
    c: Tangent(g57,g63) = 1.5708
    c: Coincident(g64,g16)
    c: Tangent(g56,g65) = -1.5708
    c: Tangent(g64,g65) = -1.5708
    c: Tangent(g64,g66) = -1.5708
    c: Tangent(g59,g66) = 1.5708
    c: Equal(g63,g62)
    c: Equal(g62,g66)
    c: Equal(g66,g65)
    c: Equal(g65,g61)
    c: Equal(g60,g61)
    c: PointOnObject(g54,g18)
    c: PointOnObject(g17,g64)
    c: Coincident(g67,g32)
    c: Coincident(g67,g55)
    c: Vertical(g67)
    c: PointOnObject(g57,g21)
    c: Equal(g29,g63)
    c: Coincident(g68,g56)
    c: Coincident(g68,g59)
    c: Horizontal(g68)
    c: Coincident(g69,g58)
    c: Coincident(g69,g26)
    c: Vertical(g69)
    c: PointOnObject(g37,g4)
    c: Coincident(g70,g20)
    c: Coincident(g71,g19)
    c: Horizontal(g71)
    c: Parallel(g20,g70)
    c: Tangent(g70,g72) = 1.5708
    c: Tangent(g71,g72) = -1.5708
    c: Equal(g5,g72)
    c: Distance(g42) = 10
    c: Coincident(g64,g0)
    c: DistanceY(g9,g58) = 10
FEATURE [Sketcher::SketchObject] Sketch013  label="Sketch_TopBrackStr_LoftEnd"
  FullyConstrained = true
  MapMode = 5
  Placement = pos=(0,0,42) rot=(0,0,1;0rad)
  Support = -> [DatumPlane]
  expr: Constraints[74] = <<params>>.shell_overhang_leng + <<params>>.shell_wall_thick
  expr: Constraints[32] = <<params>>.back_vert_edge
  expr: Constraints[107] = <<params>>.front_diameter
  expr: Constraints[12] = <<params>>.plate_length
  expr: Constraints[31] = <<params>>.front_vert_edge
  expr: Constraints[25] = <<params>>.std_rad
  expr: Constraints[41] = <<params>>.shell_wall_thick + <<params>>.shell_overhang_leng
  expr: Constraints[14] = <<params>>.tail_width
  expr: Constraints[59] = <<params>>.std_rad / 2
  expr: Constraints[47] = <<params>>.shell_wall_thick + <<params>>.shell_overhang_leng
  expr: Constraints[174] = <<params>>.std_rad * 2
  expr: Constraints[178] = <<params>>.shell_overhang_leng + <<params>>.shell_wall_thick
  expr: Constraints[60] = <<params>>.shell_wall_thick + <<params>>.shell_overhang_leng
  expr: Constraints[34] = <<params>>.std_rad
  expr: Constraints[33] = <<params>>.plate_width
  expr: Constraints[180] = <<params>>.top_brack_front_leng
  expr: Constraints[117] = <<params>>.wheel_well_clearance + 2 * <<params>>.std_rad
  expr: Constraints[61] = <<params>>.shell_overhang_leng + <<params>>.shell_topbrack_width
  expr: Constraints[13] = <<params>>.tail_rad
  expr: Constraints[77] = <<params>>.shell_wall_thick + <<params>>.shell_overhang_leng
  expr: Constraints[91] = <<params>>.shell_overhang_leng + <<params>>.shell_topbrack_width
  sketch-geometry (74):
    g0: ArcOfCircle CenterX=0 CenterY=52.6846 CenterZ=0 NormalX=0 NormalY=0 NormalZ=1 AngleXU=0 Radius=112.5 StartAngle=3.96017 EndAngle=5.4646
    g1: LineSegment StartX=-77.1162 StartY=42.1781 StartZ=0 EndX=-29.0404 EndY=108.13 EndZ=0
    g2: LineSegment StartX=-25 StartY=110.185 StartZ=0 EndX=25 EndY=110.185 EndZ=0
    g3: LineSegment StartX=29.0404 StartY=108.13 StartZ=0 EndX=77.1162 EndY=42.1781 EndZ=0
    g4: LineSegment StartX=0 StartY=0 StartZ=0 EndX=0 EndY=110.185 EndZ=0
    g5: ArcOfCircle CenterX=-25 CenterY=105.185 CenterZ=0 NormalX=0 NormalY=0 NormalZ=1 AngleXU=0 Radius=5 StartAngle=1.5708 EndAngle=2.5117
    g6: ArcOfCircle CenterX=25 CenterY=105.185 CenterZ=0 NormalX=0 NormalY=0 NormalZ=1 AngleXU=0 Radius=5 StartAngle=0.629894 EndAngle=1.5708
    g7: GeomPoint X=0 Y=-59.8154 Z=0
    g8: LineSegment StartX=77.5 StartY=26 StartZ=0 EndX=77.5 EndY=41 EndZ=0
    g9: LineSegment StartX=77.5 StartY=-26 StartZ=0 EndX=77.5 EndY=-28 EndZ=0
    g10: LineSegment StartX=-77.5 StartY=-28 StartZ=0 EndX=-77.5 EndY=-26 EndZ=0
    g11: LineSegment StartX=-77.5 StartY=26 StartZ=0 EndX=-77.5 EndY=41 EndZ=0
    g12: ArcOfCircle CenterX=75.5 CenterY=-28 CenterZ=0 NormalX=0 NormalY=0 NormalZ=1 AngleXU=0 Radius=2 StartAngle=5.4646 EndAngle=6.28319
    g13: ArcOfCircle CenterX=-75.5 CenterY=-28 CenterZ=0 NormalX=0 NormalY=0 NormalZ=1 AngleXU=0 Radius=2 StartAngle=3.14159 EndAngle=3.96017
    g14: ArcOfCircle CenterX=75.5 CenterY=41 CenterZ=0 NormalX=0 NormalY=0 NormalZ=1 AngleXU=0 Radius=2 StartAngle=1.5e-15 EndAngle=0.629894
    g15: ArcOfCircle CenterX=-75.5 CenterY=41 CenterZ=0 NormalX=0 NormalY=0 NormalZ=1 AngleXU=0 Radius=2 StartAngle=2.5117 EndAngle=3.14159
    g16: ArcOfCircle CenterX=0 CenterY=52.6846 CenterZ=0 NormalX=0 NormalY=0 NormalZ=1 AngleXU=0 Radius=96.5 StartAngle=4.03131 EndAngle=5.39347
    g17: GeomPoint X=0 Y=-43.8154 Z=0
    g18: LineSegment StartX=-61.5 StartY=-20.732 StartZ=0 EndX=-61.5 EndY=26 EndZ=0
    g19: LineSegment StartX=-10.5424 StartY=94.1846 StartZ=0 EndX=-1 EndY=94.1846 EndZ=0
    g20: LineSegment StartX=-56.3081 StartY=43.5613 StartZ=0 EndX=-23.3505 EndY=88.7736 EndZ=0
    g21: LineSegment StartX=61.5 StartY=-20.732 StartZ=0 EndX=61.5 EndY=26 EndZ=0
    g22: LineSegment StartX=23.3505 StartY=88.7736 StartZ=0 EndX=56.3081 EndY=43.5613 EndZ=0
    g23: GeomPoint X=0 Y=94.1846 Z=0
    g24: GeomPoint X=-75.5 Y=41 Z=0
    g25: LineSegment StartX=-29.0404 StartY=108.13 StartZ=0 EndX=-16.111 EndY=98.7049 EndZ=0
    g26: LineSegment StartX=60.5 StartY=27 StartZ=0 EndX=57.5 EndY=27 EndZ=0
    g27: LineSegment StartX=56.5 StartY=28 StartZ=0 EndX=56.5 EndY=42.9723 EndZ=0
    g28: ArcOfCircle CenterX=55.5 CenterY=42.9723 CenterZ=0 NormalX=0 NormalY=0 NormalZ=1 AngleXU=0 Radius=1 StartAngle=3.2e-15 EndAngle=0.629894
    g29: ArcOfCircle CenterX=57.5 CenterY=28 CenterZ=0 NormalX=0 NormalY=0 NormalZ=1 AngleXU=0 Radius=1 StartAngle=3.14159 EndAngle=4.71239
    g30: ArcOfCircle CenterX=60.5 CenterY=26 CenterZ=0 NormalX=0 NormalY=0 NormalZ=1 AngleXU=0 Radius=1 StartAngle=3e-16 EndAngle=1.5708
    g31: LineSegment StartX=-56.5 StartY=42.9723 StartZ=0 EndX=-56.5 EndY=28 EndZ=0
    g32: LineSegment StartX=-60.5 StartY=27 StartZ=0 EndX=-57.5 EndY=27 EndZ=0
    g33: ArcOfCircle CenterX=-60.5 CenterY=26 CenterZ=0 NormalX=0 NormalY=0 NormalZ=1 AngleXU=0 Radius=1 StartAngle=1.5708 EndAngle=3.14159
    g34: ArcOfCircle CenterX=-57.5 CenterY=28 CenterZ=0 NormalX=0 NormalY=0 NormalZ=1 AngleXU=0 Radius=1 StartAngle=4.71239 EndAngle=6.28319
    g35: ArcOfCircle CenterX=-55.5 CenterY=42.9723 CenterZ=0 NormalX=0 NormalY=0 NormalZ=1 AngleXU=0 Radius=1 StartAngle=2.5117 EndAngle=3.14159
    g36: LineSegment StartX=23.3505 StartY=88.7736 StartZ=0 EndX=36.2799 EndY=98.1986 EndZ=0
    g37: LineSegment StartX=0 StartY=93.1846 StartZ=0 EndX=0 EndY=90.1846 EndZ=0
    g38: LineSegment StartX=1 StartY=89.1846 StartZ=0 EndX=22.5424 EndY=89.1846 EndZ=0
    g39: ArcOfCircle CenterX=-1 CenterY=93.1846 CenterZ=0 NormalX=0 NormalY=0 NormalZ=1 AngleXU=0 Radius=1 StartAngle=-6.2e-15 EndAngle=1.5708
    g40: ArcOfCircle CenterX=1 CenterY=90.1846 CenterZ=0 NormalX=0 NormalY=0 NormalZ=1 AngleXU=0 Radius=1 StartAngle=3.14159 EndAngle=4.71239
    g41: ArcOfCircle CenterX=22.5424 CenterY=88.1846 CenterZ=0 NormalX=0 NormalY=0 NormalZ=1 AngleXU=0 Radius=1 StartAngle=0.629894 EndAngle=1.5708
    g42: LineSegment StartX=-22.5424 StartY=89.1846 StartZ=0 EndX=-12.5424 EndY=89.1846 EndZ=0
    g43: LineSegment StartX=-11.5424 StartY=90.1846 StartZ=0 EndX=-11.5424 EndY=93.1846 EndZ=0
    g44: ArcOfCircle CenterX=-10.5424 CenterY=93.1846 CenterZ=0 NormalX=0 NormalY=0 NormalZ=1 AngleXU=0 Radius=1 StartAngle=1.5708 EndAngle=3.14159
    g45: ArcOfCircle CenterX=-12.5424 CenterY=90.1846 CenterZ=0 NormalX=0 NormalY=0 NormalZ=1 AngleXU=0 Radius=1 StartAngle=4.71239 EndAngle=6.28319
    g46: ArcOfCircle CenterX=-22.5424 CenterY=88.1846 CenterZ=0 NormalX=0 NormalY=0 NormalZ=1 AngleXU=0 Radius=1 StartAngle=1.5708 EndAngle=2.5117
    g47: ArcOfCircle CenterX=59.5 CenterY=-20.732 CenterZ=0 NormalX=0 NormalY=0 NormalZ=1 AngleXU=0 Radius=2 StartAngle=5.39347 EndAngle=6.28319
    g48: ArcOfCircle CenterX=-59.5 CenterY=-20.732 CenterZ=0 NormalX=0 NormalY=0 NormalZ=1 AngleXU=0 Radius=2 StartAngle=3.14159 EndAngle=4.03131
    g49: LineSegment StartX=77.5 StartY=26 StartZ=0 EndX=77.5 EndY=-26 EndZ=0
    g50: LineSegment StartX=-77.5 StartY=26 StartZ=0 EndX=-77.5 EndY=-26 EndZ=0
    g51: GeomPoint X=77.5 Y=0 Z=0
    g52: GeomPoint X=-77.5 Y=0 Z=0
    g53: LineSegment StartX=61.5 StartY=26 StartZ=0 EndX=77.5 EndY=26 EndZ=0
    g54: LineSegment StartX=-60.5 StartY=-18 StartZ=0 EndX=-57.5 EndY=-18 EndZ=0
    g55: LineSegment StartX=-56.5 StartY=-19 StartZ=0 EndX=-56.5 EndY=-23.4732 EndZ=0
    g56: LineSegment StartX=-61.5 StartY=26 StartZ=0 EndX=-61.5 EndY=-17 EndZ=0
    g57: LineSegment StartX=60.5 StartY=-18 StartZ=0 EndX=57.5 EndY=-18 EndZ=0
    g58: LineSegment StartX=56.5 StartY=-19 StartZ=0 EndX=56.5 EndY=-23.4732 EndZ=0
    g59: LineSegment StartX=61.5 StartY=26 StartZ=0 EndX=61.5 EndY=-17 EndZ=0
    g60: ArcOfCircle CenterX=-60.5 CenterY=-17 CenterZ=0 NormalX=0 NormalY=0 NormalZ=1 AngleXU=0 Radius=1 StartAngle=3.14159 EndAngle=4.71239
    g61: ArcOfCircle CenterX=-57.5 CenterY=-19 CenterZ=0 NormalX=0 NormalY=0 NormalZ=1 AngleXU=0 Radius=1 StartAngle=-1.8e-15 EndAngle=1.5708
    g62: ArcOfCircle CenterX=60.5 CenterY=-17 CenterZ=0 NormalX=0 NormalY=0 NormalZ=1 AngleXU=0 Radius=1 StartAngle=4.71239 EndAngle=6.28319
    g63: ArcOfCircle CenterX=57.5 CenterY=-19 CenterZ=0 NormalX=0 NormalY=0 NormalZ=1 AngleXU=0 Radius=1 StartAngle=1.5708 EndAngle=3.14159
    g64: ArcOfCircle CenterX=0 CenterY=52.6846 CenterZ=0 NormalX=0 NormalY=0 NormalZ=1 AngleXU=0 Radius=96.5 StartAngle=4.10884 EndAngle=5.31594
    g65: ArcOfCircle CenterX=-52.5 CenterY=-23.4732 CenterZ=0 NormalX=0 NormalY=0 NormalZ=1 AngleXU=0 Radius=4 StartAngle=3.14159 EndAngle=4.10884
    g66: ArcOfCircle CenterX=52.5 CenterY=-23.4732 CenterZ=0 NormalX=0 NormalY=0 NormalZ=1 AngleXU=0 Radius=4 StartAngle=5.31594 EndAngle=6.28319
    g67: LineSegment StartX=-57.5 StartY=27 StartZ=0 EndX=-57.5 EndY=-18 EndZ=0
    g68: LineSegment StartX=-56.5 StartY=-19 StartZ=0 EndX=56.5 EndY=-19 EndZ=0
    g69: LineSegment StartX=57.5 StartY=-18 StartZ=0 EndX=57.5 EndY=27 EndZ=0
    g70: LineSegment StartX=-23.3505 StartY=88.7736 StartZ=0 EndX=-20.9039 EndY=92.1299 EndZ=0
    g71: LineSegment StartX=-10.5424 StartY=94.1846 StartZ=0 EndX=-16.8635 EndY=94.1846 EndZ=0
    g72: ArcOfCircle CenterX=-16.8635 CenterY=89.1846 CenterZ=0 NormalX=0 NormalY=0 NormalZ=1 AngleXU=0 Radius=5 StartAngle=1.5708 EndAngle=2.5117
    g73: LineSegment StartX=-54.7703 StartY=-26.7665 StartZ=0 EndX=-63.8514 EndY=-39.9397 EndZ=0
  constraints (181):
    c: PointOnObject(g0,g-2)
    c: Horizontal(g2)
    c: Coincident(g4,g-1)
    c: PointOnObject(g4,g-2)
    c: Tangent(g1,g5) = 1.5708
    c: Tangent(g2,g5) = 1.5708
    c: Tangent(g2,g6) = 1.5708
    c: Tangent(g3,g6) = 1.5708
    c: Equal(g6,g5)
    c: Symmetric(g2,g2,g4)
    c: PointOnObject(g7,g-2)
    c: PointOnObject(g7,g0)
    c: DistanceY(g7,g2) = 170
    c: Radius(g6) = 5
    c: DistanceX(g2,g2) = 50
    c: Vertical(g8)
    c: Vertical(g9)
    c: Vertical(g10)
    c: Vertical(g11)
    c: Equal(g1,g3)
    c: Tangent(g0,g12) = -1.5708
    c: Tangent(g9,g12) = 1.5708
    c: Tangent(g0,g13) = -1.5708
    c: Tangent(g10,g13) = 1.5708
    c: Equal(g12,g13)
    c: Radius(g12) = 2
    c: Tangent(g8,g14) = -1.5708
    c: Tangent(g3,g14) = 1.5708
    c: Tangent(g1,g15) = 1.5708
    c: Tangent(g11,g15) = 1.5708
    c: Equal(g14,g15)
    c: DistanceY(g9,g9) = 2
    c: DistanceY(g8,g8) = 15
    c: DistanceX(g10,g9) = 155
    c: Radius(g14) = 2
    c: PointOnObject(g17,g-2)
    c: PointOnObject(g17,g16)
    c: Vertical(g18)
    c: Horizontal(g19)
    c: Vertical(g21)
    c: PointOnObject(g23,g4)
    c: DistanceY(g23,g4) = 16
    c: Parallel(g22,g3)
    c: Parallel(g20,g1)
    c: Coincident(g24,g15)
    c: PointOnObject(g25,g20)
    c: Perpendicular(g20,g25)
    c: Distance(g25) = 16
    c: Coincident(g25,g1)
    c: Horizontal(g26)
    c: Vertical(g27)
    c: Tangent(g27,g28) = -1.5708
    c: Tangent(g22,g28) = 1.5708
    c: Tangent(g27,g29) = 1.5708
    c: Tangent(g26,g29) = 1.5708
    c: Tangent(g21,g30) = -1.5708
    c: Tangent(g26,g30) = -1.5708
    c: Equal(g28,g29)
    c: Equal(g30,g29)
    c: Radius(g30) = 1
    c: DistanceX(g21,g8) = 16
    c: DistanceX(g27,g8) = 21
    c: Vertical(g31)
    c: Horizontal(g32)
    c: Tangent(g18,g33) = 1.5708
    c: Tangent(g32,g33) = 1.5708
    c: Tangent(g32,g34) = -1.5708
    c: Tangent(g31,g34) = 1.5708
    c: Tangent(g31,g35) = -1.5708
    c: Tangent(g20,g35) = 1.5708
    c: Equal(g35,g34)
    c: Equal(g34,g33)
    c: Equal(g35,g28)
    c: Equal(g32,g26)
    c: DistanceX(g11,g18) = 16
    c: PointOnObject(g36,g3)
    c: Perpendicular(g36,g22)
    c: Distance(g36) = 16
    c: PointOnObject(g23,g19)
    c: Vertical(g37)
    c: Horizontal(g38)
    c: Tangent(g19,g39) = 1.5708
    c: Tangent(g37,g39) = 1.5708
    c: Tangent(g37,g40) = -1.5708
    c: Tangent(g38,g40) = -1.5708
    c: Tangent(g38,g41) = 1.5708
    c: Tangent(g22,g41) = 1.5708
    c: Coincident(g36,g22)
    c: Equal(g28,g41)
    c: Equal(g41,g40)
    c: Equal(g40,g39)
    c: DistanceY(g38,g4) = 21
    c: Horizontal(g42)
    c: Vertical(g43)
    c: Tangent(g43,g44) = 1.5708
    c: Tangent(g19,g44) = 1.5708
    c: Tangent(g42,g45) = -1.5708
    c: Tangent(g43,g45) = -1.5708
    c: Tangent(g42,g46) = 1.5708
    c: Tangent(g20,g46) = 1.5708
    c: Equal(g46,g45)
    c: Equal(g45,g44)
    c: Equal(g44,g39)
    c: Equal(g43,g37)
    c: Tangent(g21,g47) = -1.5708
    c: Tangent(g18,g48) = 1.5708
    c: Equal(g48,g13)
    c: Diameter(g0) = 225
    c: Coincident(g49,g8)
    c: Coincident(g49,g9)
    c: Vertical(g49)
    c: Coincident(g50,g11)
    c: Coincident(g50,g10)
    c: Vertical(g50)
    c: PointOnObject(g51,g-1)
    c: Symmetric(g8,g9,g51)
    c: Symmetric(g11,g10,g52)
    c: DistanceY(g9,g8) = 52
    c: Equal(g49,g50)
    c: Symmetric(g52,g51,g-1)
    c: Equal(g12,g47)
    c: Coincident(g53,g21)
    c: Coincident(g53,g8)
    c: Horizontal(g53)
    c: Equal(g31,g27)
    c: Coincident(g16,g48)
    c: Tangent(g48,g16)
    c: Coincident(g16,g47)
    c: Tangent(g47,g16)
    c: Horizontal(g54)
    c: Vertical(g55)
    c: Vertical(g58)
    c: Horizontal(g57)
    c: Coincident(g59,g30)
    c: Coincident(g56,g33)
    c: Tangent(g54,g60) = -1.5708
    c: Tangent(g56,g60) = -1.5708
    c: Tangent(g54,g61) = 1.5708
    c: Tangent(g55,g61) = 1.5708
    c: Tangent(g57,g62) = 1.5708
    c: Tangent(g59,g62) = 1.5708
    c: Tangent(g57,g63) = -1.5708
    c: Tangent(g58,g63) = -1.5708
    c: Coincident(g64,g16)
    c: Tangent(g64,g65) = -1.5708
    c: Tangent(g55,g65) = -1.5708
    c: Tangent(g64,g66) = -1.5708
    c: Tangent(g58,g66) = 1.5708
    c: Equal(g62,g63)
    c: Equal(g60,g61)
    c: PointOnObject(g56,g18)
    c: PointOnObject(g59,g21)
    c: PointOnObject(g17,g64)
    c: Equal(g30,g62)
    c: Coincident(g67,g32)
    c: Coincident(g67,g54)
    c: Coincident(g68,g55)
    c: Coincident(g68,g58)
    c: Coincident(g69,g57)
    c: Coincident(g69,g26)
    c: Vertical(g69)
    c: Vertical(g67)
    c: Horizontal(g68)
    c: Coincident(g70,g20)
    c: Coincident(g71,g19)
    c: Horizontal(g71)
    c: Parallel(g70,g20)
    c: Tangent(g70,g72) = 1.5708
    c: Tangent(g71,g72) = -1.5708
    c: Equal(g5,g72)
    c: PointOnObject(g37,g4)
    c: Distance(g42) = 10
    c: Equal(g63,g61)
    c: Equal(g66,g65)
    c: Radius(g65) = 4
    c: Coincident(g73,g64)
    c: PointOnObject(g73,g0)
    c: Perpendicular(g0,g73)
    c: DistanceY(g7,g17) = 16
    c: Coincident(g64,g0)
    c: DistanceY(g9,g57) = 10
FEATURE [Sketcher::SketchObject] Sketch014  label="Sketch_OuterShell_Template"
  FullyConstrained = true
  MapMode = 5
  Support = -> [XY_Plane002]
  expr: Constraints[59] = <<params>>.std_rad
  expr: Constraints[41] = <<params>>.plate_width
  expr: Constraints[14] = <<params>>.tail_width
  expr: Constraints[13] = <<params>>.tail_rad
  expr: Constraints[32] = <<params>>.front_diameter
  expr: Constraints[29] = <<params>>.front_vert_edge
  expr: Constraints[12] = <<params>>.plate_length
  expr: Constraints[31] = <<params>>.std_rad
  expr: Constraints[30] = <<params>>.back_vert_edge
  expr: Constraints[61] = <<params>>.wheel_well_clearance
  expr: Constraints[23] = <<params>>.std_rad
  sketch-geometry (24):
    g0: ArcOfCircle CenterX=0 CenterY=52.6846 CenterZ=0 NormalX=0 NormalY=0 NormalZ=1 AngleXU=0 Radius=112.5 StartAngle=3.96017 EndAngle=5.4646
    g1: LineSegment StartX=-77.1162 StartY=42.1781 StartZ=0 EndX=-29.0404 EndY=108.13 EndZ=0
    g2: LineSegment StartX=-25 StartY=110.185 StartZ=0 EndX=25 EndY=110.185 EndZ=0
    g3: LineSegment StartX=29.0404 StartY=108.13 StartZ=0 EndX=77.1162 EndY=42.1781 EndZ=0
    g4: LineSegment StartX=0 StartY=0 StartZ=0 EndX=0 EndY=110.185 EndZ=0
    g5: ArcOfCircle CenterX=-25 CenterY=105.185 CenterZ=0 NormalX=0 NormalY=0 NormalZ=1 AngleXU=0 Radius=5 StartAngle=1.5708 EndAngle=2.5117
    g6: ArcOfCircle CenterX=25 CenterY=105.185 CenterZ=0 NormalX=0 NormalY=0 NormalZ=1 AngleXU=0 Radius=5 StartAngle=0.629895 EndAngle=1.5708
    g7: GeomPoint X=0 Y=-59.8154 Z=0
    g8: LineSegment StartX=77.5 StartY=26 StartZ=0 EndX=77.5 EndY=41 EndZ=0
    g9: LineSegment StartX=77.5 StartY=-26 StartZ=0 EndX=77.5 EndY=-28 EndZ=0
    g10: LineSegment StartX=-77.5 StartY=26 StartZ=0 EndX=-77.5 EndY=41 EndZ=0
    g11: ArcOfCircle CenterX=75.5 CenterY=-28 CenterZ=0 NormalX=0 NormalY=0 NormalZ=1 AngleXU=0 Radius=2 StartAngle=5.4646 EndAngle=6.28319
    g12: ArcOfCircle CenterX=-75.5 CenterY=-28 CenterZ=0 NormalX=0 NormalY=0 NormalZ=1 AngleXU=0 Radius=2 StartAngle=3.14159 EndAngle=3.96017
    g13: ArcOfCircle CenterX=75.5 CenterY=41 CenterZ=0 NormalX=0 NormalY=0 NormalZ=1 AngleXU=0 Radius=2 StartAngle=-9e-16 EndAngle=0.629895
    g14: ArcOfCircle CenterX=-75.5 CenterY=41 CenterZ=0 NormalX=0 NormalY=0 NormalZ=1 AngleXU=0 Radius=2 StartAngle=2.5117 EndAngle=3.14159
    g15: GeomPoint X=77.5 Y=0 Z=0
    g16: GeomPoint X=-77.5 Y=0 Z=0
    g17: LineSegment StartX=-77.5 StartY=-28 StartZ=0 EndX=-77.5 EndY=-26 EndZ=0
    g18: LineSegment StartX=-77.5 StartY=26 StartZ=0 EndX=-77.5 EndY=24 EndZ=0
    g19: LineSegment StartX=-77.5 StartY=24 StartZ=0 EndX=-77.5 EndY=-24 EndZ=0
    g20: LineSegment StartX=-77.5 StartY=-26 StartZ=0 EndX=-77.5 EndY=-24 EndZ=0
    g21: LineSegment StartX=77.5 StartY=26 StartZ=0 EndX=77.5 EndY=24 EndZ=0
    g22: LineSegment StartX=77.5 StartY=24 StartZ=0 EndX=77.5 EndY=-24 EndZ=0
    g23: LineSegment StartX=77.5 StartY=-24 StartZ=0 EndX=77.5 EndY=-26 EndZ=0
  constraints (62):
    c: PointOnObject(g0,g-2)
    c: Horizontal(g2)
    c: Coincident(g4,g-1)
    c: PointOnObject(g4,g-2)
    c: Tangent(g1,g5) = 1.5708
    c: Tangent(g2,g5) = 1.5708
    c: Tangent(g2,g6) = 1.5708
    c: Tangent(g3,g6) = 1.5708
    c: Equal(g6,g5)
    c: Symmetric(g2,g2,g4)
    c: PointOnObject(g7,g-2)
    c: PointOnObject(g7,g0)
    c: DistanceY(g7,g2) = 170
    c: Radius(g6) = 5
    c: DistanceX(g2,g2) = 50
    c: Vertical(g8)
    c: Vertical(g9)
    c: Vertical(g10)
    c: Equal(g1,g3)
    c: Tangent(g0,g11) = -1.5708
    c: Tangent(g9,g11) = 1.5708
    c: Tangent(g0,g12) = -1.5708
    c: Equal(g11,g12)
    c: Radius(g11) = 2
    c: Tangent(g8,g13) = -1.5708
    c: Tangent(g3,g13) = 1.5708
    c: Tangent(g1,g14) = 1.5708
    c: Tangent(g10,g14) = 1.5708
    c: Equal(g13,g14)
    c: DistanceY(g9,g9) = 2
    c: DistanceY(g8,g8) = 15
    c: Radius(g13) = 2
    c: Diameter(g0) = 225
    c: PointOnObject(g15,g-1)
    c: PointOnObject(g16,g-1)
    c: Symmetric(g10,g17,g16)
    c: Symmetric(g8,g9,g15)
    c: Coincident(g17,g12)
    c: Vertical(g17)
    c: Equal(g10,g8)
    c: Equal(g9,g17)
    c: DistanceX(g12,g9) = 155
    c: Coincident(g18,g10)
    c: Vertical(g18)
    c: Coincident(g19,g18)
    c: Vertical(g19)
    c: Coincident(g20,g17)
    c: Vertical(g20)
    c: Equal(g20,g18)
    c: Coincident(g19,g20)
    c: Tangent(g12,g17)
    c: Coincident(g21,g8)
    c: Vertical(g21)
    c: Coincident(g22,g21)
    c: Vertical(g22)
    c: Coincident(g23,g22)
    c: Coincident(g23,g9)
    c: Equal(g23,g21)
    c: Vertical(g23)
    c: DistanceY(g21,g8) = 2
    c: Equal(g18,g21)
    c: DistanceY(g22,g21) = 48
FEATURE [Sketcher::SketchObject] Sketch015  label="Sketch_MtHoles_BotPlate_Temp"
  FullyConstrained = true
  MapMode = 5
  Support = -> [XY_Plane002]
  expr: Constraints[23] = <<params>>.std_rad
  expr: Constraints[61] = <<params>>.wheel_well_clearance
  expr: Constraints[30] = <<params>>.back_vert_edge
  expr: Constraints[31] = <<params>>.std_rad
  expr: Constraints[12] = <<params>>.plate_length
  expr: Constraints[29] = <<params>>.front_vert_edge
  expr: Constraints[32] = <<params>>.front_diameter
  expr: Constraints[13] = <<params>>.tail_rad
  expr: Constraints[83] = <<params>>.shelltobot_back_offset_x
  expr: Constraints[14] = <<params>>.tail_width
  expr: Constraints[41] = <<params>>.plate_width
  expr: Constraints[59] = <<params>>.std_rad
  expr: Constraints[72] = <<params>>.shelltobot_frontmid_offset_xy
  expr: Constraints[76] = <<params>>.shelltobot_frontmid_offset_xy
  expr: Constraints[79] = <<params>>.shelltobot_back_offset_y
  sketch-geometry (33):
    g0: ArcOfCircle CenterX=0 CenterY=52.6846 CenterZ=0 NormalX=0 NormalY=0 NormalZ=1 AngleXU=0 Radius=112.5 StartAngle=3.96017 EndAngle=5.4646
    g1: LineSegment StartX=-77.1162 StartY=42.1781 StartZ=0 EndX=-29.0404 EndY=108.13 EndZ=0
    g2: LineSegment StartX=-25 StartY=110.185 StartZ=0 EndX=25 EndY=110.185 EndZ=0
    g3: LineSegment StartX=29.0404 StartY=108.13 StartZ=0 EndX=77.1162 EndY=42.1781 EndZ=0
    g4: LineSegment StartX=0 StartY=0 StartZ=0 EndX=0 EndY=110.185 EndZ=0
    g5: ArcOfCircle CenterX=-25 CenterY=105.185 CenterZ=0 NormalX=0 NormalY=0 NormalZ=1 AngleXU=0 Radius=5 StartAngle=1.5708 EndAngle=2.5117
    g6: ArcOfCircle CenterX=25 CenterY=105.185 CenterZ=0 NormalX=0 NormalY=0 NormalZ=1 AngleXU=0 Radius=5 StartAngle=0.629894 EndAngle=1.5708
    g7: GeomPoint X=0 Y=-59.8154 Z=0
    g8: LineSegment StartX=77.5 StartY=26 StartZ=0 EndX=77.5 EndY=41 EndZ=0
    g9: LineSegment StartX=77.5 StartY=-26 StartZ=0 EndX=77.5 EndY=-28 EndZ=0
    g10: LineSegment StartX=-77.5 StartY=26 StartZ=0 EndX=-77.5 EndY=41 EndZ=0
    g11: ArcOfCircle CenterX=75.5 CenterY=-28 CenterZ=0 NormalX=0 NormalY=0 NormalZ=1 AngleXU=0 Radius=2 StartAngle=5.4646 EndAngle=6.28319
    g12: ArcOfCircle CenterX=-75.5 CenterY=-28 CenterZ=0 NormalX=0 NormalY=0 NormalZ=1 AngleXU=0 Radius=2 StartAngle=3.14159 EndAngle=3.96017
    g13: ArcOfCircle CenterX=75.5 CenterY=41 CenterZ=0 NormalX=0 NormalY=0 NormalZ=1 AngleXU=0 Radius=2 StartAngle=8e-16 EndAngle=0.629894
    g14: ArcOfCircle CenterX=-75.5 CenterY=41 CenterZ=0 NormalX=0 NormalY=0 NormalZ=1 AngleXU=0 Radius=2 StartAngle=2.5117 EndAngle=3.14159
    g15: GeomPoint X=77.5 Y=0 Z=0
    g16: GeomPoint X=-77.5 Y=0 Z=0
    g17: LineSegment StartX=-77.5 StartY=-28 StartZ=0 EndX=-77.5 EndY=-26 EndZ=0
    g18: LineSegment StartX=-77.5 StartY=26 StartZ=0 EndX=-77.5 EndY=24 EndZ=0
    g19: LineSegment StartX=-77.5 StartY=24 StartZ=0 EndX=-77.5 EndY=-24 EndZ=0
    g20: LineSegment StartX=-77.5 StartY=-26 StartZ=0 EndX=-77.5 EndY=-24 EndZ=0
    g21: LineSegment StartX=77.5 StartY=26 StartZ=0 EndX=77.5 EndY=24 EndZ=0
    g22: LineSegment StartX=77.5 StartY=24 StartZ=0 EndX=77.5 EndY=-24 EndZ=0
    g23: LineSegment StartX=77.5 StartY=-24 StartZ=0 EndX=77.5 EndY=-26 EndZ=0
    g24: LineSegment StartX=-72.5 StartY=29 StartZ=0 EndX=72.5 EndY=29 EndZ=0
    g25: LineSegment StartX=-72.5 StartY=-28 StartZ=0 EndX=72.5 EndY=-28 EndZ=0
    g26: LineSegment StartX=-36.1217 StartY=90.1846 StartZ=0 EndX=36.1217 EndY=90.1846 EndZ=0
    g27: GeomPoint X=0 Y=90.1846 Z=0
    g28: GeomPoint X=0 Y=29 Z=0
    g29: GeomPoint X=0 Y=-28 Z=0
    g30: LineSegment StartX=72.5 StartY=-28 StartZ=0 EndX=72.5 EndY=29 EndZ=0
    g31: LineSegment StartX=72.5 StartY=-28 StartZ=0 EndX=77.5 EndY=-28 EndZ=0
    g32: LineSegment StartX=36.1217 StartY=90.1846 StartZ=0 EndX=42.1217 EndY=90.1846 EndZ=0
  constraints (84):
    c: PointOnObject(g0,g-2)
    c: Horizontal(g2)
    c: Coincident(g4,g-1)
    c: PointOnObject(g4,g-2)
    c: Tangent(g1,g5) = 1.5708
    c: Tangent(g2,g5) = 1.5708
    c: Tangent(g2,g6) = 1.5708
    c: Tangent(g3,g6) = 1.5708
    c: Equal(g6,g5)
    c: Symmetric(g2,g2,g4)
    c: PointOnObject(g7,g-2)
    c: PointOnObject(g7,g0)
    c: DistanceY(g7,g2) = 170
    c: Radius(g6) = 5
    c: DistanceX(g2,g2) = 50
    c: Vertical(g8)
    c: Vertical(g9)
    c: Vertical(g10)
    c: Equal(g1,g3)
    c: Tangent(g0,g11) = -1.5708
    c: Tangent(g9,g11) = 1.5708
    c: Tangent(g0,g12) = -1.5708
    c: Equal(g11,g12)
    c: Radius(g11) = 2
    c: Tangent(g8,g13) = -1.5708
    c: Tangent(g3,g13) = 1.5708
    c: Tangent(g1,g14) = 1.5708
    c: Tangent(g10,g14) = 1.5708
    c: Equal(g13,g14)
    c: DistanceY(g9,g9) = 2
    c: DistanceY(g8,g8) = 15
    c: Radius(g13) = 2
    c: Diameter(g0) = 225
    c: PointOnObject(g15,g-1)
    c: PointOnObject(g16,g-1)
    c: Symmetric(g10,g17,g16)
    c: Symmetric(g8,g9,g15)
    c: Coincident(g17,g12)
    c: Vertical(g17)
    c: Equal(g10,g8)
    c: Equal(g9,g17)
    c: DistanceX(g12,g9) = 155
    c: Coincident(g18,g10)
    c: Vertical(g18)
    c: Coincident(g19,g18)
    c: Vertical(g19)
    c: Coincident(g20,g17)
    c: Vertical(g20)
    c: Equal(g20,g18)
    c: Coincident(g19,g20)
    c: Tangent(g12,g17)
    c: Coincident(g21,g8)
    c: Vertical(g21)
    c: Coincident(g22,g21)
    c: Vertical(g22)
    c: Coincident(g23,g22)
    c: Coincident(g23,g9)
    c: Equal(g23,g21)
    c: Vertical(g23)
    c: DistanceY(g21,g8) = 2
    c: Equal(g18,g21)
    c: DistanceY(g22,g21) = 48
    c: Horizontal(g24)
    c: Horizontal(g25)
    c: Horizontal(g26)
    c: PointOnObject(g27,g4)
    c: PointOnObject(g28,g4)
    c: PointOnObject(g29,g-2)
    c: Vertical(g30)
    c: Symmetric(g25,g25,g29)
    c: Symmetric(g24,g24,g28)
    c: Symmetric(g26,g26,g27)
    c: DistanceX(g25,g9) = 5
    c: Coincident(g31,g25)
    c: Coincident(g31,g9)
    c: Horizontal(g31)
    c: DistanceY(g21,g24) = 5
    c: Coincident(g30,g24)
    c: Coincident(g30,g25)
    c: DistanceY(g26,g2) = 20
    c: Coincident(g32,g26)
    c: PointOnObject(g32,g3)
    c: Horizontal(g32)
    c: DistanceX(g26,g32) = 6
FEATURE [Sketcher::SketchObject] Sketch016  label="Sketch_MtHoles_BotPlate"
  FullyConstrained = true
  MapMode = 5
  Support = -> [XY_Plane002]
  expr: Constraints[79] = <<params>>.shelltobot_back_offset_y
  expr: Constraints[76] = <<params>>.shelltobot_frontmid_offset_xy
  expr: Constraints[72] = <<params>>.shelltobot_frontmid_offset_xy
  expr: Constraints[59] = <<params>>.std_rad
  expr: Constraints[41] = <<params>>.plate_width
  expr: Constraints[14] = <<params>>.tail_width
  expr: Constraints[83] = <<params>>.shelltobot_back_offset_x
  expr: Constraints[13] = <<params>>.tail_rad
  expr: Constraints[32] = <<params>>.front_diameter
  expr: Constraints[29] = <<params>>.front_vert_edge
  expr: Constraints[95] = <<params>>.m25_hole_clear_diam
  expr: Constraints[12] = <<params>>.plate_length
  expr: Constraints[31] = <<params>>.std_rad
  expr: Constraints[30] = <<params>>.back_vert_edge
  expr: Constraints[61] = <<params>>.wheel_well_clearance
  expr: Constraints[23] = <<params>>.std_rad
  sketch-geometry (39):
    g0: ArcOfCircle CenterX=0 CenterY=52.6846 CenterZ=0 NormalX=0 NormalY=0 NormalZ=1 AngleXU=0 Radius=112.5 StartAngle=3.96017 EndAngle=5.4646
    g1: LineSegment StartX=-77.1162 StartY=42.1781 StartZ=0 EndX=-29.0404 EndY=108.13 EndZ=0
    g2: LineSegment StartX=-25 StartY=110.185 StartZ=0 EndX=25 EndY=110.185 EndZ=0
    g3: LineSegment StartX=29.0404 StartY=108.13 StartZ=0 EndX=77.1162 EndY=42.1781 EndZ=0
    g4: LineSegment StartX=0 StartY=0 StartZ=0 EndX=0 EndY=110.185 EndZ=0
    g5: ArcOfCircle CenterX=-25 CenterY=105.185 CenterZ=0 NormalX=0 NormalY=0 NormalZ=1 AngleXU=0 Radius=5 StartAngle=1.5708 EndAngle=2.5117
    g6: ArcOfCircle CenterX=25 CenterY=105.185 CenterZ=0 NormalX=0 NormalY=0 NormalZ=1 AngleXU=0 Radius=5 StartAngle=0.629894 EndAngle=1.5708
    g7: GeomPoint X=0 Y=-59.8154 Z=0
    g8: LineSegment StartX=77.5 StartY=26 StartZ=0 EndX=77.5 EndY=41 EndZ=0
    g9: LineSegment StartX=77.5 StartY=-26 StartZ=0 EndX=77.5 EndY=-28 EndZ=0
    g10: LineSegment StartX=-77.5 StartY=26 StartZ=0 EndX=-77.5 EndY=41 EndZ=0
    g11: ArcOfCircle CenterX=75.5 CenterY=-28 CenterZ=0 NormalX=0 NormalY=0 NormalZ=1 AngleXU=0 Radius=2 StartAngle=5.4646 EndAngle=6.28319
    g12: ArcOfCircle CenterX=-75.5 CenterY=-28 CenterZ=0 NormalX=0 NormalY=0 NormalZ=1 AngleXU=0 Radius=2 StartAngle=3.14159 EndAngle=3.96017
    g13: ArcOfCircle CenterX=75.5 CenterY=41 CenterZ=0 NormalX=0 NormalY=0 NormalZ=1 AngleXU=0 Radius=2 StartAngle=8e-16 EndAngle=0.629894
    g14: ArcOfCircle CenterX=-75.5 CenterY=41 CenterZ=0 NormalX=0 NormalY=0 NormalZ=1 AngleXU=0 Radius=2 StartAngle=2.5117 EndAngle=3.14159
    g15: GeomPoint X=77.5 Y=0 Z=0
    g16: GeomPoint X=-77.5 Y=0 Z=0
    g17: LineSegment StartX=-77.5 StartY=-28 StartZ=0 EndX=-77.5 EndY=-26 EndZ=0
    g18: LineSegment StartX=-77.5 StartY=26 StartZ=0 EndX=-77.5 EndY=24 EndZ=0
    g19: LineSegment StartX=-77.5 StartY=24 StartZ=0 EndX=-77.5 EndY=-24 EndZ=0
    g20: LineSegment StartX=-77.5 StartY=-26 StartZ=0 EndX=-77.5 EndY=-24 EndZ=0
    g21: LineSegment StartX=77.5 StartY=26 StartZ=0 EndX=77.5 EndY=24 EndZ=0
    g22: LineSegment StartX=77.5 StartY=24 StartZ=0 EndX=77.5 EndY=-24 EndZ=0
    g23: LineSegment StartX=77.5 StartY=-24 StartZ=0 EndX=77.5 EndY=-26 EndZ=0
    g24: LineSegment StartX=-72.5 StartY=29 StartZ=0 EndX=72.5 EndY=29 EndZ=0
    g25: LineSegment StartX=-72.5 StartY=-28 StartZ=0 EndX=72.5 EndY=-28 EndZ=0
    g26: LineSegment StartX=-36.1217 StartY=90.1846 StartZ=0 EndX=36.1217 EndY=90.1846 EndZ=0
    g27: GeomPoint X=0 Y=90.1846 Z=0
    g28: GeomPoint X=0 Y=29 Z=0
    g29: GeomPoint X=0 Y=-28 Z=0
    g30: LineSegment StartX=72.5 StartY=-28 StartZ=0 EndX=72.5 EndY=29 EndZ=0
    g31: LineSegment StartX=72.5 StartY=-28 StartZ=0 EndX=77.5 EndY=-28 EndZ=0
    g32: LineSegment StartX=36.1217 StartY=90.1846 StartZ=0 EndX=42.1217 EndY=90.1846 EndZ=0
    g33: Circle CenterX=36.1217 CenterY=90.1846 CenterZ=0 NormalX=0 NormalY=0 NormalZ=1 AngleXU=0 Radius=1.4
    g34: Circle CenterX=-36.1217 CenterY=90.1846 CenterZ=0 NormalX=0 NormalY=0 NormalZ=1 AngleXU=0 Radius=1.4
    g35: Circle CenterX=72.5 CenterY=29 CenterZ=0 NormalX=0 NormalY=0 NormalZ=1 AngleXU=0 Radius=1.4
    g36: Circle CenterX=72.5 CenterY=-28 CenterZ=0 NormalX=0 NormalY=0 NormalZ=1 AngleXU=0 Radius=1.4
    g37: Circle CenterX=-72.5 CenterY=-28 CenterZ=0 NormalX=0 NormalY=0 NormalZ=1 AngleXU=0 Radius=1.4
    g38: Circle CenterX=-72.5 CenterY=29 CenterZ=0 NormalX=0 NormalY=0 NormalZ=1 AngleXU=0 Radius=1.4
  constraints (96):
    c: PointOnObject(g0,g-2)
    c: Horizontal(g2)
    c: Coincident(g4,g-1)
    c: PointOnObject(g4,g-2)
    c: Tangent(g1,g5) = 1.5708
    c: Tangent(g2,g5) = 1.5708
    c: Tangent(g2,g6) = 1.5708
    c: Tangent(g3,g6) = 1.5708
    c: Equal(g6,g5)
    c: Symmetric(g2,g2,g4)
    c: PointOnObject(g7,g-2)
    c: PointOnObject(g7,g0)
    c: DistanceY(g7,g2) = 170
    c: Radius(g6) = 5
    c: DistanceX(g2,g2) = 50
    c: Vertical(g8)
    c: Vertical(g9)
    c: Vertical(g10)
    c: Equal(g1,g3)
    c: Tangent(g0,g11) = -1.5708
    c: Tangent(g9,g11) = 1.5708
    c: Tangent(g0,g12) = -1.5708
    c: Equal(g11,g12)
    c: Radius(g11) = 2
    c: Tangent(g8,g13) = -1.5708
    c: Tangent(g3,g13) = 1.5708
    c: Tangent(g1,g14) = 1.5708
    c: Tangent(g10,g14) = 1.5708
    c: Equal(g13,g14)
    c: DistanceY(g9,g9) = 2
    c: DistanceY(g8,g8) = 15
    c: Radius(g13) = 2
    c: Diameter(g0) = 225
    c: PointOnObject(g15,g-1)
    c: PointOnObject(g16,g-1)
    c: Symmetric(g10,g17,g16)
    c: Symmetric(g8,g9,g15)
    c: Coincident(g17,g12)
    c: Vertical(g17)
    c: Equal(g10,g8)
    c: Equal(g9,g17)
    c: DistanceX(g12,g9) = 155
    c: Coincident(g18,g10)
    c: Vertical(g18)
    c: Coincident(g19,g18)
    c: Vertical(g19)
    c: Coincident(g20,g17)
    c: Vertical(g20)
    c: Equal(g20,g18)
    c: Coincident(g19,g20)
    c: Tangent(g12,g17)
    c: Coincident(g21,g8)
    c: Vertical(g21)
    c: Coincident(g22,g21)
    c: Vertical(g22)
    c: Coincident(g23,g22)
    c: Coincident(g23,g9)
    c: Equal(g23,g21)
    c: Vertical(g23)
    c: DistanceY(g21,g8) = 2
    c: Equal(g18,g21)
    c: DistanceY(g22,g21) = 48
    c: Horizontal(g24)
    c: Horizontal(g25)
    c: Horizontal(g26)
    c: PointOnObject(g27,g4)
    c: PointOnObject(g28,g4)
    c: PointOnObject(g29,g-2)
    c: Vertical(g30)
    c: Symmetric(g25,g25,g29)
    c: Symmetric(g24,g24,g28)
    c: Symmetric(g26,g26,g27)
    c: DistanceX(g25,g9) = 5
    c: Coincident(g31,g25)
    c: Coincident(g31,g9)
    c: Horizontal(g31)
    c: DistanceY(g21,g24) = 5
    c: Coincident(g30,g24)
    c: Coincident(g30,g25)
    c: DistanceY(g26,g2) = 20
    c: Coincident(g32,g26)
    c: PointOnObject(g32,g3)
    c: Horizontal(g32)
    c: DistanceX(g26,g32) = 6
    c: Coincident(g33,g26)
    c: Coincident(g34,g26)
    c: Coincident(g35,g24)
    c: Coincident(g36,g25)
    c: Coincident(g37,g25)
    c: Coincident(g38,g24)
    c: Equal(g37,g36)
    c: Equal(g36,g35)
    c: Equal(g35,g38)
    c: Equal(g35,g33)
    c: Equal(g33,g34)
    c: Diameter(g36) = 2.8
FEATURE [PartDesign::Plane] DatumPlane005  label="Datum_FootCSunk_Z"
  AttachmentOffset = pos=(0,0,2) rot=(0,0,1;0rad)
  Length = 187.44
  MapMode = 5
  Placement = pos=(0,0,2) rot=(0,0,1;0rad)
  ResizeMode = 0
  Support = -> [XY_Plane002]
  Width = 202.177
  expr: .AttachmentOffset.Base.z = <<params>>.shell_foot_csunk_z
FEATURE [PartDesign::Plane] DatumPlane006  label="Datum_FootSlot_Z"
  AttachmentOffset = pos=(0,0,4) rot=(0,0,1;0rad)
  Length = 187.44
  MapMode = 5
  Placement = pos=(0,0,4) rot=(0,0,1;0rad)
  ResizeMode = 0
  Support = -> [XY_Plane002]
  Width = 202.177
  expr: .AttachmentOffset.Base.z = <<params>>.shell_foot_slot_z
FEATURE [PartDesign::Plane] DatumPlane007  label="Datum_TopBrackCSunk_Z"
  AttachmentOffset = pos=(0,0,37.5) rot=(0,0,1;0rad)
  Length = 187.44
  MapMode = 5
  Placement = pos=(0,0,37.5) rot=(0,0,1;0rad)
  ResizeMode = 0
  Support = -> [XY_Plane002]
  Width = 202.177
  expr: .AttachmentOffset.Base.z = <<params>>.shell_topbrack_csunk_z
FEATURE [PartDesign::Plane] DatumPlane008  label="Datum_TopBrackSlot_Z"
  AttachmentOffset = pos=(0,0,40) rot=(0,0,1;0rad)
  Length = 187.44
  MapMode = 5
  Placement = pos=(0,0,40) rot=(0,0,1;0rad)
  ResizeMode = 0
  Support = -> [XY_Plane002]
  Width = 202.177
  expr: .AttachmentOffset.Base.z = <<params>>.shell_topbrack_slot_z
FEATURE [Sketcher::SketchObject] Sketch017  label="Sketch_FootHoles_CSunk"
  FullyConstrained = true
  MapMode = 5
  Placement = pos=(0,0,2) rot=(0,0,1;0rad)
  Support = -> [DatumPlane005]
  expr: Constraints[79] = <<params>>.shelltobot_back_offset_y
  expr: Constraints[76] = <<params>>.shelltobot_frontmid_offset_xy
  expr: Constraints[72] = <<params>>.shelltobot_frontmid_offset_xy
  expr: Constraints[59] = <<params>>.std_rad
  expr: Constraints[41] = <<params>>.plate_width
  expr: Constraints[14] = <<params>>.tail_width
  expr: Constraints[83] = <<params>>.shelltobot_back_offset_x
  expr: Constraints[13] = <<params>>.tail_rad
  expr: Constraints[32] = <<params>>.front_diameter
  expr: Constraints[29] = <<params>>.front_vert_edge
  expr: Constraints[12] = <<params>>.plate_length
  expr: Constraints[31] = <<params>>.std_rad
  expr: Constraints[30] = <<params>>.back_vert_edge
  expr: Constraints[61] = <<params>>.wheel_well_clearance
  expr: Constraints[23] = <<params>>.std_rad
  expr: Constraints[203] = <<params>>.m25_nut_clear_flat
  sketch-geometry (75):
    g0: ArcOfCircle CenterX=0 CenterY=52.6846 CenterZ=0 NormalX=0 NormalY=0 NormalZ=1 AngleXU=0 Radius=112.5 StartAngle=3.96017 EndAngle=5.4646
    g1: LineSegment StartX=-77.1162 StartY=42.1781 StartZ=0 EndX=-29.0404 EndY=108.13 EndZ=0
    g2: LineSegment StartX=-25 StartY=110.185 StartZ=0 EndX=25 EndY=110.185 EndZ=0
    g3: LineSegment StartX=29.0404 StartY=108.13 StartZ=0 EndX=77.1162 EndY=42.1781 EndZ=0
    g4: LineSegment StartX=0 StartY=0 StartZ=0 EndX=0 EndY=110.185 EndZ=0
    g5: ArcOfCircle CenterX=-25 CenterY=105.185 CenterZ=0 NormalX=0 NormalY=0 NormalZ=1 AngleXU=0 Radius=5 StartAngle=1.5708 EndAngle=2.5117
    g6: ArcOfCircle CenterX=25 CenterY=105.185 CenterZ=0 NormalX=0 NormalY=0 NormalZ=1 AngleXU=0 Radius=5 StartAngle=0.629894 EndAngle=1.5708
    g7: GeomPoint X=0 Y=-59.8154 Z=0
    g8: LineSegment StartX=77.5 StartY=26 StartZ=0 EndX=77.5 EndY=41 EndZ=0
    g9: LineSegment StartX=77.5 StartY=-26 StartZ=0 EndX=77.5 EndY=-28 EndZ=0
    g10: LineSegment StartX=-77.5 StartY=26 StartZ=0 EndX=-77.5 EndY=41 EndZ=0
    g11: ArcOfCircle CenterX=75.5 CenterY=-28 CenterZ=0 NormalX=0 NormalY=0 NormalZ=1 AngleXU=0 Radius=2 StartAngle=5.4646 EndAngle=6.28319
    g12: ArcOfCircle CenterX=-75.5 CenterY=-28 CenterZ=0 NormalX=0 NormalY=0 NormalZ=1 AngleXU=0 Radius=2 StartAngle=3.14159 EndAngle=3.96017
    g13: ArcOfCircle CenterX=75.5 CenterY=41 CenterZ=0 NormalX=0 NormalY=0 NormalZ=1 AngleXU=0 Radius=2 StartAngle=8e-16 EndAngle=0.629894
    g14: ArcOfCircle CenterX=-75.5 CenterY=41 CenterZ=0 NormalX=0 NormalY=0 NormalZ=1 AngleXU=0 Radius=2 StartAngle=2.5117 EndAngle=3.14159
    g15: GeomPoint X=77.5 Y=0 Z=0
    g16: GeomPoint X=-77.5 Y=0 Z=0
    g17: LineSegment StartX=-77.5 StartY=-28 StartZ=0 EndX=-77.5 EndY=-26 EndZ=0
    g18: LineSegment StartX=-77.5 StartY=26 StartZ=0 EndX=-77.5 EndY=24 EndZ=0
    g19: LineSegment StartX=-77.5 StartY=24 StartZ=0 EndX=-77.5 EndY=-24 EndZ=0
    g20: LineSegment StartX=-77.5 StartY=-26 StartZ=0 EndX=-77.5 EndY=-24 EndZ=0
    g21: LineSegment StartX=77.5 StartY=26 StartZ=0 EndX=77.5 EndY=24 EndZ=0
    g22: LineSegment StartX=77.5 StartY=24 StartZ=0 EndX=77.5 EndY=-24 EndZ=0
    g23: LineSegment StartX=77.5 StartY=-24 StartZ=0 EndX=77.5 EndY=-26 EndZ=0
    g24: LineSegment StartX=-72.5 StartY=29 StartZ=0 EndX=72.5 EndY=29 EndZ=0
    g25: LineSegment StartX=-72.5 StartY=-28 StartZ=0 EndX=72.5 EndY=-28 EndZ=0
    g26: LineSegment StartX=-36.1217 StartY=90.1846 StartZ=0 EndX=36.1217 EndY=90.1846 EndZ=0
    g27: GeomPoint X=0 Y=90.1846 Z=0
    g28: GeomPoint X=0 Y=29 Z=0
    g29: GeomPoint X=0 Y=-28 Z=0
    g30: LineSegment StartX=72.5 StartY=-28 StartZ=0 EndX=72.5 EndY=29 EndZ=0
    g31: LineSegment StartX=72.5 StartY=-28 StartZ=0 EndX=77.5 EndY=-28 EndZ=0
    g32: LineSegment StartX=36.1217 StartY=90.1846 StartZ=0 EndX=42.1217 EndY=90.1846 EndZ=0
    g33: LineSegment StartX=75.5022 StartY=-28 StartZ=0 EndX=74.0011 EndY=-25.4 EndZ=0
    g34: LineSegment StartX=74.0011 StartY=-25.4 StartZ=0 EndX=70.9989 EndY=-25.4 EndZ=0
    g35: LineSegment StartX=70.9989 StartY=-25.4 StartZ=0 EndX=69.4978 EndY=-28 EndZ=0
    g36: LineSegment StartX=69.4978 StartY=-28 StartZ=0 EndX=70.9989 EndY=-30.6 EndZ=0
    g37: LineSegment StartX=70.9989 StartY=-30.6 StartZ=0 EndX=74.0011 EndY=-30.6 EndZ=0
    g38: LineSegment StartX=74.0011 StartY=-30.6 StartZ=0 EndX=75.5022 EndY=-28 EndZ=0
    g39: Circle CenterX=72.5 CenterY=-28 CenterZ=0 NormalX=0 NormalY=0 NormalZ=1 AngleXU=0 Radius=3.00222
    g40: LineSegment StartX=69.4978 StartY=29 StartZ=0 EndX=70.9989 EndY=26.4 EndZ=0
    g41: LineSegment StartX=70.9989 StartY=26.4 StartZ=0 EndX=74.0011 EndY=26.4 EndZ=0
    g42: LineSegment StartX=74.0011 StartY=26.4 StartZ=0 EndX=75.5022 EndY=29 EndZ=0
    g43: LineSegment StartX=75.5022 StartY=29 StartZ=0 EndX=74.0011 EndY=31.6 EndZ=0
    g44: LineSegment StartX=74.0011 StartY=31.6 StartZ=0 EndX=70.9989 EndY=31.6 EndZ=0
    g45: LineSegment StartX=70.9989 StartY=31.6 StartZ=0 EndX=69.4978 EndY=29 EndZ=0
    g46: Circle CenterX=72.5 CenterY=29 CenterZ=0 NormalX=0 NormalY=0 NormalZ=1 AngleXU=0 Radius=3.00222
    g47: LineSegment StartX=33.1195 StartY=90.1846 StartZ=0 EndX=34.6206 EndY=87.5846 EndZ=0
    g48: LineSegment StartX=34.6206 StartY=87.5846 StartZ=0 EndX=37.6228 EndY=87.5846 EndZ=0
    g49: LineSegment StartX=37.6228 StartY=87.5846 StartZ=0 EndX=39.1239 EndY=90.1846 EndZ=0
    g50: LineSegment StartX=39.1239 StartY=90.1846 StartZ=0 EndX=37.6228 EndY=92.7846 EndZ=0
    g51: LineSegment StartX=37.6228 StartY=92.7846 StartZ=0 EndX=34.6206 EndY=92.7846 EndZ=0
    g52: LineSegment StartX=34.6206 StartY=92.7846 StartZ=0 EndX=33.1195 EndY=90.1846 EndZ=0
    g53: Circle CenterX=36.1217 CenterY=90.1846 CenterZ=0 NormalX=0 NormalY=0 NormalZ=1 AngleXU=0 Radius=3.00222
    g54: LineSegment StartX=-33.1195 StartY=90.1846 StartZ=0 EndX=-34.6206 EndY=92.7846 EndZ=0
    g55: LineSegment StartX=-34.6206 StartY=92.7846 StartZ=0 EndX=-37.6228 EndY=92.7846 EndZ=0
    g56: LineSegment StartX=-37.6228 StartY=92.7846 StartZ=0 EndX=-39.1239 EndY=90.1846 EndZ=0
    g57: LineSegment StartX=-39.1239 StartY=90.1846 StartZ=0 EndX=-37.6228 EndY=87.5846 EndZ=0
    g58: LineSegment StartX=-37.6228 StartY=87.5846 StartZ=0 EndX=-34.6206 EndY=87.5846 EndZ=0
    g59: LineSegment StartX=-34.6206 StartY=87.5846 StartZ=0 EndX=-33.1195 EndY=90.1846 EndZ=0
    g60: Circle CenterX=-36.1217 CenterY=90.1846 CenterZ=0 NormalX=0 NormalY=0 NormalZ=1 AngleXU=0 Radius=3.00222
    g61: LineSegment StartX=-69.4978 StartY=29 StartZ=0 EndX=-70.9989 EndY=31.6 EndZ=0
    g62: LineSegment StartX=-70.9989 StartY=31.6 StartZ=0 EndX=-74.0011 EndY=31.6 EndZ=0
    g63: LineSegment StartX=-74.0011 StartY=31.6 StartZ=0 EndX=-75.5022 EndY=29 EndZ=0
    g64: LineSegment StartX=-75.5022 StartY=29 StartZ=0 EndX=-74.0011 EndY=26.4 EndZ=0
    g65: LineSegment StartX=-74.0011 StartY=26.4 StartZ=0 EndX=-70.9989 EndY=26.4 EndZ=0
    g66: LineSegment StartX=-70.9989 StartY=26.4 StartZ=0 EndX=-69.4978 EndY=29 EndZ=0
    g67: Circle CenterX=-72.5 CenterY=29 CenterZ=0 NormalX=0 NormalY=0 NormalZ=1 AngleXU=0 Radius=3.00222
    g68: LineSegment StartX=-69.4978 StartY=-28 StartZ=0 EndX=-70.9989 EndY=-25.4 EndZ=0
    g69: LineSegment StartX=-70.9989 StartY=-25.4 StartZ=0 EndX=-74.0011 EndY=-25.4 EndZ=0
    g70: LineSegment StartX=-74.0011 StartY=-25.4 StartZ=0 EndX=-75.5022 EndY=-28 EndZ=0
    g71: LineSegment StartX=-75.5022 StartY=-28 StartZ=0 EndX=-74.0011 EndY=-30.6 EndZ=0
    g72: LineSegment StartX=-74.0011 StartY=-30.6 StartZ=0 EndX=-70.9989 EndY=-30.6 EndZ=0
    g73: LineSegment StartX=-70.9989 StartY=-30.6 StartZ=0 EndX=-69.4978 EndY=-28 EndZ=0
    g74: Circle CenterX=-72.5 CenterY=-28 CenterZ=0 NormalX=0 NormalY=0 NormalZ=1 AngleXU=0 Radius=3.00222
  constraints (180):
    c: PointOnObject(g0,g-2)
    c: Horizontal(g2)
    c: Coincident(g4,g-1)
    c: PointOnObject(g4,g-2)
    c: Tangent(g1,g5) = 1.5708
    c: Tangent(g2,g5) = 1.5708
    c: Tangent(g2,g6) = 1.5708
    c: Tangent(g3,g6) = 1.5708
    c: Equal(g6,g5)
    c: Symmetric(g2,g2,g4)
    c: PointOnObject(g7,g-2)
    c: PointOnObject(g7,g0)
    c: DistanceY(g7,g2) = 170
    c: Radius(g6) = 5
    c: DistanceX(g2,g2) = 50
    c: Vertical(g8)
    c: Vertical(g9)
    c: Vertical(g10)
    c: Equal(g1,g3)
    c: Tangent(g0,g11) = -1.5708
    c: Tangent(g9,g11) = 1.5708
    c: Tangent(g0,g12) = -1.5708
    c: Equal(g11,g12)
    c: Radius(g11) = 2
    c: Tangent(g8,g13) = -1.5708
    c: Tangent(g3,g13) = 1.5708
    c: Tangent(g1,g14) = 1.5708
    c: Tangent(g10,g14) = 1.5708
    c: Equal(g13,g14)
    c: DistanceY(g9,g9) = 2
    c: DistanceY(g8,g8) = 15
    c: Radius(g13) = 2
    c: Diameter(g0) = 225
    c: PointOnObject(g15,g-1)
    c: PointOnObject(g16,g-1)
    c: Symmetric(g10,g17,g16)
    c: Symmetric(g8,g9,g15)
    c: Coincident(g17,g12)
    c: Vertical(g17)
    c: Equal(g10,g8)
    c: Equal(g9,g17)
    c: DistanceX(g12,g9) = 155
    c: Coincident(g18,g10)
    c: Vertical(g18)
    c: Coincident(g19,g18)
    c: Vertical(g19)
    c: Coincident(g20,g17)
    c: Vertical(g20)
    c: Equal(g20,g18)
    c: Coincident(g19,g20)
    c: Tangent(g12,g17)
    c: Coincident(g21,g8)
    c: Vertical(g21)
    c: Coincident(g22,g21)
    c: Vertical(g22)
    c: Coincident(g23,g22)
    c: Coincident(g23,g9)
    c: Equal(g23,g21)
    c: Vertical(g23)
    c: DistanceY(g21,g8) = 2
    c: Equal(g18,g21)
    c: DistanceY(g22,g21) = 48
    c: Horizontal(g24)
    c: Horizontal(g25)
    c: Horizontal(g26)
    c: PointOnObject(g27,g4)
    c: PointOnObject(g28,g4)
    c: PointOnObject(g29,g-2)
    c: Vertical(g30)
    c: Symmetric(g25,g25,g29)
    c: Symmetric(g24,g24,g28)
    c: Symmetric(g26,g26,g27)
    c: DistanceX(g25,g9) = 5
    c: Coincident(g31,g25)
    c: Coincident(g31,g9)
    c: Horizontal(g31)
    c: DistanceY(g21,g24) = 5
    c: Coincident(g30,g24)
    c: Coincident(g30,g25)
    c: DistanceY(g26,g2) = 20
    c: Coincident(g32,g26)
    c: PointOnObject(g32,g3)
    c: Horizontal(g32)
    c: DistanceX(g26,g32) = 6
    c: Coincident(g33,g34)
    c: Coincident(g34,g35)
    c: Coincident(g35,g36)
    c: Coincident(g36,g37)
    c: Coincident(g37,g38)
    c: Coincident(g38,g33)
    c: Equal(g33, g34-g38) x5
    c: PointOnObject(g33,g39)
    c: PointOnObject(g34,g39)
    c: PointOnObject(g35,g39)
    c: PointOnObject(g36,g39)
    c: PointOnObject(g37,g39)
    c: PointOnObject(g38,g39)
    c: Coincident(g39,g25)
    c: PointOnObject(g38,g31)
    c: Coincident(g40,g41)
    c: Coincident(g41,g42)
    c: Coincident(g42,g43)
    c: Coincident(g43,g44)
    c: Coincident(g44,g45)
    c: Coincident(g45,g40)
    c: Equal(g40, g41-g45) x5
    c: PointOnObject(g40,g46)
    c: PointOnObject(g41,g46)
    c: PointOnObject(g42,g46)
    c: PointOnObject(g43,g46)
    c: PointOnObject(g44,g46)
    c: PointOnObject(g45,g46)
    c: Coincident(g46,g24)
    c: PointOnObject(g45,g24)
    c: Coincident(g47,g48)
    c: Coincident(g48,g49)
    c: Coincident(g49,g50)
    c: Coincident(g50,g51)
    c: Coincident(g51,g52)
    c: Coincident(g52,g47)
    c: Equal(g47, g48-g52) x5
    c: PointOnObject(g47,g53)
    c: PointOnObject(g48,g53)
    c: PointOnObject(g49,g53)
    c: PointOnObject(g50,g53)
    c: PointOnObject(g51,g53)
    c: PointOnObject(g52,g53)
    c: Coincident(g53,g26)
    c: PointOnObject(g52,g26)
    c: Coincident(g54,g55)
    c: Coincident(g55,g56)
    c: Coincident(g56,g57)
    c: Coincident(g57,g58)
    c: Coincident(g58,g59)
    c: Coincident(g59,g54)
    c: Equal(g54, g55-g59) x5
    c: PointOnObject(g54,g60)
    c: PointOnObject(g55,g60)
    c: PointOnObject(g56,g60)
    c: PointOnObject(g57,g60)
    c: PointOnObject(g58,g60)
    c: PointOnObject(g59,g60)
    c: Coincident(g60,g26)
    c: PointOnObject(g59,g26)
    c: Coincident(g61,g62)
    c: Coincident(g62,g63)
    c: Coincident(g63,g64)
    c: Coincident(g64,g65)
    c: Coincident(g65,g66)
    c: Coincident(g66,g61)
    c: Equal(g61, g62-g66) x5
    c: PointOnObject(g61,g67)
    c: PointOnObject(g62,g67)
    c: PointOnObject(g63,g67)
    c: PointOnObject(g64,g67)
    c: PointOnObject(g65,g67)
    c: PointOnObject(g66,g67)
    c: Coincident(g67,g24)
    c: PointOnObject(g66,g24)
    c: Coincident(g68,g69)
    c: Coincident(g69,g70)
    c: Coincident(g70,g71)
    c: Coincident(g71,g72)
    c: Coincident(g72,g73)
    c: Coincident(g73,g68)
    c: Equal(g68, g69-g73) x5
    c: PointOnObject(g68,g74)
    c: PointOnObject(g69,g74)
    c: PointOnObject(g70,g74)
    c: PointOnObject(g71,g74)
    c: PointOnObject(g72,g74)
    c: PointOnObject(g73,g74)
    c: Coincident(g74,g25)
    c: PointOnObject(g73,g25)
    c: Equal(g74,g39)
    c: Equal(g39,g46)
    c: Equal(g67,g46)
    c: Equal(g46,g53)
    c: Equal(g53,g60)
    c: DistanceY(g37,g33) = 5.2
FEATURE [Sketcher::SketchObject] Sketch018  label="Sketch_FootSlot"
  FullyConstrained = true
  MapMode = 5
  Placement = pos=(0,0,4) rot=(0,0,1;0rad)
  Support = -> [DatumPlane006]
  expr: Constraints[83] = <<params>>.shelltobot_back_offset_x
  expr: Constraints[13] = <<params>>.tail_rad
  expr: Constraints[32] = <<params>>.front_diameter
  expr: Constraints[29] = <<params>>.front_vert_edge
  expr: Constraints[31] = <<params>>.std_rad
  expr: Constraints[30] = <<params>>.back_vert_edge
  expr: Constraints[72] = <<params>>.shelltobot_frontmid_offset_xy
  expr: Constraints[76] = <<params>>.shelltobot_frontmid_offset_xy
  expr: Constraints[41] = <<params>>.plate_width
  expr: Constraints[14] = <<params>>.tail_width
  expr: Constraints[12] = <<params>>.plate_length
  expr: Constraints[59] = <<params>>.std_rad
  expr: Constraints[79] = <<params>>.shelltobot_back_offset_y
  expr: Constraints[176] = <<params>>.m25_nut_clear_flat
  expr: Constraints[61] = <<params>>.wheel_well_clearance
  expr: Constraints[23] = <<params>>.std_rad
  sketch-geometry (81):
    g0: ArcOfCircle CenterX=0 CenterY=52.6846 CenterZ=0 NormalX=0 NormalY=0 NormalZ=1 AngleXU=0 Radius=112.5 StartAngle=3.96017 EndAngle=5.4646
    g1: LineSegment StartX=-77.1162 StartY=42.1781 StartZ=0 EndX=-29.0404 EndY=108.13 EndZ=0
    g2: LineSegment StartX=-25 StartY=110.185 StartZ=0 EndX=25 EndY=110.185 EndZ=0
    g3: LineSegment StartX=29.0404 StartY=108.13 StartZ=0 EndX=77.1162 EndY=42.1781 EndZ=0
    g4: LineSegment StartX=0 StartY=0 StartZ=0 EndX=0 EndY=110.185 EndZ=0
    g5: ArcOfCircle CenterX=-25 CenterY=105.185 CenterZ=0 NormalX=0 NormalY=0 NormalZ=1 AngleXU=0 Radius=5 StartAngle=1.5708 EndAngle=2.5117
    g6: ArcOfCircle CenterX=25 CenterY=105.185 CenterZ=0 NormalX=0 NormalY=0 NormalZ=1 AngleXU=0 Radius=5 StartAngle=0.629894 EndAngle=1.5708
    g7: GeomPoint X=0 Y=-59.8154 Z=0
    g8: LineSegment StartX=77.5 StartY=26 StartZ=0 EndX=77.5 EndY=41 EndZ=0
    g9: LineSegment StartX=77.5 StartY=-26 StartZ=0 EndX=77.5 EndY=-28 EndZ=0
    g10: LineSegment StartX=-77.5 StartY=26 StartZ=0 EndX=-77.5 EndY=41 EndZ=0
    g11: ArcOfCircle CenterX=75.5 CenterY=-28 CenterZ=0 NormalX=0 NormalY=0 NormalZ=1 AngleXU=0 Radius=2 StartAngle=5.4646 EndAngle=6.28319
    g12: ArcOfCircle CenterX=-75.5 CenterY=-28 CenterZ=0 NormalX=0 NormalY=0 NormalZ=1 AngleXU=0 Radius=2 StartAngle=3.14159 EndAngle=3.96017
    g13: ArcOfCircle CenterX=75.5 CenterY=41 CenterZ=0 NormalX=0 NormalY=0 NormalZ=1 AngleXU=0 Radius=2 StartAngle=1.7e-15 EndAngle=0.629894
    g14: ArcOfCircle CenterX=-75.5 CenterY=41 CenterZ=0 NormalX=0 NormalY=0 NormalZ=1 AngleXU=0 Radius=2 StartAngle=2.5117 EndAngle=3.14159
    g15: GeomPoint X=77.5 Y=0 Z=0
    g16: GeomPoint X=-77.5 Y=0 Z=0
    g17: LineSegment StartX=-77.5 StartY=-28 StartZ=0 EndX=-77.5 EndY=-26 EndZ=0
    g18: LineSegment StartX=-77.5 StartY=26 StartZ=0 EndX=-77.5 EndY=24 EndZ=0
    g19: LineSegment StartX=-77.5 StartY=24 StartZ=0 EndX=-77.5 EndY=-24 EndZ=0
    g20: LineSegment StartX=-77.5 StartY=-26 StartZ=0 EndX=-77.5 EndY=-24 EndZ=0
    g21: LineSegment StartX=77.5 StartY=26 StartZ=0 EndX=77.5 EndY=24 EndZ=0
    g22: LineSegment StartX=77.5 StartY=24 StartZ=0 EndX=77.5 EndY=-24 EndZ=0
    g23: LineSegment StartX=77.5 StartY=-24 StartZ=0 EndX=77.5 EndY=-26 EndZ=0
    g24: LineSegment StartX=-72.5 StartY=29 StartZ=0 EndX=72.5 EndY=29 EndZ=0
    g25: LineSegment StartX=-72.5 StartY=-28 StartZ=0 EndX=72.5 EndY=-28 EndZ=0
    g26: LineSegment StartX=-36.1217 StartY=90.1846 StartZ=0 EndX=36.1217 EndY=90.1846 EndZ=0
    g27: GeomPoint X=0 Y=90.1846 Z=0
    g28: GeomPoint X=0 Y=29 Z=0
    g29: GeomPoint X=0 Y=-28 Z=0
    g30: LineSegment StartX=72.5 StartY=-28 StartZ=0 EndX=72.5 EndY=29 EndZ=0
    g31: LineSegment StartX=72.5 StartY=-28 StartZ=0 EndX=77.5 EndY=-28 EndZ=0
    g32: LineSegment StartX=36.1217 StartY=90.1846 StartZ=0 EndX=42.1217 EndY=90.1846 EndZ=0
    g33: LineSegment StartX=75.5022 StartY=-28 StartZ=0 EndX=74.0011 EndY=-25.4 EndZ=0
    g34: LineSegment StartX=74.0011 StartY=-25.4 StartZ=0 EndX=70.9989 EndY=-25.4 EndZ=0
    g35: LineSegment StartX=70.9989 StartY=-30.6 StartZ=0 EndX=74.0011 EndY=-30.6 EndZ=0
    g36: LineSegment StartX=74.0011 StartY=-30.6 StartZ=0 EndX=75.5022 EndY=-28 EndZ=0
    g37: Circle CenterX=72.5 CenterY=-28 CenterZ=0 NormalX=0 NormalY=0 NormalZ=1 AngleXU=0 Radius=3.00222
    g38: LineSegment StartX=75.5022 StartY=29 StartZ=0 EndX=74.0011 EndY=31.6 EndZ=0
    g39: LineSegment StartX=74.0011 StartY=31.6 StartZ=0 EndX=70.9989 EndY=31.6 EndZ=0
    g40: LineSegment StartX=70.9989 StartY=26.4 StartZ=0 EndX=74.0011 EndY=26.4 EndZ=0
    g41: LineSegment StartX=74.0011 StartY=26.4 StartZ=0 EndX=75.5022 EndY=29 EndZ=0
    g42: Circle CenterX=72.5 CenterY=29 CenterZ=0 NormalX=0 NormalY=0 NormalZ=1 AngleXU=0 Radius=3.00222
    g43: LineSegment StartX=39.1239 StartY=90.1846 StartZ=0 EndX=37.6228 EndY=92.7846 EndZ=0
    g44: LineSegment StartX=37.6228 StartY=92.7846 StartZ=0 EndX=34.6206 EndY=92.7846 EndZ=0
    g45: LineSegment StartX=34.6206 StartY=87.5846 StartZ=0 EndX=37.6228 EndY=87.5846 EndZ=0
    g46: LineSegment StartX=37.6228 StartY=87.5846 StartZ=0 EndX=39.1239 EndY=90.1846 EndZ=0
    g47: Circle CenterX=36.1217 CenterY=90.1846 CenterZ=0 NormalX=0 NormalY=0 NormalZ=1 AngleXU=0 Radius=3.00222
    g48: LineSegment StartX=-39.1239 StartY=90.1846 StartZ=0 EndX=-37.6228 EndY=87.5846 EndZ=0
    g49: LineSegment StartX=-37.6228 StartY=87.5846 StartZ=0 EndX=-34.6206 EndY=87.5846 EndZ=0
    g50: LineSegment StartX=-34.6206 StartY=92.7846 StartZ=0 EndX=-37.6228 EndY=92.7846 EndZ=0
    g51: LineSegment StartX=-37.6228 StartY=92.7846 StartZ=0 EndX=-39.1239 EndY=90.1846 EndZ=0
    g52: Circle CenterX=-36.1217 CenterY=90.1846 CenterZ=0 NormalX=0 NormalY=0 NormalZ=1 AngleXU=0 Radius=3.00222
    g53: LineSegment StartX=-75.5022 StartY=29 StartZ=0 EndX=-74.0011 EndY=26.4 EndZ=0
    g54: LineSegment StartX=-74.0011 StartY=26.4 StartZ=0 EndX=-70.9989 EndY=26.4 EndZ=0
    g55: LineSegment StartX=-70.9989 StartY=31.6 StartZ=0 EndX=-74.0011 EndY=31.6 EndZ=0
    g56: LineSegment StartX=-74.0011 StartY=31.6 StartZ=0 EndX=-75.5022 EndY=29 EndZ=0
    g57: Circle CenterX=-72.5 CenterY=29 CenterZ=0 NormalX=0 NormalY=0 NormalZ=1 AngleXU=0 Radius=3.00222
    g58: LineSegment StartX=-75.5022 StartY=-28 StartZ=0 EndX=-74.0011 EndY=-30.6 EndZ=0
    g59: LineSegment StartX=-74.0011 StartY=-30.6 StartZ=0 EndX=-70.9989 EndY=-30.6 EndZ=0
    g60: LineSegment StartX=-70.9989 StartY=-25.4 StartZ=0 EndX=-74.0011 EndY=-25.4 EndZ=0
    g61: LineSegment StartX=-74.0011 StartY=-25.4 StartZ=0 EndX=-75.5022 EndY=-28 EndZ=0
    g62: Circle CenterX=-72.5 CenterY=-28 CenterZ=0 NormalX=0 NormalY=0 NormalZ=1 AngleXU=0 Radius=3.00222
    g63: LineSegment StartX=-70.9989 StartY=-30.6 StartZ=0 EndX=-50.9989 EndY=-30.6 EndZ=0
    g64: LineSegment StartX=-70.9989 StartY=-25.4 StartZ=0 EndX=-50.9989 EndY=-25.4 EndZ=0
    g65: LineSegment StartX=-50.9989 StartY=-25.4 StartZ=0 EndX=-50.9989 EndY=-30.6 EndZ=0
    g66: LineSegment StartX=70.9989 StartY=-25.4 StartZ=0 EndX=50.9989 EndY=-25.4 EndZ=0
    g67: LineSegment StartX=70.9989 StartY=-30.6 StartZ=0 EndX=50.9989 EndY=-30.6 EndZ=0
    g68: LineSegment StartX=50.9989 StartY=-30.6 StartZ=0 EndX=50.9989 EndY=-25.4 EndZ=0
    g69: LineSegment StartX=70.9989 StartY=26.4 StartZ=0 EndX=50.9989 EndY=26.4 EndZ=0
    g70: LineSegment StartX=70.9989 StartY=31.6 StartZ=0 EndX=50.9989 EndY=31.6 EndZ=0
    g71: LineSegment StartX=50.9989 StartY=26.4 StartZ=0 EndX=50.9989 EndY=31.6 EndZ=0
    g72: LineSegment StartX=34.6206 StartY=87.5846 StartZ=0 EndX=14.6206 EndY=87.5846 EndZ=0
    g73: LineSegment StartX=34.6206 StartY=92.7846 StartZ=0 EndX=14.6206 EndY=92.7846 EndZ=0
    g74: LineSegment StartX=14.6206 StartY=87.5846 StartZ=0 EndX=14.6206 EndY=92.7846 EndZ=0
    g75: LineSegment StartX=-34.6206 StartY=92.7846 StartZ=0 EndX=-14.6206 EndY=92.7846 EndZ=0
    g76: LineSegment StartX=-34.6206 StartY=87.5846 StartZ=0 EndX=-14.6206 EndY=87.5846 EndZ=0
    g77: LineSegment StartX=-14.6206 StartY=87.5846 StartZ=0 EndX=-14.6206 EndY=92.7846 EndZ=0
    g78: LineSegment StartX=-70.9989 StartY=26.4 StartZ=0 EndX=-50.9989 EndY=26.4 EndZ=0
    g79: LineSegment StartX=-70.9989 StartY=31.6 StartZ=0 EndX=-50.9989 EndY=31.6 EndZ=0
    g80: LineSegment StartX=-50.9989 StartY=31.6 StartZ=0 EndX=-50.9989 EndY=26.4 EndZ=0
  constraints (222):
    c: PointOnObject(g0,g-2)
    c: Horizontal(g2)
    c: Coincident(g4,g-1)
    c: PointOnObject(g4,g-2)
    c: Tangent(g1,g5) = 1.5708
    c: Tangent(g2,g5) = 1.5708
    c: Tangent(g2,g6) = 1.5708
    c: Tangent(g3,g6) = 1.5708
    c: Equal(g6,g5)
    c: Symmetric(g2,g2,g4)
    c: PointOnObject(g7,g-2)
    c: PointOnObject(g7,g0)
    c: DistanceY(g7,g2) = 170
    c: Radius(g6) = 5
    c: DistanceX(g2,g2) = 50
    c: Vertical(g8)
    c: Vertical(g9)
    c: Vertical(g10)
    c: Equal(g1,g3)
    c: Tangent(g0,g11) = -1.5708
    c: Tangent(g9,g11) = 1.5708
    c: Tangent(g0,g12) = -1.5708
    c: Equal(g11,g12)
    c: Radius(g11) = 2
    c: Tangent(g8,g13) = -1.5708
    c: Tangent(g3,g13) = 1.5708
    c: Tangent(g1,g14) = 1.5708
    c: Tangent(g10,g14) = 1.5708
    c: Equal(g13,g14)
    c: DistanceY(g9,g9) = 2
    c: DistanceY(g8,g8) = 15
    c: Radius(g13) = 2
    c: Diameter(g0) = 225
    c: PointOnObject(g15,g-1)
    c: PointOnObject(g16,g-1)
    c: Symmetric(g10,g17,g16)
    c: Symmetric(g8,g9,g15)
    c: Coincident(g17,g12)
    c: Vertical(g17)
    c: Equal(g10,g8)
    c: Equal(g9,g17)
    c: DistanceX(g12,g9) = 155
    c: Coincident(g18,g10)
    c: Vertical(g18)
    c: Coincident(g19,g18)
    c: Vertical(g19)
    c: Coincident(g20,g17)
    c: Vertical(g20)
    c: Equal(g20,g18)
    c: Coincident(g19,g20)
    c: Tangent(g12,g17)
    c: Coincident(g21,g8)
    c: Vertical(g21)
    c: Coincident(g22,g21)
    c: Vertical(g22)
    c: Coincident(g23,g22)
    c: Coincident(g23,g9)
    c: Equal(g23,g21)
    c: Vertical(g23)
    c: DistanceY(g21,g8) = 2
    c: Equal(g18,g21)
    c: DistanceY(g22,g21) = 48
    c: Horizontal(g24)
    c: Horizontal(g25)
    c: Horizontal(g26)
    c: PointOnObject(g27,g4)
    c: PointOnObject(g28,g4)
    c: PointOnObject(g29,g-2)
    c: Vertical(g30)
    c: Symmetric(g25,g25,g29)
    c: Symmetric(g24,g24,g28)
    c: Symmetric(g26,g26,g27)
    c: DistanceX(g25,g9) = 5
    c: Coincident(g31,g25)
    c: Coincident(g31,g9)
    c: Horizontal(g31)
    c: DistanceY(g21,g24) = 5
    c: Coincident(g30,g24)
    c: Coincident(g30,g25)
    c: DistanceY(g26,g2) = 20
    c: Coincident(g32,g26)
    c: PointOnObject(g32,g3)
    c: Horizontal(g32)
    c: DistanceX(g26,g32) = 6
    c: Coincident(g33,g34)
    c: Coincident(g35,g36)
    c: Coincident(g36,g33)
    c: Equal(g33,g34)
    c: Equal(g33,g35)
    c: Equal(g33,g36)
    c: PointOnObject(g33,g37)
    c: PointOnObject(g34,g37)
    c: PointOnObject(g35,g37)
    c: PointOnObject(g35,g37)
    c: PointOnObject(g36,g37)
    c: Coincident(g37,g25)
    c: PointOnObject(g36,g31)
    c: Coincident(g38,g39)
    c: Coincident(g40,g41)
    c: Coincident(g41,g38)
    c: Equal(g38,g39)
    c: Equal(g38,g40)
    c: Equal(g38,g41)
    c: PointOnObject(g38,g42)
    c: PointOnObject(g39,g42)
    c: PointOnObject(g40,g42)
    c: PointOnObject(g40,g42)
    c: PointOnObject(g41,g42)
    c: Coincident(g42,g24)
    c: Coincident(g43,g44)
    c: Coincident(g45,g46)
    c: Coincident(g46,g43)
    c: Equal(g43,g44)
    c: Equal(g43,g45)
    c: Equal(g43,g46)
    c: PointOnObject(g43,g47)
    c: PointOnObject(g44,g47)
    c: PointOnObject(g45,g47)
    c: PointOnObject(g45,g47)
    c: PointOnObject(g46,g47)
    c: Coincident(g47,g26)
    c: PointOnObject(g46,g32)
    c: Coincident(g48,g49)
    c: Coincident(g50,g51)
    c: Coincident(g51,g48)
    c: Equal(g48,g49)
    c: Equal(g48,g50)
    c: Equal(g48,g51)
    c: PointOnObject(g48,g52)
    c: PointOnObject(g49,g52)
    c: PointOnObject(g50,g52)
    c: PointOnObject(g50,g52)
    c: PointOnObject(g51,g52)
    c: Coincident(g52,g26)
    c: Coincident(g53,g54)
    c: Coincident(g55,g56)
    c: Coincident(g56,g53)
    c: Equal(g53,g54)
    c: Equal(g53,g55)
    c: Equal(g53,g56)
    c: PointOnObject(g53,g57)
    c: PointOnObject(g54,g57)
    c: PointOnObject(g55,g57)
    c: PointOnObject(g55,g57)
    c: PointOnObject(g56,g57)
    c: Coincident(g57,g24)
    c: Coincident(g58,g59)
    c: Coincident(g60,g61)
    c: Coincident(g61,g58)
    c: Equal(g58,g59)
    c: Equal(g58,g60)
    c: Equal(g58,g61)
    c: PointOnObject(g58,g62)
    c: PointOnObject(g59,g62)
    c: PointOnObject(g60,g62)
    c: PointOnObject(g60,g62)
    c: PointOnObject(g61,g62)
    c: Coincident(g62,g25)
    c: Horizontal(g60)
    c: Horizontal(g59)
    c: Coincident(g63,g59)
    c: Horizontal(g63)
    c: Coincident(g64,g60)
    c: Horizontal(g64)
    c: Coincident(g65,g64)
    c: Coincident(g65,g63)
    c: Vertical(g65)
    c: Equal(g62,g37)
    c: Equal(g37,g42)
    c: Equal(g42,g57)
    c: Equal(g57,g52)
    c: Equal(g52,g47)
    c: Horizontal(g40)
    c: Horizontal(g49)
    c: Horizontal(g54)
    c: Distance(g63) = 20
    c: DistanceY(g35,g33) = 5.2
    c: Horizontal(g35)
    c: Coincident(g66,g34)
    c: Horizontal(g66)
    c: Coincident(g67,g35)
    c: Horizontal(g67)
    c: Coincident(g68,g67)
    c: Coincident(g68,g66)
    c: Vertical(g68)
    c: Equal(g64,g66)
    c: Horizontal(g39)
    c: Coincident(g69,g40)
    c: Horizontal(g69)
    c: Coincident(g70,g39)
    c: Horizontal(g70)
    c: Coincident(g71,g69)
    c: Coincident(g71,g70)
    c: Vertical(g71)
    c: Equal(g66,g69)
    c: Horizontal(g45)
    c: Coincident(g72,g45)
    c: Horizontal(g72)
    c: Coincident(g73,g44)
    c: Horizontal(g73)
    c: Coincident(g74,g72)
    c: Coincident(g74,g73)
    c: Vertical(g74)
    c: Equal(g70,g72)
    c: Horizontal(g55)
    c: Horizontal(g50)
    c: Coincident(g75,g50)
    c: Horizontal(g75)
    c: Coincident(g76,g49)
    c: Horizontal(g76)
    c: Coincident(g77,g76)
    c: Coincident(g77,g75)
    c: Vertical(g77)
    c: Coincident(g78,g54)
    c: Horizontal(g78)
    c: Coincident(g79,g55)
    c: Horizontal(g79)
    c: Coincident(g80,g79)
    c: Coincident(g80,g78)
    c: Vertical(g80)
    c: Equal(g72,g76)
    c: Equal(g70,g79)
FEATURE [Sketcher::SketchObject] Sketch
  FullyConstrained = true
  MapMode = 5
  Placement = pos=(0,0,0) rot=(1,0,0;1.5708rad)
  Support = -> [XZ_Plane002]
  sketch-geometry (18):
    g0: LineSegment StartX=-12 StartY=0 StartZ=0 EndX=12 EndY=0 EndZ=0
    g1: LineSegment StartX=-12 StartY=0 StartZ=0 EndX=-12 EndY=3 EndZ=0
    g2: LineSegment StartX=12 StartY=0 StartZ=0 EndX=12 EndY=3 EndZ=0
    g3: LineSegment StartX=-12 StartY=3 StartZ=0 EndX=-7.5 EndY=8.36289 EndZ=0
    g4: LineSegment StartX=12 StartY=3 StartZ=0 EndX=7.5 EndY=8.36289 EndZ=0
    g5: LineSegment StartX=-7.5 StartY=8.36289 StartZ=0 EndX=-7.5 EndY=10 EndZ=0
    g6: LineSegment StartX=7.5 StartY=8.36289 StartZ=0 EndX=7.5 EndY=10 EndZ=0
    g7: LineSegment StartX=9.5 StartY=12 StartZ=0 EndX=25.5 EndY=12 EndZ=0
    g8: LineSegment StartX=27.5 StartY=14 StartZ=0 EndX=27.5 EndY=50 EndZ=0
    g9: LineSegment StartX=-9.5 StartY=12 StartZ=0 EndX=-25.5 EndY=12 EndZ=0
    g10: LineSegment StartX=-27.5 StartY=14 StartZ=0 EndX=-27.5 EndY=50 EndZ=0
    g11: LineSegment StartX=-27.5 StartY=50 StartZ=0 EndX=27.5 EndY=50 EndZ=0
    g12: LineSegment StartX=-12 StartY=3 StartZ=0 EndX=12 EndY=3 EndZ=0
    g13: LineSegment StartX=-7.5 StartY=8.36289 StartZ=0 EndX=7.5 EndY=8.36289 EndZ=0
    g14: ArcOfCircle CenterX=-9.5 CenterY=10 CenterZ=0 NormalX=0 NormalY=0 NormalZ=1 AngleXU=0 Radius=2 StartAngle=0 EndAngle=1.5708
    g15: ArcOfCircle CenterX=9.5 CenterY=10 CenterZ=0 NormalX=0 NormalY=0 NormalZ=1 AngleXU=0 Radius=2 StartAngle=1.5708 EndAngle=3.14159
    g16: ArcOfCircle CenterX=25.5 CenterY=14 CenterZ=0 NormalX=0 NormalY=0 NormalZ=1 AngleXU=0 Radius=2 StartAngle=4.71239 EndAngle=6.28319
    g17: ArcOfCircle CenterX=-25.5 CenterY=14 CenterZ=0 NormalX=0 NormalY=0 NormalZ=1 AngleXU=0 Radius=2 StartAngle=3.14159 EndAngle=4.71239
  constraints (47):
    c: Horizontal(g0)
    c: Symmetric(g0,g0,g-1)
    c: Coincident(g1,g0)
    c: Vertical(g1)
    c: Coincident(g2,g0)
    c: Vertical(g2)
    c: Coincident(g3,g1)
    c: Coincident(g4,g2)
    c: Coincident(g5,g3)
    c: Vertical(g5)
    c: Coincident(g6,g4)
    c: Vertical(g6)
    c: Horizontal(g7)
    c: Vertical(g8)
    c: Horizontal(g9)
    c: Vertical(g10)
    c: Coincident(g11,g10)
    c: Coincident(g11,g8)
    c: Horizontal(g11)
    c: Coincident(g12,g1)
    c: Coincident(g12,g2)
    c: Coincident(g13,g3)
    c: Coincident(g13,g4)
    c: Horizontal(g13)
    c: Horizontal(g12)
    c: Tangent(g5,g14) = -1.5708
    c: Tangent(g9,g14) = -1.5708
    c: Tangent(g6,g15) = 1.5708
    c: Tangent(g7,g15) = 1.5708
    c: Tangent(g7,g16) = -1.5708
    c: Tangent(g8,g16) = -1.5708
    c: Tangent(g9,g17) = 1.5708
    c: Tangent(g10,g17) = 1.5708
    c: Equal(g15,g16)
    c: Equal(g15,g14)
    c: Equal(g14,g17)
    c: Equal(g5,g6)
    c: Equal(g7,g9)
    c: Angle(g4,g12) = 0.872665
    c: DistanceY(g0,g2) = 3
    c: Radius(g16) = 2
    c: DistanceX(g0,g0) = 24
    c: DistanceX(g3,g4) = 15
    c: Equal(g4,g3)
    c: DistanceY(g0,g7) = 12
    c: DistanceX(g10,g8) = 55
    c: DistanceY(g0,g8) = 50
FEATURE [PartDesign::Plane] DatumPlane009  label="Datum_LSRVis_L"
  AttachmentOffset = pos=(0,0,-52.68) rot=(0,1,0;0.549779rad)
  Length = 245.175
  MapMode = 5
  Placement = pos=(0,52.68,1.17e-14) rot=(0.928845,0.261961,0.261961;1.64454rad)
  ResizeMode = 0
  Support = -> [XZ_Plane002]
  Width = 91.3284
  expr: .AttachmentOffset.Base.z = <<params>>.LSRvis_offset * -1
  expr: .AttachmentOffset.Rotation.Pitch = <<params>>.LSRvis_angle
FEATURE [PartDesign::Plane] DatumPlane010  label="Datum_LSRVis_R"
  AttachmentOffset = pos=(0,0,-52.68) rot=(0,-1,0;0.549779rad)
  Length = 245.175
  MapMode = 5
  Placement = pos=(0,52.68,1.17e-14) rot=(0.928845,-0.261961,-0.261961;1.64454rad)
  ResizeMode = 0
  Support = -> [XZ_Plane002]
  Width = 91.3284
  expr: .AttachmentOffset.Base.z = -1 * <<params>>.LSRvis_offset
  expr: .AttachmentOffset.Rotation.Pitch = -1 * <<params>>.LSRvis_angle
FEATURE [Sketcher::SketchObject] Sketch019  label="Sketch_LSRVis_L"
  FullyConstrained = true
  MapMode = 5
  Placement = pos=(-3.6e-15,52.68,1.17e-14) rot=(0.928845,0.261961,0.261961;1.64454rad)
  Support = -> [DatumPlane009]
  expr: Constraints[2] = <<params>>.LSRvis_diam
  expr: Constraints[1] = <<params>>.LSRvis_hole_height
  sketch-geometry (1):
    g0: Circle CenterX=0 CenterY=11 CenterZ=0 NormalX=0 NormalY=0 NormalZ=1 AngleXU=0 Radius=5.5
  constraints (3):
    c: PointOnObject(g0,g-2)
    c: DistanceY(g-1,g0) = 11
    c: Diameter(g0) = 11
FEATURE [Sketcher::SketchObject] Sketch020  label="Sketch_LSRVis_R"
  FullyConstrained = true
  MapMode = 5
  Placement = pos=(3.6e-15,52.68,1.17e-14) rot=(0.928845,-0.261961,-0.261961;1.64454rad)
  Support = -> [DatumPlane010]
  expr: Constraints[1] = <<params>>.LSRvis_hole_height
  expr: Constraints[2] = <<params>>.LSRvis_diam
  sketch-geometry (1):
    g0: Circle CenterX=0 CenterY=11 CenterZ=0 NormalX=0 NormalY=0 NormalZ=1 AngleXU=0 Radius=5.5
  constraints (3):
    c: PointOnObject(g0,g-2)
    c: DistanceY(g-1,g0) = 11
    c: Diameter(g0) = 11
FEATURE [PartDesign::SubtractiveLoft] SubtractiveLoft001  label="Shell_TopBrackAng_SubLoft"
  BaseFeature = -> SubtractiveLoft
  Closed = false
  Profile = -> Sketch011
  Ruled = false
  Sections = -> [Sketch010]
FEATURE [PartDesign::SubtractiveLoft] SubtractiveLoft002  label="Shell_TopBrackStr_SubLoft"
  BaseFeature = -> SubtractiveLoft001
  Closed = false
  Profile = -> Sketch012
  Ruled = false
  Sections = -> [Sketch013]
FEATURE [PartDesign::Pocket] Pocket003  label="ShellToBot_MtHoles"
  BaseFeature = -> SubtractiveLoft002
  Length = 6.5
  Length2 = 100
  Profile = -> Sketch016
  Reversed = true
  Type = 0
  expr: Length = <<params>>.shell_foot_slot_z + <<params>>.shell_foot_slot_height
FEATURE [PartDesign::Pocket] Pocket004  label="Foot_HexSunk"
  BaseFeature = -> Pocket003
  Length = 2
  Length2 = 100
  Profile = -> Sketch017
  Reversed = true
  Type = 0
  expr: Length = <<params>>.shell_foot_csunk_height
FEATURE [PartDesign::Pocket] Pocket005  label="Foot_HexSlot"
  BaseFeature = -> Pocket004
  Length = 2.5
  Length2 = 100
  Profile = -> Sketch018
  Reversed = true
  Type = 0
  expr: Length = <<params>>.shell_foot_slot_height
FEATURE [PartDesign::Pocket] Pocket006  label="USRCut"
  BaseFeature = -> Pocket005
  Length = 5
  Length2 = 100
  Profile = -> Sketch
  Reversed = true
  Type = 1
FEATURE [Sketcher::SketchObject] Sketch021  label="Sketch_TopMountHoles"
  FullyConstrained = true
  MapMode = 5
  Placement = pos=(0,0,42) rot=(0,0,1;0rad)
  Support = -> [DatumPlane]
  expr: Constraints[91] = <<params>>.top_brack_front_leng - <<params>>.shell_topbrack_hole_offset
  expr: Constraints[90] = <<params>>.shell_topbrack_hole_offset
  expr: Constraints[61] = <<params>>.wheel_well_clearance
  expr: Constraints[23] = <<params>>.std_rad
  expr: Constraints[30] = <<params>>.back_vert_edge
  expr: Constraints[31] = <<params>>.std_rad
  expr: Constraints[12] = <<params>>.plate_length
  expr: Constraints[29] = <<params>>.front_vert_edge
  expr: Constraints[32] = <<params>>.front_diameter
  expr: Constraints[85] = <<params>>.shell_topbrack_hole_offset + <<params>>.std_rad
  expr: Constraints[13] = <<params>>.tail_rad
  expr: Constraints[83] = <<params>>.shell_overhang_leng + <<params>>.shell_topbrack_width - <<params>>.shell_topbrack_hole_offset
  expr: Constraints[14] = <<params>>.tail_width
  expr: Constraints[41] = <<params>>.plate_width
  expr: Constraints[59] = <<params>>.std_rad
  expr: Constraints[82] = <<params>>.shell_overhang_leng + <<params>>.shell_topbrack_width - <<params>>.shell_topbrack_hole_offset
  expr: Constraints[84] = <<params>>.m2_hole_clear_diam
  expr: Constraints[86] = <<params>>.shell_topbrack_width * 2 - <<params>>.std_rad - <<params>>.shell_topbrack_hole_offset
  sketch-geometry (37):
    g0: ArcOfCircle CenterX=0 CenterY=52.6846 CenterZ=0 NormalX=0 NormalY=0 NormalZ=1 AngleXU=0 Radius=112.5 StartAngle=3.96017 EndAngle=5.4646
    g1: LineSegment StartX=-77.1162 StartY=42.1781 StartZ=0 EndX=-29.0404 EndY=108.13 EndZ=0
    g2: LineSegment StartX=-25 StartY=110.185 StartZ=0 EndX=25 EndY=110.185 EndZ=0
    g3: LineSegment StartX=29.0404 StartY=108.13 StartZ=0 EndX=77.1162 EndY=42.1781 EndZ=0
    g4: LineSegment StartX=0 StartY=0 StartZ=0 EndX=0 EndY=110.185 EndZ=0
    g5: ArcOfCircle CenterX=-25 CenterY=105.185 CenterZ=0 NormalX=0 NormalY=0 NormalZ=1 AngleXU=0 Radius=5 StartAngle=1.5708 EndAngle=2.5117
    g6: ArcOfCircle CenterX=25 CenterY=105.185 CenterZ=0 NormalX=0 NormalY=0 NormalZ=1 AngleXU=0 Radius=5 StartAngle=0.629894 EndAngle=1.5708
    g7: GeomPoint X=0 Y=-59.8154 Z=0
    g8: LineSegment StartX=77.5 StartY=26 StartZ=0 EndX=77.5 EndY=41 EndZ=0
    g9: LineSegment StartX=77.5 StartY=-26 StartZ=0 EndX=77.5 EndY=-28 EndZ=0
    g10: LineSegment StartX=-77.5 StartY=26 StartZ=0 EndX=-77.5 EndY=41 EndZ=0
    g11: ArcOfCircle CenterX=75.5 CenterY=-28 CenterZ=0 NormalX=0 NormalY=0 NormalZ=1 AngleXU=0 Radius=2 StartAngle=5.4646 EndAngle=6.28319
    g12: ArcOfCircle CenterX=-75.5 CenterY=-28 CenterZ=0 NormalX=0 NormalY=0 NormalZ=1 AngleXU=0 Radius=2 StartAngle=3.14159 EndAngle=3.96017
    g13: ArcOfCircle CenterX=75.5 CenterY=41 CenterZ=0 NormalX=0 NormalY=0 NormalZ=1 AngleXU=0 Radius=2 StartAngle=-1.8e-15 EndAngle=0.629894
    g14: ArcOfCircle CenterX=-75.5 CenterY=41 CenterZ=0 NormalX=0 NormalY=0 NormalZ=1 AngleXU=0 Radius=2 StartAngle=2.5117 EndAngle=3.14159
    g15: GeomPoint X=77.5 Y=0 Z=0
    g16: GeomPoint X=-77.5 Y=0 Z=0
    g17: LineSegment StartX=-77.5 StartY=-28 StartZ=0 EndX=-77.5 EndY=-26 EndZ=0
    g18: LineSegment StartX=-77.5 StartY=26 StartZ=0 EndX=-77.5 EndY=24 EndZ=0
    g19: LineSegment StartX=-77.5 StartY=24 StartZ=0 EndX=-77.5 EndY=-24 EndZ=0
    g20: LineSegment StartX=-77.5 StartY=-26 StartZ=0 EndX=-77.5 EndY=-24 EndZ=0
    g21: LineSegment StartX=77.5 StartY=26 StartZ=0 EndX=77.5 EndY=24 EndZ=0
    g22: LineSegment StartX=77.5 StartY=24 StartZ=0 EndX=77.5 EndY=-24 EndZ=0
    g23: LineSegment StartX=77.5 StartY=-24 StartZ=0 EndX=77.5 EndY=-26 EndZ=0
    g24: Circle CenterX=16.5 CenterY=92.6846 CenterZ=0 NormalX=0 NormalY=0 NormalZ=1 AngleXU=0 Radius=1.25
    g25: Circle CenterX=60 CenterY=31.5 CenterZ=0 NormalX=0 NormalY=0 NormalZ=1 AngleXU=0 Radius=1.25
    g26: Circle CenterX=-60 CenterY=31.5 CenterZ=0 NormalX=0 NormalY=0 NormalZ=1 AngleXU=0 Radius=1.25
    g27: Circle CenterX=-60 CenterY=-21.5 CenterZ=0 NormalX=0 NormalY=0 NormalZ=1 AngleXU=0 Radius=1.25
    g28: Circle CenterX=60 CenterY=-21.5 CenterZ=0 NormalX=0 NormalY=0 NormalZ=1 AngleXU=0 Radius=1.25
    g29: LineSegment StartX=-60 StartY=-21.5 StartZ=0 EndX=60 EndY=-21.5 EndZ=0
    g30: LineSegment StartX=-60 StartY=31.5 StartZ=0 EndX=60 EndY=31.5 EndZ=0
    g31: LineSegment StartX=-16.5 StartY=92.6846 StartZ=0 EndX=16.5 EndY=92.6846 EndZ=0
    g32: GeomPoint X=0 Y=92.6846 Z=0
    g33: GeomPoint X=0 Y=31.5 Z=0
    g34: GeomPoint X=0 Y=-21.5 Z=0
    g35: LineSegment StartX=-60 StartY=31.5 StartZ=0 EndX=-60 EndY=-21.5 EndZ=0
    g36: Circle CenterX=3.5 CenterY=92.6846 CenterZ=0 NormalX=0 NormalY=0 NormalZ=1 AngleXU=0 Radius=1.25
  constraints (92):
    c: PointOnObject(g0,g-2)
    c: Horizontal(g2)
    c: Coincident(g4,g-1)
    c: PointOnObject(g4,g-2)
    c: Tangent(g1,g5) = 1.5708
    c: Tangent(g2,g5) = 1.5708
    c: Tangent(g2,g6) = 1.5708
    c: Tangent(g3,g6) = 1.5708
    c: Equal(g6,g5)
    c: Symmetric(g2,g2,g4)
    c: PointOnObject(g7,g-2)
    c: PointOnObject(g7,g0)
    c: DistanceY(g7,g2) = 170
    c: Radius(g6) = 5
    c: DistanceX(g2,g2) = 50
    c: Vertical(g8)
    c: Vertical(g9)
    c: Vertical(g10)
    c: Equal(g1,g3)
    c: Tangent(g0,g11) = -1.5708
    c: Tangent(g9,g11) = 1.5708
    c: Tangent(g0,g12) = -1.5708
    c: Equal(g11,g12)
    c: Radius(g11) = 2
    c: Tangent(g8,g13) = -1.5708
    c: Tangent(g3,g13) = 1.5708
    c: Tangent(g1,g14) = 1.5708
    c: Tangent(g10,g14) = 1.5708
    c: Equal(g13,g14)
    c: DistanceY(g9,g9) = 2
    c: DistanceY(g8,g8) = 15
    c: Radius(g13) = 2
    c: Diameter(g0) = 225
    c: PointOnObject(g15,g-1)
    c: PointOnObject(g16,g-1)
    c: Symmetric(g10,g17,g16)
    c: Symmetric(g8,g9,g15)
    c: Coincident(g17,g12)
    c: Vertical(g17)
    c: Equal(g10,g8)
    c: Equal(g9,g17)
    c: DistanceX(g12,g9) = 155
    c: Coincident(g18,g10)
    c: Vertical(g18)
    c: Coincident(g19,g18)
    c: Vertical(g19)
    c: Coincident(g20,g17)
    c: Vertical(g20)
    c: Equal(g20,g18)
    c: Coincident(g19,g20)
    c: Tangent(g12,g17)
    c: Coincident(g21,g8)
    c: Vertical(g21)
    c: Coincident(g22,g21)
    c: Vertical(g22)
    c: Coincident(g23,g22)
    c: Coincident(g23,g9)
    c: Equal(g23,g21)
    c: Vertical(g23)
    c: DistanceY(g21,g8) = 2
    c: Equal(g18,g21)
    c: DistanceY(g22,g21) = 48
    c: Coincident(g29,g27)
    c: Coincident(g29,g28)
    c: Horizontal(g29)
    c: Coincident(g30,g26)
    c: Coincident(g30,g25)
    c: Horizontal(g30)
    c: Equal(g27,g28)
    c: Equal(g28,g25)
    c: Equal(g25,g24)
    c: Equal(g25,g26)
    c: Coincident(g31,g24)
    c: Horizontal(g31)
    c: PointOnObject(g32,g4)
    c: PointOnObject(g33,g4)
    c: PointOnObject(g34,g-2)
    c: Symmetric(g26,g25,g33)
    c: Symmetric(g27,g28,g34)
    c: Coincident(g35,g26)
    c: Coincident(g35,g27)
    c: Vertical(g35)
    c: DistanceX(g25,g8) = 17.5
    c: DistanceY(g24,g2) = 17.5
    c: Diameter(g28) = 2.5
    c: DistanceY(g8,g25) = 5.5
    c: DistanceX(g24,g2) = 8.5
    c: Symmetric(g31,g24,g32)
    c: PointOnObject(g36,g31)
    c: Equal(g24,g36)
    c: DistanceX(g32,g36) = 3.5
    c: DistanceY(g9,g28) = 6.5
FEATURE [PartDesign::Pocket] Pocket009  label="TopBrack_MtHoles"
  BaseFeature = -> Pocket006
  Length = 7
  Length2 = 100
  Profile = -> Sketch021
  Type = 0
  expr: Length = <<params>>.shell_topbrack_vertheight
FEATURE [Sketcher::SketchObject] Sketch023  label="Sketch_TopMount_CSunk"
  FullyConstrained = true
  MapMode = 5
  Placement = pos=(0,0,37.5) rot=(0,0,1;0rad)
  Support = -> [DatumPlane007]
  expr: Constraints[71] = <<params>>.shell_overhang_leng + <<params>>.shell_topbrack_width - <<params>>.shell_topbrack_hole_offset
  expr: Constraints[173] = <<params>>.m2_nut_clear_flat
  expr: Constraints[29] = <<params>>.front_vert_edge
  expr: Constraints[198] = <<params>>.shell_topbrack_hole_offset
  expr: Constraints[32] = <<params>>.front_diameter
  expr: Constraints[74] = <<params>>.shell_topbrack_hole_offset + <<params>>.std_rad
  expr: Constraints[199] = <<params>>.top_brack_front_leng - <<params>>.shell_topbrack_hole_offset
  expr: Constraints[59] = <<params>>.std_rad
  expr: Constraints[12] = <<params>>.plate_length
  expr: Constraints[41] = <<params>>.plate_width
  expr: Constraints[14] = <<params>>.tail_width
  expr: Constraints[23] = <<params>>.std_rad
  expr: Constraints[61] = <<params>>.wheel_well_clearance
  expr: Constraints[31] = <<params>>.std_rad
  expr: Constraints[30] = <<params>>.back_vert_edge
  expr: Constraints[77] = <<params>>.shell_overhang_leng + <<params>>.shell_topbrack_width - <<params>>.shell_topbrack_hole_offset
  expr: Constraints[13] = <<params>>.tail_rad
  expr: Constraints[76] = <<params>>.shell_topbrack_width * 2 - <<params>>.std_rad - <<params>>.shell_topbrack_hole_offset
  sketch-geometry (73):
    g0: ArcOfCircle CenterX=0 CenterY=52.6846 CenterZ=0 NormalX=0 NormalY=0 NormalZ=1 AngleXU=0 Radius=112.5 StartAngle=3.96017 EndAngle=5.4646
    g1: LineSegment StartX=-77.1162 StartY=42.1781 StartZ=0 EndX=-29.0404 EndY=108.13 EndZ=0
    g2: LineSegment StartX=-25 StartY=110.185 StartZ=0 EndX=25 EndY=110.185 EndZ=0
    g3: LineSegment StartX=29.0404 StartY=108.13 StartZ=0 EndX=77.1162 EndY=42.1781 EndZ=0
    g4: LineSegment StartX=0 StartY=0 StartZ=0 EndX=0 EndY=110.185 EndZ=0
    g5: ArcOfCircle CenterX=-25 CenterY=105.185 CenterZ=0 NormalX=0 NormalY=0 NormalZ=1 AngleXU=0 Radius=5 StartAngle=1.5708 EndAngle=2.5117
    g6: ArcOfCircle CenterX=25 CenterY=105.185 CenterZ=0 NormalX=0 NormalY=0 NormalZ=1 AngleXU=0 Radius=5 StartAngle=0.629894 EndAngle=1.5708
    g7: GeomPoint X=0 Y=-59.8154 Z=0
    g8: LineSegment StartX=77.5 StartY=26 StartZ=0 EndX=77.5 EndY=41 EndZ=0
    g9: LineSegment StartX=77.5 StartY=-26 StartZ=0 EndX=77.5 EndY=-28 EndZ=0
    g10: LineSegment StartX=-77.5 StartY=26 StartZ=0 EndX=-77.5 EndY=41 EndZ=0
    g11: ArcOfCircle CenterX=75.5 CenterY=-28 CenterZ=0 NormalX=0 NormalY=0 NormalZ=1 AngleXU=0 Radius=2 StartAngle=5.4646 EndAngle=6.28319
    g12: ArcOfCircle CenterX=-75.5 CenterY=-28 CenterZ=0 NormalX=0 NormalY=0 NormalZ=1 AngleXU=0 Radius=2 StartAngle=3.14159 EndAngle=3.96017
    g13: ArcOfCircle CenterX=75.5 CenterY=41 CenterZ=0 NormalX=0 NormalY=0 NormalZ=1 AngleXU=0 Radius=2 StartAngle=-9e-16 EndAngle=0.629894
    g14: ArcOfCircle CenterX=-75.5 CenterY=41 CenterZ=0 NormalX=0 NormalY=0 NormalZ=1 AngleXU=0 Radius=2 StartAngle=2.5117 EndAngle=3.14159
    g15: GeomPoint X=77.5 Y=0 Z=0
    g16: GeomPoint X=-77.5 Y=0 Z=0
    g17: LineSegment StartX=-77.5 StartY=-28 StartZ=0 EndX=-77.5 EndY=-26 EndZ=0
    g18: LineSegment StartX=-77.5 StartY=26 StartZ=0 EndX=-77.5 EndY=24 EndZ=0
    g19: LineSegment StartX=-77.5 StartY=24 StartZ=0 EndX=-77.5 EndY=-24 EndZ=0
    g20: LineSegment StartX=-77.5 StartY=-26 StartZ=0 EndX=-77.5 EndY=-24 EndZ=0
    g21: LineSegment StartX=77.5 StartY=26 StartZ=0 EndX=77.5 EndY=24 EndZ=0
    g22: LineSegment StartX=77.5 StartY=24 StartZ=0 EndX=77.5 EndY=-24 EndZ=0
    g23: LineSegment StartX=77.5 StartY=-24 StartZ=0 EndX=77.5 EndY=-26 EndZ=0
    g24: LineSegment StartX=-60 StartY=-21.5 StartZ=0 EndX=60 EndY=-21.5 EndZ=0
    g25: LineSegment StartX=-60 StartY=31.5 StartZ=0 EndX=60 EndY=31.5 EndZ=0
    g26: LineSegment StartX=-16.5 StartY=92.6846 StartZ=0 EndX=16.5 EndY=92.6846 EndZ=0
    g27: GeomPoint X=0 Y=92.6846 Z=0
    g28: GeomPoint X=0 Y=31.5 Z=0
    g29: GeomPoint X=0 Y=-21.5 Z=0
    g30: LineSegment StartX=-60 StartY=31.5 StartZ=0 EndX=-60 EndY=-21.5 EndZ=0
    g31: LineSegment StartX=-62.4249 StartY=31.5 StartZ=0 EndX=-61.2124 EndY=29.4 EndZ=0
    g32: LineSegment StartX=-61.2124 StartY=29.4 StartZ=0 EndX=-58.7876 EndY=29.4 EndZ=0
    g33: LineSegment StartX=-58.7876 StartY=29.4 StartZ=0 EndX=-57.5751 EndY=31.5 EndZ=0
    g34: LineSegment StartX=-57.5751 StartY=31.5 StartZ=0 EndX=-58.7876 EndY=33.6 EndZ=0
    g35: LineSegment StartX=-58.7876 StartY=33.6 StartZ=0 EndX=-61.2124 EndY=33.6 EndZ=0
    g36: LineSegment StartX=-61.2124 StartY=33.6 StartZ=0 EndX=-62.4249 EndY=31.5 EndZ=0
    g37: Circle CenterX=-60 CenterY=31.5 CenterZ=0 NormalX=0 NormalY=0 NormalZ=1 AngleXU=0 Radius=2.42487
    g38: LineSegment StartX=-62.4249 StartY=-21.5 StartZ=0 EndX=-61.2124 EndY=-23.6 EndZ=0
    g39: LineSegment StartX=-61.2124 StartY=-23.6 StartZ=0 EndX=-58.7876 EndY=-23.6 EndZ=0
    g40: LineSegment StartX=-58.7876 StartY=-23.6 StartZ=0 EndX=-57.5751 EndY=-21.5 EndZ=0
    g41: LineSegment StartX=-57.5751 StartY=-21.5 StartZ=0 EndX=-58.7876 EndY=-19.4 EndZ=0
    g42: LineSegment StartX=-58.7876 StartY=-19.4 StartZ=0 EndX=-61.2124 EndY=-19.4 EndZ=0
    g43: LineSegment StartX=-61.2124 StartY=-19.4 StartZ=0 EndX=-62.4249 EndY=-21.5 EndZ=0
    g44: Circle CenterX=-60 CenterY=-21.5 CenterZ=0 NormalX=0 NormalY=0 NormalZ=1 AngleXU=0 Radius=2.42487
    g45: LineSegment StartX=62.4249 StartY=-21.5 StartZ=0 EndX=61.2124 EndY=-19.4 EndZ=0
    g46: LineSegment StartX=61.2124 StartY=-19.4 StartZ=0 EndX=58.7876 EndY=-19.4 EndZ=0
    g47: LineSegment StartX=58.7876 StartY=-19.4 StartZ=0 EndX=57.5751 EndY=-21.5 EndZ=0
    g48: LineSegment StartX=57.5751 StartY=-21.5 StartZ=0 EndX=58.7876 EndY=-23.6 EndZ=0
    g49: LineSegment StartX=58.7876 StartY=-23.6 StartZ=0 EndX=61.2124 EndY=-23.6 EndZ=0
    g50: LineSegment StartX=61.2124 StartY=-23.6 StartZ=0 EndX=62.4249 EndY=-21.5 EndZ=0
    g51: Circle CenterX=60 CenterY=-21.5 CenterZ=0 NormalX=0 NormalY=0 NormalZ=1 AngleXU=0 Radius=2.42487
    g52: LineSegment StartX=62.4249 StartY=31.5 StartZ=0 EndX=61.2124 EndY=33.6 EndZ=0
    g53: LineSegment StartX=61.2124 StartY=33.6 StartZ=0 EndX=58.7876 EndY=33.6 EndZ=0
    g54: LineSegment StartX=58.7876 StartY=33.6 StartZ=0 EndX=57.5751 EndY=31.5 EndZ=0
    g55: LineSegment StartX=57.5751 StartY=31.5 StartZ=0 EndX=58.7876 EndY=29.4 EndZ=0
    g56: LineSegment StartX=58.7876 StartY=29.4 StartZ=0 EndX=61.2124 EndY=29.4 EndZ=0
    g57: LineSegment StartX=61.2124 StartY=29.4 StartZ=0 EndX=62.4249 EndY=31.5 EndZ=0
    g58: Circle CenterX=60 CenterY=31.5 CenterZ=0 NormalX=0 NormalY=0 NormalZ=1 AngleXU=0 Radius=2.42487
    g59: LineSegment StartX=16.5 StartY=95.1094 StartZ=0 EndX=14.4 EndY=93.897 EndZ=0
    g60: LineSegment StartX=14.4 StartY=93.897 StartZ=0 EndX=14.4 EndY=91.4721 EndZ=0
    g61: LineSegment StartX=14.4 StartY=91.4721 StartZ=0 EndX=16.5 EndY=90.2597 EndZ=0
    g62: LineSegment StartX=16.5 StartY=90.2597 StartZ=0 EndX=18.6 EndY=91.4721 EndZ=0
    g63: LineSegment StartX=18.6 StartY=91.4721 StartZ=0 EndX=18.6 EndY=93.897 EndZ=0
    g64: LineSegment StartX=18.6 StartY=93.897 StartZ=0 EndX=16.5 EndY=95.1094 EndZ=0
    g65: Circle CenterX=16.5 CenterY=92.6846 CenterZ=0 NormalX=0 NormalY=0 NormalZ=1 AngleXU=0 Radius=2.42487
    g66: LineSegment StartX=3.5 StartY=95.1094 StartZ=0 EndX=1.4 EndY=93.897 EndZ=0
    g67: LineSegment StartX=1.4 StartY=93.897 StartZ=0 EndX=1.4 EndY=91.4721 EndZ=0
    g68: LineSegment StartX=1.4 StartY=91.4721 StartZ=0 EndX=3.5 EndY=90.2597 EndZ=0
    g69: LineSegment StartX=3.5 StartY=90.2597 StartZ=0 EndX=5.6 EndY=91.4721 EndZ=0
    g70: LineSegment StartX=5.6 StartY=91.4721 StartZ=0 EndX=5.6 EndY=93.897 EndZ=0
    g71: LineSegment StartX=5.6 StartY=93.897 StartZ=0 EndX=3.5 EndY=95.1094 EndZ=0
    g72: Circle CenterX=3.5 CenterY=92.6846 CenterZ=0 NormalX=0 NormalY=0 NormalZ=1 AngleXU=0 Radius=2.42487
  constraints (176):
    c: PointOnObject(g0,g-2)
    c: Horizontal(g2)
    c: Coincident(g4,g-1)
    c: PointOnObject(g4,g-2)
    c: Tangent(g1,g5) = 1.5708
    c: Tangent(g2,g5) = 1.5708
    c: Tangent(g2,g6) = 1.5708
    c: Tangent(g3,g6) = 1.5708
    c: Equal(g6,g5)
    c: Symmetric(g2,g2,g4)
    c: PointOnObject(g7,g-2)
    c: PointOnObject(g7,g0)
    c: DistanceY(g7,g2) = 170
    c: Radius(g6) = 5
    c: DistanceX(g2,g2) = 50
    c: Vertical(g8)
    c: Vertical(g9)
    c: Vertical(g10)
    c: Equal(g1,g3)
    c: Tangent(g0,g11) = -1.5708
    c: Tangent(g9,g11) = 1.5708
    c: Tangent(g0,g12) = -1.5708
    c: Equal(g11,g12)
    c: Radius(g11) = 2
    c: Tangent(g8,g13) = -1.5708
    c: Tangent(g3,g13) = 1.5708
    c: Tangent(g1,g14) = 1.5708
    c: Tangent(g10,g14) = 1.5708
    c: Equal(g13,g14)
    c: DistanceY(g9,g9) = 2
    c: DistanceY(g8,g8) = 15
    c: Radius(g13) = 2
    c: Diameter(g0) = 225
    c: PointOnObject(g15,g-1)
    c: PointOnObject(g16,g-1)
    c: Symmetric(g10,g17,g16)
    c: Symmetric(g8,g9,g15)
    c: Coincident(g17,g12)
    c: Vertical(g17)
    c: Equal(g10,g8)
    c: Equal(g9,g17)
    c: DistanceX(g12,g9) = 155
    c: Coincident(g18,g10)
    c: Vertical(g18)
    c: Coincident(g19,g18)
    c: Vertical(g19)
    c: Coincident(g20,g17)
    c: Vertical(g20)
    c: Equal(g20,g18)
    c: Coincident(g19,g20)
    c: Tangent(g12,g17)
    c: Coincident(g21,g8)
    c: Vertical(g21)
    c: Coincident(g22,g21)
    c: Vertical(g22)
    c: Coincident(g23,g22)
    c: Coincident(g23,g9)
    c: Equal(g23,g21)
    c: Vertical(g23)
    c: DistanceY(g21,g8) = 2
    c: Equal(g18,g21)
    c: DistanceY(g22,g21) = 48
    c: Horizontal(g24)
    c: Horizontal(g25)
    c: Horizontal(g26)
    c: PointOnObject(g27,g4)
    c: PointOnObject(g28,g4)
    c: PointOnObject(g29,g-2)
    c: Vertical(g30)
    c: Coincident(g24,g30)
    c: Symmetric(g24,g24,g29)
    c: DistanceX(g25,g8) = 17.5
    c: Coincident(g25,g30)
    c: Symmetric(g25,g25,g28)
    c: DistanceY(g8,g25) = 5.5
    c: Symmetric(g26,g26,g27)
    c: DistanceX(g26,g2) = 8.5
    c: DistanceY(g26,g2) = 17.5
    c: Coincident(g31,g32)
    c: Coincident(g32,g33)
    c: Coincident(g33,g34)
    c: Coincident(g34,g35)
    c: Coincident(g35,g36)
    c: Coincident(g36,g31)
    c: Equal(g31, g32-g36) x5
    c: PointOnObject(g31,g37)
    c: PointOnObject(g32,g37)
    c: PointOnObject(g33,g37)
    c: PointOnObject(g34,g37)
    c: PointOnObject(g35,g37)
    c: PointOnObject(g36,g37)
    c: Coincident(g37,g25)
    c: Coincident(g38,g39)
    c: Coincident(g39,g40)
    c: Coincident(g40,g41)
    c: Coincident(g41,g42)
    c: Coincident(g42,g43)
    c: Coincident(g43,g38)
    c: Equal(g38, g39-g43) x5
    c: PointOnObject(g38,g44)
    c: PointOnObject(g39,g44)
    c: PointOnObject(g40,g44)
    c: PointOnObject(g41,g44)
    c: PointOnObject(g42,g44)
    c: PointOnObject(g43,g44)
    c: Coincident(g44,g24)
    c: Coincident(g45,g46)
    c: Coincident(g46,g47)
    c: Coincident(g47,g48)
    c: Coincident(g48,g49)
    c: Coincident(g49,g50)
    c: Coincident(g50,g45)
    c: Equal(g45, g46-g50) x5
    c: PointOnObject(g45,g51)
    c: PointOnObject(g46,g51)
    c: PointOnObject(g47,g51)
    c: PointOnObject(g48,g51)
    c: PointOnObject(g49,g51)
    c: PointOnObject(g50,g51)
    c: Coincident(g51,g24)
    c: Coincident(g52,g53)
    c: Coincident(g53,g54)
    c: Coincident(g54,g55)
    c: Coincident(g55,g56)
    c: Coincident(g56,g57)
    c: Coincident(g57,g52)
    c: Equal(g52, g53-g57) x5
    c: PointOnObject(g52,g58)
    c: PointOnObject(g53,g58)
    c: PointOnObject(g54,g58)
    c: PointOnObject(g55,g58)
    c: PointOnObject(g56,g58)
    c: PointOnObject(g57,g58)
    c: Coincident(g58,g25)
    c: Coincident(g59,g60)
    c: Coincident(g60,g61)
    c: Coincident(g61,g62)
    c: Coincident(g62,g63)
    c: Coincident(g63,g64)
    c: Coincident(g64,g59)
    c: Equal(g59, g60-g64) x5
    c: PointOnObject(g59,g65)
    c: PointOnObject(g60,g65)
    c: PointOnObject(g61,g65)
    c: PointOnObject(g62,g65)
    c: PointOnObject(g63,g65)
    c: PointOnObject(g64,g65)
    c: Coincident(g65,g26)
    c: Equal(g58,g65)
    c: Equal(g58,g37)
    c: Equal(g37,g44)
    c: Equal(g44,g51)
    c: Horizontal(g46)
    c: DistanceY(g49,g45) = 4.2
    c: Horizontal(g42)
    c: Horizontal(g35)
    c: Horizontal(g53)
    c: Vertical(g63)
    c: Coincident(g66,g67)
    c: Coincident(g67,g68)
    c: Coincident(g68,g69)
    c: Coincident(g69,g70)
    c: Coincident(g70,g71)
    c: Coincident(g71,g66)
    c: Equal(g66, g67-g71) x5
    c: PointOnObject(g66,g72)
    c: PointOnObject(g67,g72)
    c: PointOnObject(g68,g72)
    c: PointOnObject(g69,g72)
    c: PointOnObject(g70,g72)
    c: PointOnObject(g71,g72)
    c: PointOnObject(g72,g26)
    c: Vertical(g67)
    c: Equal(g72,g65)
    c: DistanceX(g27,g72) = 3.5
    c: DistanceY(g9,g24) = 6.5
FEATURE [PartDesign::Pocket] Pocket010  label="TopBrack_CSunk"
  BaseFeature = -> Pocket009
  Length = 2
  Length2 = 100
  Profile = -> Sketch023
  Type = 0
  expr: Length = <<params>>.shell_topbrack_csunk_height
FEATURE [Sketcher::SketchObject] Sketch024  label="Sketch_TopMount_Slot"
  FullyConstrained = true
  MapMode = 5
  Placement = pos=(0,0,40) rot=(0,0,1;0rad)
  Support = -> [DatumPlane008]
  expr: Constraints[59] = <<params>>.std_rad
  expr: Constraints[205] = <<params>>.shell_topbrack_hole_offset
  expr: Constraints[217] = <<params>>.top_brack_front_leng - <<params>>.shell_topbrack_hole_offset
  expr: Constraints[29] = <<params>>.front_vert_edge
  expr: Constraints[74] = <<params>>.shell_topbrack_hole_offset + <<params>>.std_rad
  expr: Constraints[32] = <<params>>.front_diameter
  expr: Constraints[14] = <<params>>.tail_width
  expr: Constraints[41] = <<params>>.plate_width
  expr: Constraints[12] = <<params>>.plate_length
  expr: Constraints[190] = <<params>>.m2_nut_clear_flat
  expr: Constraints[76] = <<params>>.shell_topbrack_width * 2 - <<params>>.std_rad - <<params>>.shell_topbrack_hole_offset
  expr: Constraints[71] = <<params>>.shell_overhang_leng + <<params>>.shell_topbrack_width - <<params>>.shell_topbrack_hole_offset
  expr: Constraints[77] = <<params>>.shell_overhang_leng + <<params>>.shell_topbrack_width - <<params>>.shell_topbrack_hole_offset
  expr: Constraints[13] = <<params>>.tail_rad
  expr: Constraints[30] = <<params>>.back_vert_edge
  expr: Constraints[31] = <<params>>.std_rad
  expr: Constraints[23] = <<params>>.std_rad
  expr: Constraints[61] = <<params>>.wheel_well_clearance
  sketch-geometry (79):
    g0: ArcOfCircle CenterX=0 CenterY=52.6846 CenterZ=0 NormalX=0 NormalY=0 NormalZ=1 AngleXU=0 Radius=112.5 StartAngle=3.96017 EndAngle=5.4646
    g1: LineSegment StartX=-77.1162 StartY=42.1781 StartZ=0 EndX=-29.0404 EndY=108.13 EndZ=0
    g2: LineSegment StartX=-25 StartY=110.185 StartZ=0 EndX=25 EndY=110.185 EndZ=0
    g3: LineSegment StartX=29.0404 StartY=108.13 StartZ=0 EndX=77.1162 EndY=42.1781 EndZ=0
    g4: LineSegment StartX=0 StartY=0 StartZ=0 EndX=0 EndY=110.185 EndZ=0
    g5: ArcOfCircle CenterX=-25 CenterY=105.185 CenterZ=0 NormalX=0 NormalY=0 NormalZ=1 AngleXU=0 Radius=5 StartAngle=1.5708 EndAngle=2.5117
    g6: ArcOfCircle CenterX=25 CenterY=105.185 CenterZ=0 NormalX=0 NormalY=0 NormalZ=1 AngleXU=0 Radius=5 StartAngle=0.629894 EndAngle=1.5708
    g7: GeomPoint X=0 Y=-59.8154 Z=0
    g8: LineSegment StartX=77.5 StartY=26 StartZ=0 EndX=77.5 EndY=41 EndZ=0
    g9: LineSegment StartX=77.5 StartY=-26 StartZ=0 EndX=77.5 EndY=-28 EndZ=0
    g10: LineSegment StartX=-77.5 StartY=26 StartZ=0 EndX=-77.5 EndY=41 EndZ=0
    g11: ArcOfCircle CenterX=75.5 CenterY=-28 CenterZ=0 NormalX=0 NormalY=0 NormalZ=1 AngleXU=0 Radius=2 StartAngle=5.4646 EndAngle=6.28319
    g12: ArcOfCircle CenterX=-75.5 CenterY=-28 CenterZ=0 NormalX=0 NormalY=0 NormalZ=1 AngleXU=0 Radius=2 StartAngle=3.14159 EndAngle=3.96017
    g13: ArcOfCircle CenterX=75.5 CenterY=41 CenterZ=0 NormalX=0 NormalY=0 NormalZ=1 AngleXU=0 Radius=2 StartAngle=1.7e-15 EndAngle=0.629894
    g14: ArcOfCircle CenterX=-75.5 CenterY=41 CenterZ=0 NormalX=0 NormalY=0 NormalZ=1 AngleXU=0 Radius=2 StartAngle=2.5117 EndAngle=3.14159
    g15: GeomPoint X=77.5 Y=0 Z=0
    g16: GeomPoint X=-77.5 Y=0 Z=0
    g17: LineSegment StartX=-77.5 StartY=-28 StartZ=0 EndX=-77.5 EndY=-26 EndZ=0
    g18: LineSegment StartX=-77.5 StartY=26 StartZ=0 EndX=-77.5 EndY=24 EndZ=0
    g19: LineSegment StartX=-77.5 StartY=24 StartZ=0 EndX=-77.5 EndY=-24 EndZ=0
    g20: LineSegment StartX=-77.5 StartY=-26 StartZ=0 EndX=-77.5 EndY=-24 EndZ=0
    g21: LineSegment StartX=77.5 StartY=26 StartZ=0 EndX=77.5 EndY=24 EndZ=0
    g22: LineSegment StartX=77.5 StartY=24 StartZ=0 EndX=77.5 EndY=-24 EndZ=0
    g23: LineSegment StartX=77.5 StartY=-24 StartZ=0 EndX=77.5 EndY=-26 EndZ=0
    g24: LineSegment StartX=-60 StartY=-21.5 StartZ=0 EndX=60 EndY=-21.5 EndZ=0
    g25: LineSegment StartX=-60 StartY=31.5 StartZ=0 EndX=60 EndY=31.5 EndZ=0
    g26: LineSegment StartX=-16.5 StartY=92.6846 StartZ=0 EndX=16.5 EndY=92.6846 EndZ=0
    g27: GeomPoint X=0 Y=92.6846 Z=0
    g28: GeomPoint X=0 Y=31.5 Z=0
    g29: GeomPoint X=0 Y=-21.5 Z=0
    g30: LineSegment StartX=-60 StartY=31.5 StartZ=0 EndX=-60 EndY=-21.5 EndZ=0
    g31: LineSegment StartX=-62.4249 StartY=31.5 StartZ=0 EndX=-61.2124 EndY=29.4 EndZ=0
    g32: LineSegment StartX=-61.2124 StartY=29.4 StartZ=0 EndX=-58.7876 EndY=29.4 EndZ=0
    g33: LineSegment StartX=-58.7876 StartY=33.6 StartZ=0 EndX=-61.2124 EndY=33.6 EndZ=0
    g34: LineSegment StartX=-61.2124 StartY=33.6 StartZ=0 EndX=-62.4249 EndY=31.5 EndZ=0
    g35: Circle CenterX=-60 CenterY=31.5 CenterZ=0 NormalX=0 NormalY=0 NormalZ=1 AngleXU=0 Radius=2.42487
    g36: LineSegment StartX=-62.4249 StartY=-21.5 StartZ=0 EndX=-61.2124 EndY=-23.6 EndZ=0
    g37: LineSegment StartX=-61.2124 StartY=-23.6 StartZ=0 EndX=-58.7876 EndY=-23.6 EndZ=0
    g38: LineSegment StartX=-58.7876 StartY=-19.4 StartZ=0 EndX=-61.2124 EndY=-19.4 EndZ=0
    g39: LineSegment StartX=-61.2124 StartY=-19.4 StartZ=0 EndX=-62.4249 EndY=-21.5 EndZ=0
    g40: Circle CenterX=-60 CenterY=-21.5 CenterZ=0 NormalX=0 NormalY=0 NormalZ=1 AngleXU=0 Radius=2.42487
    g41: LineSegment StartX=62.4249 StartY=31.5 StartZ=0 EndX=61.2124 EndY=33.6 EndZ=0
    g42: LineSegment StartX=61.2124 StartY=33.6 StartZ=0 EndX=58.7876 EndY=33.6 EndZ=0
    g43: LineSegment StartX=58.7876 StartY=29.4 StartZ=0 EndX=61.2124 EndY=29.4 EndZ=0
    g44: LineSegment StartX=61.2124 StartY=29.4 StartZ=0 EndX=62.4249 EndY=31.5 EndZ=0
    g45: Circle CenterX=60 CenterY=31.5 CenterZ=0 NormalX=0 NormalY=0 NormalZ=1 AngleXU=0 Radius=2.42487
    g46: LineSegment StartX=58.7876 StartY=-19.4 StartZ=0 EndX=33.7876 EndY=-19.4 EndZ=0
    g47: LineSegment StartX=33.7876 StartY=-19.4 StartZ=0 EndX=33.7876 EndY=-23.6 EndZ=0
    g48: LineSegment StartX=-58.7876 StartY=-23.6 StartZ=0 EndX=-33.7876 EndY=-23.6 EndZ=0
    g49: LineSegment StartX=-58.7876 StartY=-19.4 StartZ=0 EndX=-33.7876 EndY=-19.4 EndZ=0
    g50: LineSegment StartX=-33.7876 StartY=-19.4 StartZ=0 EndX=-33.7876 EndY=-23.6 EndZ=0
    g51: LineSegment StartX=58.7876 StartY=33.6 StartZ=0 EndX=33.7876 EndY=33.6 EndZ=0
    g52: LineSegment StartX=58.7876 StartY=29.4 StartZ=0 EndX=33.7876 EndY=29.4 EndZ=0
    g53: LineSegment StartX=33.7876 StartY=29.4 StartZ=0 EndX=33.7876 EndY=33.6 EndZ=0
    g54: LineSegment StartX=-58.7876 StartY=29.4 StartZ=0 EndX=-33.7876 EndY=29.4 EndZ=0
    g55: LineSegment StartX=-58.7876 StartY=33.6 StartZ=0 EndX=-33.7876 EndY=33.6 EndZ=0
    g56: LineSegment StartX=-33.7876 StartY=33.6 StartZ=0 EndX=-33.7876 EndY=29.4 EndZ=0
    g57: LineSegment StartX=16.5 StartY=95.1094 StartZ=0 EndX=14.4 EndY=93.897 EndZ=0
    g58: LineSegment StartX=14.4 StartY=93.897 StartZ=0 EndX=14.4 EndY=91.4721 EndZ=0
    g59: LineSegment StartX=18.6 StartY=91.4721 StartZ=0 EndX=18.6 EndY=93.897 EndZ=0
    g60: LineSegment StartX=18.6 StartY=93.897 StartZ=0 EndX=16.5 EndY=95.1094 EndZ=0
    g61: Circle CenterX=16.5 CenterY=92.6846 CenterZ=0 NormalX=0 NormalY=0 NormalZ=1 AngleXU=0 Radius=2.42487
    g62: LineSegment StartX=62.4249 StartY=-21.5 StartZ=0 EndX=61.2124 EndY=-19.4 EndZ=0
    g63: LineSegment StartX=61.2124 StartY=-19.4 StartZ=0 EndX=58.7876 EndY=-19.4 EndZ=0
    g64: LineSegment StartX=58.7876 StartY=-23.6 StartZ=0 EndX=61.2124 EndY=-23.6 EndZ=0
    g65: LineSegment StartX=61.2124 StartY=-23.6 StartZ=0 EndX=62.4249 EndY=-21.5 EndZ=0
    g66: Circle CenterX=60 CenterY=-21.5 CenterZ=0 NormalX=0 NormalY=0 NormalZ=1 AngleXU=0 Radius=2.42487
    g67: LineSegment StartX=58.7876 StartY=-23.6 StartZ=0 EndX=33.7876 EndY=-23.6 EndZ=0
    g68: LineSegment StartX=14.4 StartY=91.4721 StartZ=0 EndX=14.4 EndY=66.4721 EndZ=0
    g69: LineSegment StartX=18.6 StartY=91.4721 StartZ=0 EndX=18.6 EndY=66.4721 EndZ=0
    g70: LineSegment StartX=14.4 StartY=66.4721 StartZ=0 EndX=18.6 EndY=66.4721 EndZ=0
    g71: LineSegment StartX=3.5 StartY=95.1094 StartZ=0 EndX=1.4 EndY=93.897 EndZ=0
    g72: LineSegment StartX=1.4 StartY=93.897 StartZ=0 EndX=1.4 EndY=91.4721 EndZ=0
    g73: LineSegment StartX=5.6 StartY=91.4721 StartZ=0 EndX=5.6 EndY=93.897 EndZ=0
    g74: LineSegment StartX=5.6 StartY=93.897 StartZ=0 EndX=3.5 EndY=95.1094 EndZ=0
    g75: Circle CenterX=3.5 CenterY=92.6846 CenterZ=0 NormalX=0 NormalY=0 NormalZ=1 AngleXU=0 Radius=2.42487
    g76: LineSegment StartX=1.4 StartY=91.4721 StartZ=0 EndX=1.4 EndY=66.4721 EndZ=0
    g77: LineSegment StartX=5.6 StartY=91.4721 StartZ=0 EndX=5.6 EndY=66.4721 EndZ=0
    g78: LineSegment StartX=1.4 StartY=66.4721 StartZ=0 EndX=5.6 EndY=66.4721 EndZ=0
  constraints (218):
    c: PointOnObject(g0,g-2)
    c: Horizontal(g2)
    c: Coincident(g4,g-1)
    c: PointOnObject(g4,g-2)
    c: Tangent(g1,g5) = 1.5708
    c: Tangent(g2,g5) = 1.5708
    c: Tangent(g2,g6) = 1.5708
    c: Tangent(g3,g6) = 1.5708
    c: Equal(g6,g5)
    c: Symmetric(g2,g2,g4)
    c: PointOnObject(g7,g-2)
    c: PointOnObject(g7,g0)
    c: DistanceY(g7,g2) = 170
    c: Radius(g6) = 5
    c: DistanceX(g2,g2) = 50
    c: Vertical(g8)
    c: Vertical(g9)
    c: Vertical(g10)
    c: Equal(g1,g3)
    c: Tangent(g0,g11) = -1.5708
    c: Tangent(g9,g11) = 1.5708
    c: Tangent(g0,g12) = -1.5708
    c: Equal(g11,g12)
    c: Radius(g11) = 2
    c: Tangent(g8,g13) = -1.5708
    c: Tangent(g3,g13) = 1.5708
    c: Tangent(g1,g14) = 1.5708
    c: Tangent(g10,g14) = 1.5708
    c: Equal(g13,g14)
    c: DistanceY(g9,g9) = 2
    c: DistanceY(g8,g8) = 15
    c: Radius(g13) = 2
    c: Diameter(g0) = 225
    c: PointOnObject(g15,g-1)
    c: PointOnObject(g16,g-1)
    c: Symmetric(g10,g17,g16)
    c: Symmetric(g8,g9,g15)
    c: Coincident(g17,g12)
    c: Vertical(g17)
    c: Equal(g10,g8)
    c: Equal(g9,g17)
    c: DistanceX(g12,g9) = 155
    c: Coincident(g18,g10)
    c: Vertical(g18)
    c: Coincident(g19,g18)
    c: Vertical(g19)
    c: Coincident(g20,g17)
    c: Vertical(g20)
    c: Equal(g20,g18)
    c: Coincident(g19,g20)
    c: Tangent(g12,g17)
    c: Coincident(g21,g8)
    c: Vertical(g21)
    c: Coincident(g22,g21)
    c: Vertical(g22)
    c: Coincident(g23,g22)
    c: Coincident(g23,g9)
    c: Equal(g23,g21)
    c: Vertical(g23)
    c: DistanceY(g21,g8) = 2
    c: Equal(g18,g21)
    c: DistanceY(g22,g21) = 48
    c: Horizontal(g24)
    c: Horizontal(g25)
    c: Horizontal(g26)
    c: PointOnObject(g27,g4)
    c: PointOnObject(g28,g4)
    c: PointOnObject(g29,g-2)
    c: Vertical(g30)
    c: Coincident(g24,g30)
    c: Symmetric(g24,g24,g29)
    c: DistanceX(g25,g8) = 17.5
    c: Coincident(g25,g30)
    c: Symmetric(g25,g25,g28)
    c: DistanceY(g8,g25) = 5.5
    c: Symmetric(g26,g26,g27)
    c: DistanceX(g26,g2) = 8.5
    c: DistanceY(g26,g2) = 17.5
    c: Coincident(g31,g32)
    c: Coincident(g33,g34)
    c: Coincident(g34,g31)
    c: Equal(g31,g32)
    c: Equal(g31,g33)
    c: Equal(g31,g34)
    c: PointOnObject(g31,g35)
    c: PointOnObject(g32,g35)
    c: PointOnObject(g33,g35)
    c: PointOnObject(g33,g35)
    c: PointOnObject(g34,g35)
    c: Coincident(g35,g25)
    c: Coincident(g36,g37)
    c: Coincident(g38,g39)
    c: Coincident(g39,g36)
    c: Equal(g36,g37)
    c: Equal(g36,g38)
    c: Equal(g36,g39)
    c: PointOnObject(g36,g40)
    c: PointOnObject(g37,g40)
    c: PointOnObject(g38,g40)
    c: PointOnObject(g38,g40)
    c: PointOnObject(g39,g40)
    c: Coincident(g40,g24)
    c: Coincident(g41,g42)
    c: Coincident(g43,g44)
    c: Coincident(g44,g41)
    c: Equal(g41,g42)
    c: Equal(g41,g43)
    c: Equal(g41,g44)
    c: PointOnObject(g41,g45)
    c: PointOnObject(g42,g45)
    c: PointOnObject(g43,g45)
    c: PointOnObject(g43,g45)
    c: PointOnObject(g44,g45)
    c: Coincident(g45,g25)
    c: Equal(g45,g35)
    c: Equal(g35,g40)
    c: Horizontal(g38)
    c: Horizontal(g33)
    c: Horizontal(g42)
    c: Horizontal(g46)
    c: Coincident(g47,g46)
    c: Vertical(g47)
    c: Horizontal(g37)
    c: Coincident(g48,g37)
    c: Horizontal(g48)
    c: Coincident(g49,g38)
    c: Horizontal(g49)
    c: Coincident(g50,g49)
    c: Coincident(g50,g48)
    c: Vertical(g50)
    c: Equal(g46,g49)
    c: Horizontal(g43)
    c: Coincident(g51,g42)
    c: Horizontal(g51)
    c: Coincident(g52,g43)
    c: Horizontal(g52)
    c: Coincident(g53,g52)
    c: Coincident(g53,g51)
    c: Vertical(g53)
    c: Equal(g52,g46)
    c: Horizontal(g32)
    c: Coincident(g54,g32)
    c: Horizontal(g54)
    c: Coincident(g55,g33)
    c: Horizontal(g55)
    c: Coincident(g56,g55)
    c: Coincident(g56,g54)
    c: Vertical(g56)
    c: Equal(g51,g55)
    c: Coincident(g57,g58)
    c: Coincident(g59,g60)
    c: Coincident(g60,g57)
    c: Equal(g57,g58)
    c: Equal(g57,g59)
    c: Equal(g57,g60)
    c: PointOnObject(g57,g61)
    c: PointOnObject(g58,g61)
    c: PointOnObject(g59,g61)
    c: PointOnObject(g59,g61)
    c: PointOnObject(g60,g61)
    c: Coincident(g61,g26)
    c: Vertical(g59)
    c: Equal(g61,g45)
    c: Coincident(g62,g63)
    c: Coincident(g64,g65)
    c: Coincident(g65,g62)
    c: Equal(g62,g63)
    c: Equal(g62,g64)
    c: Equal(g62,g65)
    c: PointOnObject(g62,g66)
    c: PointOnObject(g63,g66)
    c: PointOnObject(g64,g66)
    c: PointOnObject(g64,g66)
    c: PointOnObject(g65,g66)
    c: Coincident(g66,g24)
    c: Horizontal(g63)
    c: Horizontal(g64)
    c: Coincident(g46,g63)
    c: Coincident(g67,g64)
    c: Coincident(g67,g47)
    c: Horizontal(g67)
    c: Equal(g66,g45)
    c: Vertical(g58)
    c: Coincident(g68,g58)
    c: Vertical(g68)
    c: Coincident(g69,g59)
    c: Vertical(g69)
    c: Coincident(g70,g68)
    c: Coincident(g70,g69)
    c: Horizontal(g70)
    c: DistanceY(g64,g62) = 4.2
    c: Distance(g46) = 25
    c: Equal(g69,g51)
    c: Coincident(g71,g72)
    c: Coincident(g73,g74)
    c: Coincident(g74,g71)
    c: Equal(g71,g72)
    c: Equal(g71,g73)
    c: Equal(g71,g74)
    c: PointOnObject(g71,g75)
    c: PointOnObject(g72,g75)
    c: PointOnObject(g73,g75)
    c: PointOnObject(g73,g75)
    c: PointOnObject(g74,g75)
    c: PointOnObject(g75,g26)
    c: DistanceX(g27,g75) = 3.5
    c: Vertical(g72)
    c: Equal(g75,g61)
    c: Vertical(g73)
    c: Coincident(g76,g72)
    c: Vertical(g76)
    c: Coincident(g77,g73)
    c: Vertical(g77)
    c: Coincident(g78,g76)
    c: Coincident(g78,g77)
    c: Horizontal(g78)
    c: Equal(g68,g77)
    c: DistanceY(g9,g24) = 6.5
FEATURE [PartDesign::Pocket] Pocket011  label="TopBrack_HexSlot"
  BaseFeature = -> Pocket010
  Length = 2.5
  Length2 = 100
  Profile = -> Sketch024
  Type = 0
  expr: Length = <<params>>.shell_topbrack_slot_height
FEATURE [Sketcher::SketchObject] Sketch025
  FullyConstrained = true
  MapMode = 5
  Placement = pos=(0,0,0) rot=(1,0,0;1.5708rad)
  Support = -> [XZ_Plane002]
  expr: Constraints[2] = <<params>>.USBport_offset_x
  expr: Constraints[1] = <<params>>.USBport_height
  expr: Constraints[0] = <<params>>.USBport_diam
  sketch-geometry (1):
    g0: Circle CenterX=-16 CenterY=27 CenterZ=0 NormalX=0 NormalY=0 NormalZ=1 AngleXU=0 Radius=7
  constraints (3):
    c: Diameter(g0) = 14
    c: DistanceY(g-1,g0) = 27
    c: DistanceX(g0,g-1) = 16
FEATURE [PartDesign::Pocket] Pocket012  label="USBPortHole"
  BaseFeature = -> Pocket011
  Length = 5
  Length2 = 100
  Profile = -> Sketch025
  Type = 1
FEATURE [PartDesign::Plane] DatumPlane011  label="Datum_USBCoverMtHole"
  AttachmentOffset = pos=(0,0,-115) rot=(1,0,0;0.41241rad)
  Length = 183.326
  MapMode = 5
  Placement = pos=(0,115,2.55e-14) rot=(1,0,0;1.98321rad)
  ResizeMode = 0
  Support = -> [XZ_Plane002]
  Width = 157.743
  expr: .AttachmentOffset.Rotation.Roll = <<params>>.shell_wall_angle
FEATURE [Sketcher::SketchObject] Sketch026  label="Sketch_USBCoverMt"
  FullyConstrained = true
  MapMode = 5
  Placement = pos=(0,115,2.84e-14) rot=(1,0,0;1.98321rad)
  Support = -> [DatumPlane011]
  expr: Constraints[1] = <<params>>.m2_hole_clear_diam
  expr: Constraints[0] = <<params>>.USBport_offset_x
  sketch-geometry (1):
    g0: Circle CenterX=-16 CenterY=41 CenterZ=0 NormalX=0 NormalY=0 NormalZ=1 AngleXU=0 Radius=1.25
  constraints (3):
    c: DistanceX(g0,g-1) = 16
    c: Diameter(g0) = 2.5
    c: DistanceY(g-1,g0) = 41
FEATURE [PartDesign::Pocket] Pocket013  label="USBPortCoverMtHole"
  BaseFeature = -> Pocket012
  Length = 5
  Length2 = 100
  Profile = -> Sketch026
  Reversed = true
  Type = 0
FEATURE [Sketcher::SketchObject] Sketch027
  FullyConstrained = true
  MapMode = 5
  Placement = pos=(0,0,0) rot=(1,0,0;1.5708rad)
  Support = -> [XZ_Plane]
  expr: Constraints[3] = <<params>>.USBport_cover_mt_diam
  expr: Constraints[4] = <<params>>.USBport_cover_spacing
  expr: Constraints[2] = <<params>>.USBport_cover_diam
  expr: Constraints[13] = <<params>>.USBport_cover_spacing
  sketch-geometry (6):
    g0: Circle CenterX=0 CenterY=0 CenterZ=0 NormalX=0 NormalY=0 NormalZ=1 AngleXU=0 Radius=3.5
    g1: Circle CenterX=0 CenterY=-11 CenterZ=0 NormalX=0 NormalY=0 NormalZ=1 AngleXU=0 Radius=8
    g2: ArcOfCircle CenterX=0 CenterY=-11 CenterZ=0 NormalX=0 NormalY=0 NormalZ=1 AngleXU=0 Radius=8 StartAngle=2.29607 EndAngle=7.12871
    g3: ArcOfCircle CenterX=0 CenterY=0 CenterZ=0 NormalX=0 NormalY=0 NormalZ=1 AngleXU=0 Radius=3.5 StartAngle=6.18327 EndAngle=9.52469
    g4: ArcOfCircle CenterX=-8.95512 CenterY=-0.897727 CenterZ=0 NormalX=0 NormalY=0 NormalZ=1 AngleXU=0 Radius=5.5 StartAngle=5.43766 EndAngle=6.3831
    g5: ArcOfCircle CenterX=8.95512 CenterY=-0.897727 CenterZ=0 NormalX=0 NormalY=0 NormalZ=1 AngleXU=0 Radius=5.5 StartAngle=3.04168 EndAngle=3.98711
  constraints (15):
    c: Coincident(g0,g-1)
    c: PointOnObject(g1,g-2)
    c: Diameter(g1) = 16
    c: Diameter(g0) = 7
    c: DistanceY(g1,g-1) = 11
    c: Coincident(g2,g1)
    c: Coincident(g3,g-1)
    c: Tangent(g3,g4) = 1.5708
    c: Tangent(g2,g4) = 1.5708
    c: Tangent(g3,g5) = 1.5708
    c: Tangent(g2,g5) = 1.5708
    c: PointOnObject(g3,g0)
    c: PointOnObject(g2,g1)
    c: Diameter(g5) = 11
    c: Equal(g4,g5)
FEATURE [PartDesign::Pad] Pad  label="MainExt"
  Direction = (1,1,1)
  Length = 1.2
  Length2 = 100
  Placement = pos=(0,0,0) rot=(1,0,0;1.5708rad)
  Profile = -> Sketch027
  Type = 0
FEATURE [Sketcher::SketchObject] Sketch029
  FullyConstrained = true
  MapMode = 5
  Placement = pos=(0,0,0) rot=(0.57735,0.57735,0.57735;2.0944rad)
  Support = -> [YZ_Plane004]
  expr: Constraints[27] = <<params>>.USBport_cover_thickness
  expr: Constraints[29] = <<params>>.USBport_cover_mt_diam / 2 - <<params>>.USBport_cover_thickness / 2
  expr: Constraints[26] = <<params>>.USBport_cover_thickness / 2
  expr: Constraints[28] = <<params>>.USBport_cover_pivot_height
  expr: Constraints[25] = <<params>>.USBport_cover_thickness / 2
  expr: Constraints[23] = <<params>>.m2_hole_clear_diam / 2
  expr: Constraints[24] = <<params>>.USBport_cover_pivot_inner_diam / 2
  sketch-geometry (10):
    g0: LineSegment StartX=0 StartY=1.25 StartZ=0 EndX=2.5 EndY=1.25 EndZ=0
    g1: LineSegment StartX=0 StartY=2 StartZ=0 EndX=0.7 EndY=2 EndZ=0
    g2: LineSegment StartX=0 StartY=1.25 StartZ=0 EndX=0 EndY=2 EndZ=0
    g3: LineSegment StartX=0.7 StartY=2 StartZ=0 EndX=1.3 EndY=2.6 EndZ=0
    g4: LineSegment StartX=1.3 StartY=2.6 StartZ=0 EndX=1.3 EndY=2.9 EndZ=0
    g5: LineSegment StartX=1.3 StartY=2.9 StartZ=0 EndX=1.9 EndY=2.9 EndZ=0
    g6: LineSegment StartX=1.9 StartY=2.9 StartZ=0 EndX=2.5 EndY=2.3 EndZ=0
    g7: LineSegment StartX=2.5 StartY=2.3 StartZ=0 EndX=2.5 EndY=1.25 EndZ=0
    g8: LineSegment StartX=0.7 StartY=2 StartZ=0 EndX=2.5 EndY=2 EndZ=0
    g9: LineSegment StartX=1.9 StartY=2.9 StartZ=0 EndX=1.9 EndY=1.25 EndZ=0
  constraints (30):
    c: PointOnObject(g0,g-2)
    c: Horizontal(g0)
    c: PointOnObject(g1,g-2)
    c: Horizontal(g1)
    c: Coincident(g2,g0)
    c: Coincident(g2,g1)
    c: Coincident(g3,g1)
    c: Coincident(g4,g3)
    c: Vertical(g4)
    c: Coincident(g5,g4)
    c: Horizontal(g5)
    c: Coincident(g6,g5)
    c: Coincident(g7,g6)
    c: Coincident(g7,g0)
    c: Vertical(g7)
    c: Coincident(g8,g1)
    c: PointOnObject(g8,g7)
    c: Horizontal(g8)
    c: Angle(g8,g3) = 0.785398
    c: Coincident(g9,g5)
    c: PointOnObject(g9,g0)
    c: Vertical(g9)
    c: Angle(g9,g6) = 0.785398
    c: DistanceY(g-1,g0) = 1.25
    c: DistanceY(g-1,g1) = 2
    c: DistanceX(g5,g6) = 0.6
    c: DistanceX(g1,g3) = 0.6
    c: DistanceX(g4,g6) = 1.2
    c: DistanceX(g0,g3) = 1.3
    c: DistanceY(g-1,g4) = 2.9
FEATURE [Sketcher::SketchObject] Sketch030
  FullyConstrained = true
  MapMode = 5
  Placement = pos=(0,0,0) rot=(0.57735,0.57735,0.57735;2.0944rad)
  Support = -> [YZ_Plane]
  expr: Constraints[14] = <<params>>.USBport_cover_pivot_outer_diam / 2
  expr: Constraints[15] = <<params>>.USBport_cover_thickness
  expr: Constraints[16] = <<params>>.USBport_cover_thickness / 2
  sketch-geometry (6):
    g0: LineSegment StartX=0 StartY=2.75 StartZ=0 EndX=-0.6 EndY=2.15 EndZ=0
    g1: LineSegment StartX=-0.6 StartY=2.15 StartZ=0 EndX=-1.2 EndY=2.15 EndZ=0
    g2: LineSegment StartX=-1.2 StartY=2.15 StartZ=0 EndX=-1.2 EndY=0 EndZ=0
    g3: LineSegment StartX=-1.2 StartY=0 StartZ=0 EndX=0 EndY=0 EndZ=0
    g4: LineSegment StartX=0 StartY=0 StartZ=0 EndX=0 EndY=2.75 EndZ=0
    g5: LineSegment StartX=-0.6 StartY=2.15 StartZ=0 EndX=-0.6 EndY=0 EndZ=0
  constraints (17):
    c: PointOnObject(g0,g-2)
    c: Coincident(g1,g0)
    c: Horizontal(g1)
    c: Coincident(g2,g1)
    c: Vertical(g2)
    c: Coincident(g3,g2)
    c: Coincident(g3,g-1)
    c: Horizontal(g3)
    c: Coincident(g4,g3)
    c: Coincident(g4,g0)
    c: Coincident(g5,g0)
    c: PointOnObject(g5,g3)
    c: Vertical(g5)
    c: Angle(g0,g4) = 0.785398
    c: DistanceY(g3,g0) = 2.15
    c: DistanceX(g2,g3) = 1.2
    c: DistanceX(g0,g0) = 0.6
FEATURE [PartDesign::Groove] Groove
  Angle = 360
  Axis = (1e-16,1,-1e-16)
  Base = (0,0,0)
  BaseFeature = -> Pad
  Placement = pos=(0,0,0) rot=(1,0,0;1.5708rad)
  Profile = -> Sketch030
  ReferenceAxis = -> Y_Axis
  Reversed = true
FEATURE [PartDesign::Chamfer] Chamfer
  Angle = 45
  Base = -> Groove [Edge11]
  BaseFeature = -> Groove
  ChamferType = 0
  FlipDirection = false
  Placement = pos=(0,0,0) rot=(1,0,0;1.5708rad)
  Size = 0.6
  Size2 = 1
  SupportTransform = false
FEATURE [PartDesign::Body] Body  label="PB3D_USBPortCover"
  Group = -> [Sketch027,Pad,Sketch030,Groove,Chamfer]
  Origin = -> Origin
  Placement = pos=(-16,98.75,37.54) rot=(1,0,0;0.436332rad)
  Tip = -> Chamfer
FEATURE [PartDesign::Revolution] Revolution
  Angle = 360
  Axis = (1e-16,1,-1e-16)
  Base = (0,0,0)
  Placement = pos=(0,0,0) rot=(0.57735,0.57735,0.57735;2.0944rad)
  Profile = -> Sketch029
  ReferenceAxis = -> Y_Axis004
FEATURE [PartDesign::Body] Body002  label="PB3D_USBPortCoverPivot"
  Group = -> [Sketch029,Revolution]
  Origin = -> Origin004
  Placement = pos=(-16,97.8437,37.1174) rot=(1,0,0;0.436332rad)
  Tip = -> Revolution
FEATURE [Sketcher::SketchObject] Sketch031  label="Sketch_Shell_Inner_AboveFeet_Bot"
  FullyConstrained = true
  MapMode = 5
  Placement = pos=(0,0,7.5) rot=(0,0,1;0rad)
  Support = -> [DatumPlane002]
  expr: Constraints[119] = <<params>>.std_rad / 2
  expr: Constraints[80] = <<params>>.std_rad
  expr: Constraints[175] = <<params>>.shell_footback_loc
  expr: Constraints[77] = <<params>>.back_vert_edge
  expr: Constraints[92] = <<params>>.shell_wall_thick
  expr: Constraints[162] = <<params>>.std_rad / 2
  expr: Constraints[41] = <<params>>.tail_rad
  expr: Constraints[93] = <<params>>.shell_wall_thick
  expr: Constraints[79] = <<params>>.plate_width
  expr: Constraints[36] = <<params>>.wheel_well_plate_width
  expr: Constraints[96] = <<params>>.shell_wall_thick
  expr: Constraints[102] = <<params>>.shell_wall_thick
  expr: Constraints[95] = <<params>>.shell_wall_thick
  expr: Constraints[76] = <<params>>.front_vert_edge
  expr: Constraints[190] = <<params>>.shell_footback_width
  expr: Constraints[124] = Spreadsheet.shell_footside_width
  expr: Constraints[40] = <<params>>.plate_length
  expr: Constraints[65] = <<params>>.std_rad
  expr: Constraints[63] = <<params>>.std_rad
  expr: Constraints[81] = <<params>>.std_rad
  expr: Constraints[47] = <<params>>.front_diameter
  expr: Constraints[151] = <<params>>.shell_wall_thick
  expr: Constraints[78] = <<params>>.wheel_well_clearance
  expr: Constraints[42] = <<params>>.tail_width
  sketch-geometry (77):
    g0: LineSegment StartX=-57.5 StartY=17 StartZ=0 EndX=-57.5 EndY=-17 EndZ=0
    g1: LineSegment StartX=57.5 StartY=17 StartZ=0 EndX=57.5 EndY=-17 EndZ=0
    g2: LineSegment StartX=-57.5 StartY=0 StartZ=0 EndX=57.5 EndY=0 EndZ=0
    g3: LineSegment StartX=-64.5 StartY=-24 StartZ=0 EndX=64.5 EndY=-24 EndZ=0
    g4: LineSegment StartX=-64.5 StartY=24 StartZ=0 EndX=64.5 EndY=24 EndZ=0
    g5: LineSegment StartX=-64.5 StartY=-24 StartZ=0 EndX=-75.5 EndY=-24 EndZ=0
    g6: LineSegment StartX=64.5 StartY=-24 StartZ=0 EndX=75.5 EndY=-24 EndZ=0
    g7: ArcOfCircle CenterX=0 CenterY=52.6846 CenterZ=0 NormalX=0 NormalY=0 NormalZ=1 AngleXU=0 Radius=112.5 StartAngle=3.96017 EndAngle=5.4646
    g8: LineSegment StartX=-64.5 StartY=24 StartZ=0 EndX=-75.5 EndY=24 EndZ=0
    g9: LineSegment StartX=64.5 StartY=24 StartZ=0 EndX=75.5 EndY=24 EndZ=0
    g10: LineSegment StartX=-77.1162 StartY=42.1781 StartZ=0 EndX=-29.0404 EndY=108.13 EndZ=0
    g11: LineSegment StartX=-25 StartY=110.185 StartZ=0 EndX=25 EndY=110.185 EndZ=0
    g12: LineSegment StartX=29.0404 StartY=108.13 StartZ=0 EndX=77.1162 EndY=42.1781 EndZ=0
    g13: LineSegment StartX=0 StartY=0 StartZ=0 EndX=0 EndY=110.185 EndZ=0
    g14: ArcOfCircle CenterX=-25 CenterY=105.185 CenterZ=0 NormalX=0 NormalY=0 NormalZ=1 AngleXU=0 Radius=5 StartAngle=1.5708 EndAngle=2.5117
    g15: ArcOfCircle CenterX=25 CenterY=105.185 CenterZ=0 NormalX=0 NormalY=0 NormalZ=1 AngleXU=0 Radius=5 StartAngle=0.629894 EndAngle=1.5708
    g16: ArcOfCircle CenterX=-64.5 CenterY=17 CenterZ=0 NormalX=0 NormalY=0 NormalZ=1 AngleXU=0 Radius=7 StartAngle=0 EndAngle=1.5708
    g17: ArcOfCircle CenterX=-64.5 CenterY=-17 CenterZ=0 NormalX=0 NormalY=0 NormalZ=1 AngleXU=0 Radius=7 StartAngle=4.71239 EndAngle=6.28319
    g18: ArcOfCircle CenterX=64.5 CenterY=-17 CenterZ=0 NormalX=0 NormalY=0 NormalZ=1 AngleXU=0 Radius=7 StartAngle=3.14159 EndAngle=4.71239
    g19: ArcOfCircle CenterX=64.5 CenterY=17 CenterZ=0 NormalX=0 NormalY=0 NormalZ=1 AngleXU=0 Radius=7 StartAngle=1.5708 EndAngle=3.14159
    g20: GeomPoint X=0 Y=-59.8154 Z=0
    g21: Circle CenterX=0 CenterY=52.6846 CenterZ=0 NormalX=0 NormalY=0 NormalZ=1 AngleXU=0 Radius=112.5
    g22: LineSegment StartX=77.5 StartY=26 StartZ=0 EndX=77.5 EndY=41 EndZ=0
    g23: LineSegment StartX=77.5 StartY=-26 StartZ=0 EndX=77.5 EndY=-28 EndZ=0
    g24: LineSegment StartX=-77.5 StartY=-28 StartZ=0 EndX=-77.5 EndY=-26 EndZ=0
    g25: LineSegment StartX=-77.5 StartY=26 StartZ=0 EndX=-77.5 EndY=41 EndZ=0
    g26: ArcOfCircle CenterX=75.5 CenterY=-28 CenterZ=0 NormalX=0 NormalY=0 NormalZ=1 AngleXU=0 Radius=2 StartAngle=5.4646 EndAngle=6.28319
    g27: ArcOfCircle CenterX=75.5 CenterY=-26 CenterZ=0 NormalX=0 NormalY=0 NormalZ=1 AngleXU=0 Radius=2 StartAngle=0 EndAngle=1.5708
    g28: ArcOfCircle CenterX=-75.5 CenterY=-28 CenterZ=0 NormalX=0 NormalY=0 NormalZ=1 AngleXU=0 Radius=2 StartAngle=3.14159 EndAngle=3.96017
    g29: ArcOfCircle CenterX=-75.5 CenterY=-26 CenterZ=0 NormalX=0 NormalY=0 NormalZ=1 AngleXU=0 Radius=2 StartAngle=1.5708 EndAngle=3.14159
    g30: ArcOfCircle CenterX=75.5 CenterY=26 CenterZ=0 NormalX=0 NormalY=0 NormalZ=1 AngleXU=0 Radius=2 StartAngle=4.71239 EndAngle=6.28319
    g31: ArcOfCircle CenterX=75.5 CenterY=41 CenterZ=0 NormalX=0 NormalY=0 NormalZ=1 AngleXU=0 Radius=2 StartAngle=1.2e-15 EndAngle=0.629894
    g32: ArcOfCircle CenterX=-75.5 CenterY=26 CenterZ=0 NormalX=0 NormalY=0 NormalZ=1 AngleXU=0 Radius=2 StartAngle=3.14159 EndAngle=4.71239
    g33: ArcOfCircle CenterX=-75.5 CenterY=41 CenterZ=0 NormalX=0 NormalY=0 NormalZ=1 AngleXU=0 Radius=2 StartAngle=2.5117 EndAngle=3.14159
    g34: LineSegment StartX=77.5 StartY=26 StartZ=0 EndX=77.5 EndY=-26 EndZ=0
    g35: LineSegment StartX=-77.5 StartY=26 StartZ=0 EndX=-77.5 EndY=-26 EndZ=0
    g36: ArcOfCircle CenterX=0 CenterY=52.6846 CenterZ=0 NormalX=0 NormalY=0 NormalZ=1 AngleXU=0 Radius=110.5 StartAngle=4.04818 EndAngle=5.3766
    g37: GeomPoint X=0 Y=-57.8154 Z=0
    g38: LineSegment StartX=-75.5 StartY=-24 StartZ=0 EndX=-75.5 EndY=24 EndZ=0
    g39: LineSegment StartX=-23.9829 StartY=108.185 StartZ=0 EndX=23.9829 EndY=108.185 EndZ=0
    g40: LineSegment StartX=-68.3081 StartY=50.8661 StartZ=0 EndX=-43.5911 EndY=84.7736 EndZ=0
    g41: LineSegment StartX=75.5 StartY=-24 StartZ=0 EndX=75.5 EndY=24 EndZ=0
    g42: LineSegment StartX=43.5911 StartY=84.7736 StartZ=0 EndX=68.3081 EndY=50.8661 EndZ=0
    g43: GeomPoint X=0 Y=108.185 Z=0
    g44: LineSegment StartX=-29.0404 StartY=108.13 StartZ=0 EndX=-27.4243 EndY=106.952 EndZ=0
    g45: LineSegment StartX=75.5 StartY=-24 StartZ=0 EndX=69.5 EndY=-24 EndZ=0
    g46: LineSegment StartX=68.5 StartY=-25 StartZ=0 EndX=68.5 EndY=-33.5361 EndZ=0
    g47: ArcOfCircle CenterX=69.5 CenterY=-25 CenterZ=0 NormalX=0 NormalY=0 NormalZ=1 AngleXU=0 Radius=1 StartAngle=1.5708 EndAngle=3.14159
    g48: ArcOfCircle CenterX=67.5 CenterY=-33.5361 CenterZ=0 NormalX=0 NormalY=0 NormalZ=1 AngleXU=0 Radius=1 StartAngle=5.3766 EndAngle=6.28319
    g49: LineSegment StartX=-75.5 StartY=-24 StartZ=0 EndX=-69.5 EndY=-24 EndZ=0
    g50: LineSegment StartX=-68.5 StartY=-25 StartZ=0 EndX=-68.5 EndY=-33.5361 EndZ=0
    g51: ArcOfCircle CenterX=-69.5 CenterY=-25 CenterZ=0 NormalX=0 NormalY=0 NormalZ=1 AngleXU=0 Radius=1 StartAngle=0 EndAngle=1.5708
    g52: ArcOfCircle CenterX=-67.5 CenterY=-33.5361 CenterZ=0 NormalX=0 NormalY=0 NormalZ=1 AngleXU=0 Radius=1 StartAngle=3.14159 EndAngle=4.04818
    g53: LineSegment StartX=75.5 StartY=24 StartZ=0 EndX=69.5 EndY=24 EndZ=0
    g54: LineSegment StartX=68.5 StartY=25 StartZ=0 EndX=68.5 EndY=50.277 EndZ=0
    g55: ArcOfCircle CenterX=69.5 CenterY=25 CenterZ=0 NormalX=0 NormalY=0 NormalZ=1 AngleXU=0 Radius=1 StartAngle=3.14159 EndAngle=4.71239
    g56: ArcOfCircle CenterX=67.5 CenterY=50.277 CenterZ=0 NormalX=0 NormalY=0 NormalZ=1 AngleXU=0 Radius=1 StartAngle=-2.7e-15 EndAngle=0.629894
    g57: LineSegment StartX=-75.5 StartY=24 StartZ=0 EndX=-69.5 EndY=24 EndZ=0
    g58: LineSegment StartX=-68.5 StartY=25 StartZ=0 EndX=-68.5 EndY=50.277 EndZ=0
    g59: ArcOfCircle CenterX=-67.5 CenterY=50.277 CenterZ=0 NormalX=0 NormalY=0 NormalZ=1 AngleXU=0 Radius=1 StartAngle=2.5117 EndAngle=3.14159
    g60: ArcOfCircle CenterX=-69.5 CenterY=25 CenterZ=0 NormalX=0 NormalY=0 NormalZ=1 AngleXU=0 Radius=1 StartAngle=4.71239 EndAngle=6.28319
    g61: LineSegment StartX=-33.783 StartY=85.1846 StartZ=0 EndX=-42.783 EndY=85.1846 EndZ=0
    g62: LineSegment StartX=33.783 StartY=85.1846 StartZ=0 EndX=42.783 EndY=85.1846 EndZ=0
    g63: LineSegment StartX=27.4243 StartY=106.952 StartZ=0 EndX=29.0404 EndY=108.13 EndZ=0
    g64: ArcOfCircle CenterX=-33.783 CenterY=86.1846 CenterZ=0 NormalX=0 NormalY=0 NormalZ=1 AngleXU=0 Radius=1 StartAngle=4.71239 EndAngle=6.28319
    g65: ArcOfCircle CenterX=-42.783 CenterY=84.1846 CenterZ=0 NormalX=0 NormalY=0 NormalZ=1 AngleXU=0 Radius=1 StartAngle=1.5708 EndAngle=2.5117
    g66: ArcOfCircle CenterX=33.783 CenterY=86.1846 CenterZ=0 NormalX=0 NormalY=0 NormalZ=1 AngleXU=0 Radius=1 StartAngle=3.14159 EndAngle=4.71239
    g67: ArcOfCircle CenterX=42.783 CenterY=84.1846 CenterZ=0 NormalX=0 NormalY=0 NormalZ=1 AngleXU=0 Radius=1 StartAngle=0.629894 EndAngle=1.5708
    g68: LineSegment StartX=32.783 StartY=86.1846 StartZ=0 EndX=32.783 EndY=99.2747 EndZ=0
    g69: LineSegment StartX=32.5911 StartY=99.8638 StartZ=0 EndX=28.0234 EndY=106.13 EndZ=0
    g70: ArcOfCircle CenterX=31.783 CenterY=99.2747 CenterZ=0 NormalX=0 NormalY=0 NormalZ=1 AngleXU=0 Radius=1 StartAngle=7e-15 EndAngle=0.629894
    g71: ArcOfCircle CenterX=-23.9829 CenterY=103.185 CenterZ=0 NormalX=0 NormalY=0 NormalZ=1 AngleXU=0 Radius=5 StartAngle=1.5708 EndAngle=2.5117
    g72: ArcOfCircle CenterX=23.9829 CenterY=103.185 CenterZ=0 NormalX=0 NormalY=0 NormalZ=1 AngleXU=0 Radius=5 StartAngle=0.629894 EndAngle=1.5708
    g73: LineSegment StartX=-32.783 StartY=86.1846 StartZ=0 EndX=-32.783 EndY=99.2747 EndZ=0
    g74: LineSegment StartX=-32.5911 StartY=99.8638 StartZ=0 EndX=-28.0234 EndY=106.13 EndZ=0
    g75: ArcOfCircle CenterX=-31.783 CenterY=99.2747 CenterZ=0 NormalX=0 NormalY=0 NormalZ=1 AngleXU=0 Radius=1 StartAngle=2.5117 EndAngle=3.14159
    g76: LineSegment StartX=-32.783 StartY=86.1846 StartZ=0 EndX=32.783 EndY=86.1846 EndZ=0
  constraints (193):
    c: Vertical(g0)
    c: Vertical(g1)
    c: Horizontal(g2)
    c: Symmetric(g2,g2,g-1)
    c: Horizontal(g3)
    c: Horizontal(g5)
    c: Horizontal(g6)
    c: PointOnObject(g7,g-2)
    c: Horizontal(g8)
    c: Horizontal(g9)
    c: Horizontal(g11)
    c: Coincident(g13,g-1)
    c: PointOnObject(g13,g-2)
    c: Tangent(g10,g14) = 1.5708
    c: Tangent(g11,g14) = 1.5708
    c: Tangent(g11,g15) = 1.5708
    c: Tangent(g12,g15) = 1.5708
    c: Tangent(g8,g16) = -1.5708
    c: Tangent(g0,g16) = 1.5708
    c: Tangent(g5,g17) = 1.5708
    c: Tangent(g0,g17) = 1.5708
    c: Tangent(g1,g18) = -1.5708
    c: Tangent(g6,g18) = -1.5708
    c: Tangent(g1,g19) = -1.5708
    c: Tangent(g9,g19) = 1.5708
    c: Equal(g15,g14)
    c: Symmetric(g11,g11,g13)
    c: Equal(g18,g19)
    c: Equal(g19,g16)
    c: Equal(g16,g17)
    c: PointOnObject(g20,g-2)
    c: PointOnObject(g20,g7)
    c: Coincident(g4,g8)
    c: Coincident(g4,g9)
    c: Coincident(g3,g6)
    c: Coincident(g3,g5)
    c: DistanceX(g2,g2) = 115
    c: Symmetric(g0,g0,g2)
    c: Symmetric(g1,g1,g2)
    c: Radius(g19) = 7
    c: DistanceY(g20,g11) = 170
    c: Radius(g15) = 5
    c: DistanceX(g11,g11) = 50
    c: Equal(g9,g8)
    c: Equal(g9,g6)
    c: Coincident(g21,g7)
    c: PointOnObject(g20,g21)
    c: Diameter(g21) = 225
    c: Vertical(g22)
    c: Vertical(g23)
    c: Vertical(g24)
    c: Vertical(g25)
    c: Equal(g5,g8)
    c: Equal(g10,g12)
    c: Tangent(g7,g26) = -1.5708
    c: Tangent(g23,g26) = 1.5708
    c: Tangent(g23,g27) = 1.5708
    c: Tangent(g6,g27) = 1.5708
    c: Tangent(g7,g28) = -1.5708
    c: Tangent(g24,g28) = 1.5708
    c: Tangent(g24,g29) = 1.5708
    c: Tangent(g5,g29) = -1.5708
    c: Equal(g29,g27)
    c: Radius(g27) = 2
    c: Equal(g26,g28)
    c: Radius(g26) = 2
    c: Tangent(g9,g30) = -1.5708
    c: Tangent(g22,g30) = -1.5708
    c: Tangent(g22,g31) = -1.5708
    c: Tangent(g12,g31) = 1.5708
    c: Tangent(g8,g32) = 1.5708
    c: Tangent(g25,g32) = 1.5708
    c: Tangent(g10,g33) = 1.5708
    c: Tangent(g25,g33) = 1.5708
    c: Equal(g30,g32)
    c: Equal(g31,g33)
    c: DistanceY(g23,g23) = 2
    c: DistanceY(g22,g22) = 15
    c: DistanceY(g6,g9) = 48
    c: DistanceX(g24,g23) = 155
    c: Radius(g30) = 2
    c: Radius(g31) = 2
    c: Coincident(g34,g22)
    c: Coincident(g34,g23)
    c: Coincident(g35,g25)
    c: Coincident(g35,g24)
    c: PointOnObject(g37,g-2)
    c: PointOnObject(g37,g36)
    c: Vertical(g38)
    c: Horizontal(g39)
    c: Vertical(g41)
    c: PointOnObject(g43,g13)
    c: DistanceY(g20,g37) = 2
    c: DistanceY(g43,g13) = 2
    c: Parallel(g42,g12)
    c: DistanceX(g41,g22) = 2
    c: DistanceX(g25,g38) = 2
    c: Parallel(g40,g10)
    c: PointOnObject(g44,g10)
    c: PointOnObject(g44,g40)
    c: Perpendicular(g44,g10)
    c: PointOnObject(g10,g44)
    c: Distance(g44) = 2
    c: Coincident(g45,g6)
    c: Vertical(g46)
    c: PointOnObject(g41,g45)
    c: Tangent(g46,g47) = -1.5708
    c: Tangent(g45,g47) = -1.5708
    c: Tangent(g46,g48) = 1.5708
    c: Tangent(g36,g48) = -1.5708
    c: PointOnObject(g38,g5)
    c: Coincident(g49,g38)
    c: Vertical(g50)
    c: Tangent(g49,g51) = 1.5708
    c: Tangent(g50,g51) = 1.5708
    c: Tangent(g36,g52) = -1.5708
    c: Tangent(g50,g52) = -1.5708
    c: Equal(g49,g45)
    c: Horizontal(g45)
    c: Radius(g47) = 1
    c: Horizontal(g49)
    c: Equal(g51,g52)
    c: Equal(g52,g47)
    c: Equal(g47,g48)
    c: DistanceX(g46,g41) = 7
    c: PointOnObject(g41,g9)
    c: Coincident(g53,g41)
    c: Vertical(g54)
    c: Tangent(g53,g55) = 1.5708
    c: Tangent(g54,g55) = 1.5708
    c: Tangent(g54,g56) = -1.5708
    c: Tangent(g42,g56) = 1.5708
    c: Equal(g47,g55)
    c: Horizontal(g53)
    c: Equal(g56,g55)
    c: Equal(g53,g45)
    c: PointOnObject(g38,g8)
    c: Coincident(g57,g38)
    c: Vertical(g58)
    c: Tangent(g58,g59) = 1.5708
    c: Tangent(g40,g59) = 1.5708
    c: Tangent(g57,g60) = -1.5708
    c: Tangent(g58,g60) = -1.5708
    c: Equal(g51,g60)
    c: Horizontal(g57)
    c: Equal(g60,g59)
    c: Equal(g57,g49)
    c: Horizontal(g61)
    c: Horizontal(g62)
    c: PointOnObject(g63,g42)
    c: Perpendicular(g42,g63)
    c: Distance(g63) = 2
    c: Coincident(g63,g12)
    c: Tangent(g61,g64) = 1.5708
    c: Tangent(g61,g65) = -1.5708
    c: Tangent(g40,g65) = 1.5708
    c: Tangent(g62,g66) = -1.5708
    c: Tangent(g62,g67) = 1.5708
    c: Tangent(g42,g67) = 1.5708
    c: Equal(g64,g66)
    c: Equal(g67,g66)
    c: Equal(g65,g64)
    c: Radius(g67) = 1
    c: Coincident(g68,g66)
    c: Vertical(g68)
    c: Tangent(g66,g68)
    c: Parallel(g12,g69)
    c: Tangent(g68,g70) = -1.5708
    c: Tangent(g69,g70) = -1.5708
    c: Equal(g70,g66)
    c: Tangent(g39,g71) = 1.5708
    c: Tangent(g39,g72) = 1.5708
    c: Tangent(g69,g72) = -1.5708
    c: Equal(g72,g15)
    c: PointOnObject(g63,g69)
    c: DistanceY(g62,g11) = 25
    c: Coincident(g73,g64)
    c: Vertical(g73)
    c: Tangent(g64,g73)
    c: Coincident(g74,g71)
    c: Tangent(g74,g71)
    c: Tangent(g73,g75) = 1.5708
    c: Tangent(g74,g75) = 1.5708
    c: Equal(g64,g75)
    c: Equal(g71,g14)
    c: Parallel(g74,g10)
    c: Equal(g73,g68)
    c: Coincident(g76,g64)
    c: Coincident(g76,g66)
    c: Symmetric(g39,g39,g43)
    c: DistanceX(g66,g62) = 10
    c: Coincident(g36,g7)
    c: Horizontal(g76)
FEATURE [PartDesign::SubtractiveLoft] SubtractiveLoft003  label="Shell_BotBrack_FootAngleCut"
  BaseFeature = -> Pocket013
  Closed = false
  Profile = -> Sketch031
  Ruled = false
  Sections = -> [Sketch006]
FEATURE [PartDesign::Pocket] Pocket014  label="LSRHole_L"
  BaseFeature = -> SubtractiveLoft003
  Length = 5
  Length2 = 100
  Profile = -> Sketch019
  Reversed = true
  Type = 1
FEATURE [PartDesign::Pocket] Pocket015  label="LSRHole_R"
  BaseFeature = -> Pocket014
  Length = 5
  Length2 = 100
  Profile = -> Sketch020
  Reversed = true
  Type = 1
FEATURE [Sketcher::SketchObject] Sketch032  label="Sketch_XPort"
  FullyConstrained = true
  MapMode = 5
  Placement = pos=(0,0,0) rot=(1,0,0;1.5708rad)
  Support = -> [XZ_Plane003]
  expr: Constraints[8] = <<params>>.xport_offset_loc
  expr: Constraints[7] = <<params>>.xport_height_loc
  expr: Constraints[6] = <<params>>.xport_diam
  sketch-geometry (4):
    g0: Circle CenterX=-43 CenterY=33.25 CenterZ=0 NormalX=0 NormalY=0 NormalZ=1 AngleXU=0 Radius=6.5
    g1: Circle CenterX=43 CenterY=33.25 CenterZ=0 NormalX=0 NormalY=0 NormalZ=1 AngleXU=0 Radius=6.5
    g2: LineSegment StartX=-43 StartY=33.25 StartZ=0 EndX=43 EndY=33.25 EndZ=0
    g3: GeomPoint X=0 Y=33.25 Z=0
  constraints (9):
    c: Coincident(g2,g0)
    c: Coincident(g2,g1)
    c: Horizontal(g2)
    c: PointOnObject(g3,g-2)
    c: Symmetric(g1,g0,g3)
    c: Equal(g1,g0)
    c: Diameter(g1) = 13
    c: DistanceY(g-1,g3) = 33.25
    c: DistanceX(g0,g3) = 43
FEATURE [PartDesign::Pocket] Pocket016  label="Pocket_Xports"
  BaseFeature = -> Pocket015
  Length = 5
  Length2 = 100
  Profile = -> Sketch032
  Reversed = true
  Type = 1
FEATURE [Sketcher::SketchObject] Sketch033  label="Sketch_XPortSlots"
  FullyConstrained = true
  MapMode = 5
  Placement = pos=(0,0,0) rot=(1,0,0;1.5708rad)
  Support = -> [XZ_Plane002]
  expr: Constraints[21] = <<params>>.std_wall_thick + <<params>>.std_tol_clear
  expr: Constraints[6] = <<params>>.xport_plate_diam + <<params>>.std_tol_clear
  expr: Constraints[7] = <<params>>.xport_height_loc
  expr: Constraints[8] = <<params>>.xport_offset_loc
  sketch-geometry (12):
    g0: Circle CenterX=-43 CenterY=33.25 CenterZ=0 NormalX=0 NormalY=0 NormalZ=1 AngleXU=0 Radius=8.15
    g1: Circle CenterX=43 CenterY=33.25 CenterZ=0 NormalX=0 NormalY=0 NormalZ=1 AngleXU=0 Radius=8.15
    g2: LineSegment StartX=-43 StartY=33.25 StartZ=0 EndX=43 EndY=33.25 EndZ=0
    g3: GeomPoint X=0 Y=33.25 Z=0
    g4: LineSegment StartX=-44.15 StartY=33.25 StartZ=0 EndX=-41.85 EndY=33.25 EndZ=0
    g5: LineSegment StartX=41.85 StartY=33.25 StartZ=0 EndX=44.15 EndY=33.25 EndZ=0
    g6: LineSegment StartX=41.85 StartY=33.25 StartZ=0 EndX=41.85 EndY=25.1815 EndZ=0
    g7: LineSegment StartX=44.15 StartY=33.25 StartZ=0 EndX=44.15 EndY=25.1815 EndZ=0
    g8: ArcOfCircle CenterX=43 CenterY=33.25 CenterZ=0 NormalX=0 NormalY=0 NormalZ=1 AngleXU=0 Radius=8.15 StartAngle=4.57081 EndAngle=4.85397
    g9: LineSegment StartX=-44.15 StartY=33.25 StartZ=0 EndX=-44.15 EndY=25.1815 EndZ=0
    g10: LineSegment StartX=-41.85 StartY=33.25 StartZ=0 EndX=-41.85 EndY=25.1815 EndZ=0
    g11: ArcOfCircle CenterX=-43 CenterY=33.25 CenterZ=0 NormalX=0 NormalY=0 NormalZ=1 AngleXU=0 Radius=8.15 StartAngle=4.57081 EndAngle=4.85397
  constraints (33):
    c: Coincident(g2,g0)
    c: Coincident(g2,g1)
    c: Horizontal(g2)
    c: PointOnObject(g3,g-2)
    c: Symmetric(g1,g0,g3)
    c: Equal(g1,g0)
    c: Diameter(g1) = 16.3
    c: DistanceY(g-1,g3) = 33.25
    c: DistanceX(g0,g3) = 43
    c: Horizontal(g4)
    c: Horizontal(g5)
    c: Symmetric(g5,g5,g1)
    c: Coincident(g6,g5)
    c: PointOnObject(g6,g1)
    c: Coincident(g7,g5)
    c: PointOnObject(g7,g1)
    c: Vertical(g7)
    c: Vertical(g6)
    c: Coincident(g8,g1)
    c: Coincident(g8,g6)
    c: PointOnObject(g8,g7)
    c: DistanceX(g5,g5) = 2.3
    c: Symmetric(g4,g4,g0)
    c: Coincident(g9,g4)
    c: PointOnObject(g9,g0)
    c: Vertical(g9)
    c: Coincident(g10,g4)
    c: PointOnObject(g10,g0)
    c: Vertical(g10)
    c: Coincident(g11,g0)
    c: Coincident(g11,g9)
    c: PointOnObject(g11,g10)
    c: Equal(g4,g5)
FEATURE [PartDesign::Pocket] Pocket017  label="Pocket_XportSlot"
  BaseFeature = -> Pocket016
  Length = 5
  Length2 = 100
  Profile = -> Sketch033
  Reversed = true
  Type = 1
FEATURE [Spreadsheet::Sheet] Spreadsheet001  label="ls_params"
  cells = A1=Light Sens Cent Loc; C1=Light Sens Slot; A2=LightSens Loc X; B2(lightsens_loc_x)==35mm; C2=Height; D2(lightsens_slot_height)==6.8mm; A3=LightSens Loc Y; B3(lightsens_loc_y)==50mm - 4.5mm; C3=Width; D3(lightsens_slot_width)==3.4mm; A4=LightSens Loc Z; B4(lightsens_loc_z)==16.5mm; A5=LightSens Ang X; B5(lightsens_ang_x)==65deg; A6=LightSens Ang Y; B6(lightsens_ang_y)==0deg; A7=LightSens Ang Z; B7(lightsens_ang_z)==20deg; A9=LightSens Vert Slope Ang; B9(lightsens_vert_slope_ang)==lightsens_ang_x; A11=LightSens Leng; B11(lightsens_leng)==16.51mm; A12=LightSens Width; B12(lightsens_width)==16.51mm; A13=LightSens Hole Width; B13(lightsens_hole_leng_space)==11.43mm; A14=LightSens Hole Edge Offset; B14(lightsens_hole_edge_offset)==2.54mm
FEATURE [PartDesign::Plane] DatumPlane012  label="Datum_Left_LightSens"
  AttachmentOffset = pos=(35,-45.5,16.5) rot=(0.950144,0.167536,0.262979;1.1813rad)
  Length = 238.729
  MapMode = 5
  Placement = pos=(35,-45.5,16.5) rot=(0.950144,0.167536,0.262979;1.1813rad)
  ResizeMode = 0
  Support = -> [XY_Plane002]
  Width = 185.558
  expr: .AttachmentOffset.Base.x = <<ls_params>>.lightsens_loc_x
  expr: .AttachmentOffset.Rotation.Yaw = <<ls_params>>.lightsens_ang_z
  expr: .AttachmentOffset.Base.y = <<ls_params>>.lightsens_loc_y * -1
  expr: .AttachmentOffset.Base.z = <<ls_params>>.lightsens_loc_z
  expr: .AttachmentOffset.Rotation.Roll = <<ls_params>>.lightsens_ang_x
FEATURE [PartDesign::Plane] DatumPlane013  label="Datum_Right_LightSens"
  AttachmentOffset = pos=(-35,-45.5,16.5) rot=(0.950144,-0.167536,-0.262979;1.1813rad)
  Length = 238.729
  MapMode = 5
  Placement = pos=(-35,-45.5,16.5) rot=(0.950144,-0.167536,-0.262979;1.1813rad)
  ResizeMode = 0
  Support = -> [XY_Plane002]
  Width = 185.558
  expr: .AttachmentOffset.Rotation.Roll = <<ls_params>>.lightsens_ang_x
  expr: .AttachmentOffset.Base.z = <<ls_params>>.lightsens_loc_z
  expr: .AttachmentOffset.Base.y = <<ls_params>>.lightsens_loc_y * -1
  expr: .AttachmentOffset.Rotation.Yaw = <<ls_params>>.lightsens_ang_z * -1
  expr: .AttachmentOffset.Base.x = <<ls_params>>.lightsens_loc_x * -1
FEATURE [Sketcher::SketchObject] Sketch034  label="Sketch_LightSensSlot"
  FullyConstrained = true
  MapMode = 5
  Placement = pos=(35,-45.5,16.5) rot=(0.950144,0.167536,0.262979;1.1813rad)
  Support = -> [DatumPlane012]
  expr: Constraints[7] = <<ls_params>>.lightsens_slot_width
  expr: Constraints[8] = <<ls_params>>.lightsens_slot_height
  sketch-geometry (4):
    g0: ArcOfCircle CenterX=-5.276e-13 CenterY=-3.4 CenterZ=0 NormalX=0 NormalY=0 NormalZ=1 AngleXU=0 Radius=1.7 StartAngle=3.14159 EndAngle=6.28319
    g1: ArcOfCircle CenterX=1.734e-13 CenterY=3.4 CenterZ=0 NormalX=0 NormalY=0 NormalZ=1 AngleXU=0 Radius=1.7 StartAngle=-4.97e-14 EndAngle=3.14159
    g2: LineSegment StartX=1.7 StartY=-3.4 StartZ=0 EndX=1.7 EndY=3.4 EndZ=0
    g3: LineSegment StartX=-1.7 StartY=-3.4 StartZ=0 EndX=-1.7 EndY=3.4 EndZ=0
  constraints (9):
    c: Tangent(g0,g3) = 1.5708
    c: Tangent(g0,g2) = -1.5708
    c: Tangent(g2,g1) = -1.5708
    c: Tangent(g3,g1) = 1.5708
    c: Vertical(g2)
    c: Equal(g0,g1)
    c: Symmetric(g0,g1,g-1)
    c: DistanceX(g1,g1) = 3.4
    c: DistanceY(g2,g2) = 6.8
FEATURE [Sketcher::SketchObject] Sketch035  label="Sketch_LightSensSlot001"
  FullyConstrained = true
  MapMode = 5
  Placement = pos=(-35,-45.5,16.5) rot=(0.950144,-0.167536,-0.262979;1.1813rad)
  Support = -> [DatumPlane013]
  expr: Constraints[8] = <<ls_params>>.lightsens_slot_height
  expr: Constraints[7] = <<ls_params>>.lightsens_slot_width
  sketch-geometry (4):
    g0: ArcOfCircle CenterX=-5.276e-13 CenterY=-3.4 CenterZ=0 NormalX=0 NormalY=0 NormalZ=1 AngleXU=0 Radius=1.7 StartAngle=3.14159 EndAngle=6.28319
    g1: ArcOfCircle CenterX=1.734e-13 CenterY=3.4 CenterZ=0 NormalX=0 NormalY=0 NormalZ=1 AngleXU=0 Radius=1.7 StartAngle=-4.97e-14 EndAngle=3.14159
    g2: LineSegment StartX=1.7 StartY=-3.4 StartZ=0 EndX=1.7 EndY=3.4 EndZ=0
    g3: LineSegment StartX=-1.7 StartY=-3.4 StartZ=0 EndX=-1.7 EndY=3.4 EndZ=0
  constraints (9):
    c: Tangent(g0,g3) = 1.5708
    c: Tangent(g0,g2) = -1.5708
    c: Tangent(g2,g1) = -1.5708
    c: Tangent(g3,g1) = 1.5708
    c: Vertical(g2)
    c: Equal(g0,g1)
    c: Symmetric(g0,g1,g-1)
    c: DistanceX(g1,g1) = 3.4
    c: DistanceY(g2,g2) = 6.8
FEATURE [PartDesign::Pocket] Pocket018  label="Pocket_LeftSlot_LightSens"
  BaseFeature = -> Pocket017
  Length = 5
  Length2 = 100
  Profile = -> Sketch034
  Reversed = true
  Type = 1
FEATURE [PartDesign::Pocket] Pocket019  label="Pocket_RightSlot_LightSens"
  BaseFeature = -> Pocket018
  Length = 5
  Length2 = 100
  Profile = -> Sketch035
  Reversed = true
  Type = 1
FEATURE [PartDesign::Chamfer] Chamfer001  label="Chamfer_LightSensSlots"
  Angle = 45
  Base = -> Pocket019 [Edge273,Edge50]
  BaseFeature = -> Pocket019
  ChamferType = 0
  FlipDirection = false
  Size = 1.2
  Size2 = 1
  SupportTransform = false
  expr: Size = <<params>>.shell_wall_thick - 0.8mm
FEATURE [PartDesign::Body] Body001  label="PB3D_Triplate_Shell"
  Group = -> [DatumPlane,DatumPlane001,Sketch001,Pad001,Sketch002,Sketch003,AdditiveLoft,DatumPlane002,DatumPlane003,Sketch004,Pocket,Sketch005,Sketch006,Pocket001,DatumPlane004,Sketch007,Sketch008,SubtractiveLoft,Sketch010,Sketch011,SubtractiveLoft001,Sketch012,Sketch013,SubtractiveLoft002,Sketch014,Sketch015,Sketch016,Pocket003,DatumPlane005,DatumPlane006,DatumPlane007,DatumPlane008,Sketch017,Pocket004,+34 more]
  Origin = -> Origin002
  Tip = -> Chamfer001
FEATURE [App::Part] Part001  label="PB3D_Triplate_Shell_Part"
  Group = -> [Body001,Body,Body002]
  Origin = -> Origin003
FEATURE [Mesh::Feature] Mesh  label="PB3D_Triplate_Shell (Meshed)"
